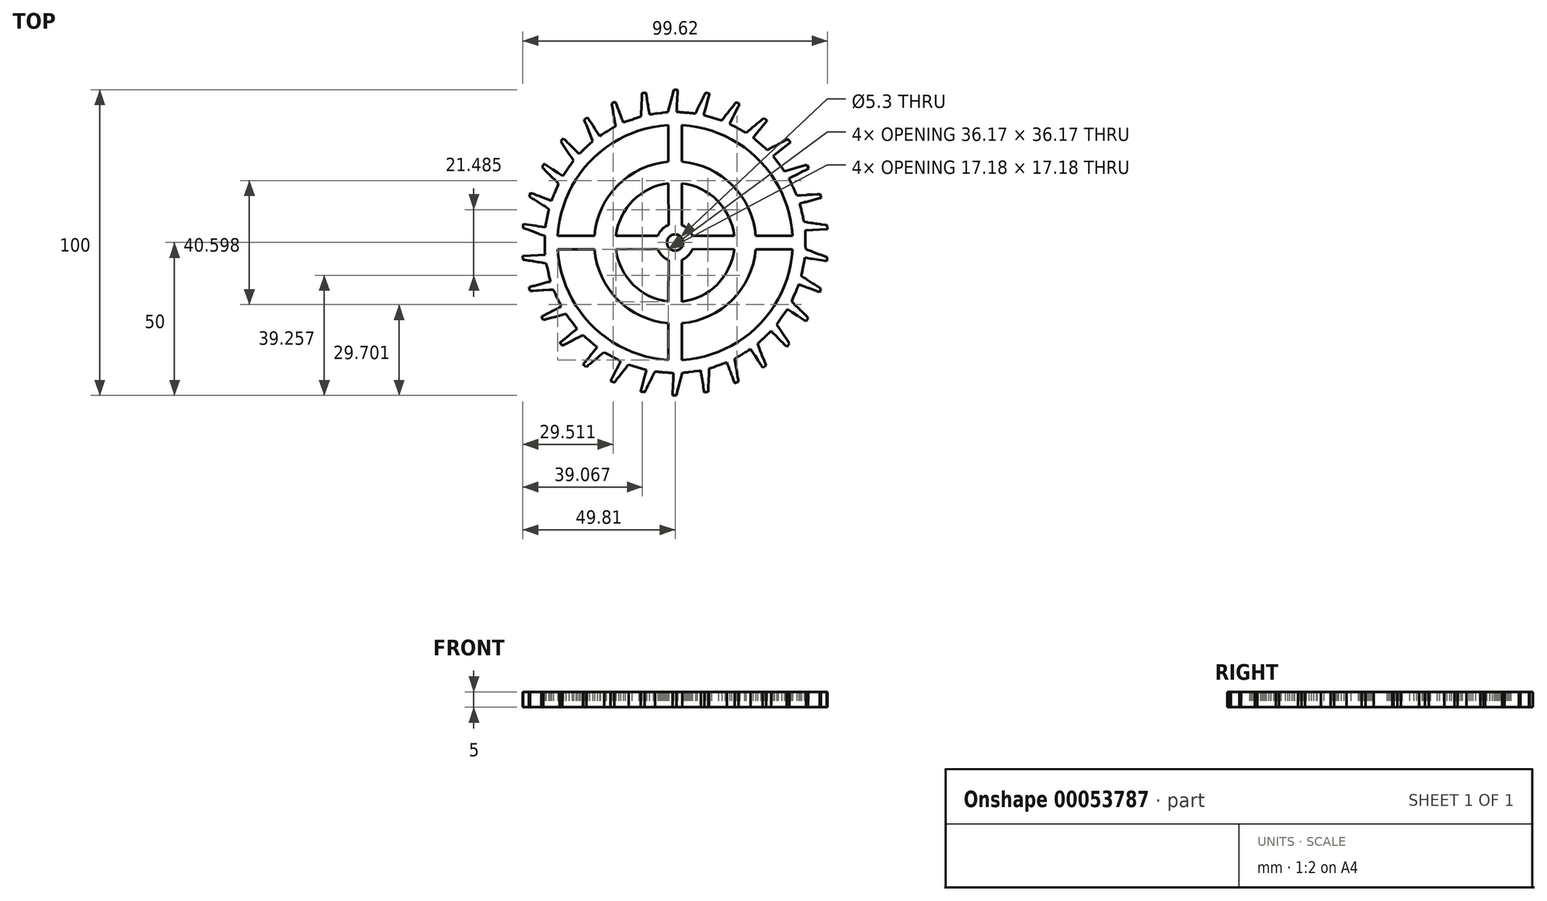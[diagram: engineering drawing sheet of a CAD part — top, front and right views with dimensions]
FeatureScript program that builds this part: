
annotation { "Feature Type Name" : "Feature", "Feature Type Description" : "" }
export const myFeature = defineFeature(function(context is Context, id is Id, definition is map)
    precondition{}
    {
        {
            var Q0;
            Q0=qCreatedBy(makeId("Top.planeOp"),FACE);
            var sketch = newSketch(context, id + "F0", { "sketchPlane" : qUnion([Q0])});
            skLineSegment(sketch, "E0", {"start": v(-36.57, 34.1) * mm, "end": v(-36.87, 33.77) * mm});
            skLineSegment(sketch, "E1", {"start": v(-36.87, 33.77) * mm, "end": v(-37.17, 33.44) * mm});
            skLineSegment(sketch, "E2", {"start": v(-37.17, 33.44) * mm, "end": v(-37.45, 33.13) * mm});
            skLineSegment(sketch, "E3", {"start": v(-37.45, 33.13) * mm, "end": v(-37.2, 32.76) * mm});
            skLineSegment(sketch, "E4", {"start": v(-37.2, 32.76) * mm, "end": v(-36.95, 32.39) * mm});
            skLineSegment(sketch, "E5", {"start": v(-36.95, 32.39) * mm, "end": v(-36.7, 32.02) * mm});
            skLineSegment(sketch, "E6", {"start": v(-36.7, 32.02) * mm, "end": v(-36.46, 31.65) * mm});
            skLineSegment(sketch, "E7", {"start": v(-36.46, 31.65) * mm, "end": v(-36.21, 31.28) * mm});
            skLineSegment(sketch, "E8", {"start": v(-36.21, 31.28) * mm, "end": v(-35.97, 30.9) * mm});
            skLineSegment(sketch, "E9", {"start": v(-35.97, 30.9) * mm, "end": v(-35.72, 30.53) * mm});
            skLineSegment(sketch, "E10", {"start": v(-35.72, 30.53) * mm, "end": v(-35.47, 30.16) * mm});
            skLineSegment(sketch, "E11", {"start": v(-35.47, 30.16) * mm, "end": v(-35.23, 29.8) * mm});
            skLineSegment(sketch, "E12", {"start": v(-35.23, 29.8) * mm, "end": v(-34.98, 29.42) * mm});
            skLineSegment(sketch, "E13", {"start": v(-34.98, 29.42) * mm, "end": v(-34.74, 29.05) * mm});
            skLineSegment(sketch, "E14", {"start": v(-34.74, 29.05) * mm, "end": v(-34.49, 28.68) * mm});
            skLineSegment(sketch, "E15", {"start": v(-34.49, 28.68) * mm, "end": v(-34.24, 28.3) * mm});
            skLineSegment(sketch, "E16", {"start": v(-34.24, 28.3) * mm, "end": v(-34, 27.93) * mm});
            skLineSegment(sketch, "E17", {"start": v(-34, 27.93) * mm, "end": v(-33.75, 27.56) * mm});
            skLineSegment(sketch, "E18", {"start": v(-33.75, 27.56) * mm, "end": v(-33.5, 27.2) * mm});
            skLineSegment(sketch, "E19", {"start": v(-33.5, 27.2) * mm, "end": v(-33.26, 26.83) * mm});
            skLineSegment(sketch, "E20", {"start": v(-33.26, 26.83) * mm, "end": v(-33.51, 26.46) * mm});
            skLineSegment(sketch, "E21", {"start": v(-33.51, 26.46) * mm, "end": v(-33.77, 26.1) * mm});
            skLineSegment(sketch, "E22", {"start": v(-33.77, 26.1) * mm, "end": v(-34.02, 25.73) * mm});
            skLineSegment(sketch, "E23", {"start": v(-34.02, 25.73) * mm, "end": v(-34.28, 25.37) * mm});
            skLineSegment(sketch, "E24", {"start": v(-34.28, 25.37) * mm, "end": v(-34.53, 25) * mm});
            skLineSegment(sketch, "E25", {"start": v(-34.53, 25) * mm, "end": v(-34.79, 24.63) * mm});
            skLineSegment(sketch, "E26", {"start": v(-34.79, 24.63) * mm, "end": v(-35.04, 24.27) * mm});
            skLineSegment(sketch, "E27", {"start": v(-35.04, 24.27) * mm, "end": v(-35.3, 23.9) * mm});
            skLineSegment(sketch, "E28", {"start": v(-35.3, 23.9) * mm, "end": v(-35.55, 23.53) * mm});
            skLineSegment(sketch, "E29", {"start": v(-35.55, 23.53) * mm, "end": v(-35.8, 23.17) * mm});
            skLineSegment(sketch, "E30", {"start": v(-35.8, 23.17) * mm, "end": v(-36.06, 22.8) * mm});
            skLineSegment(sketch, "E31", {"start": v(-36.06, 22.8) * mm, "end": v(-36.31, 22.44) * mm});
            skLineSegment(sketch, "E32", {"start": v(-36.31, 22.44) * mm, "end": v(-36.56, 22.07) * mm});
            skLineSegment(sketch, "E33", {"start": v(-36.56, 22.07) * mm, "end": v(-36.76, 21.8) * mm});
            skLineSegment(sketch, "E34", {"start": v(-36.76, 21.8) * mm, "end": v(-37.13, 22.03) * mm});
            skLineSegment(sketch, "E35", {"start": v(-37.13, 22.03) * mm, "end": v(-37.5, 22.28) * mm});
            skLineSegment(sketch, "E36", {"start": v(-37.5, 22.28) * mm, "end": v(-37.88, 22.52) * mm});
            skLineSegment(sketch, "E37", {"start": v(-37.88, 22.52) * mm, "end": v(-38.25, 22.76) * mm});
            skLineSegment(sketch, "E38", {"start": v(-38.25, 22.76) * mm, "end": v(-38.63, 23) * mm});
            skLineSegment(sketch, "E39", {"start": v(-38.63, 23) * mm, "end": v(-39, 23.25) * mm});
            skLineSegment(sketch, "E40", {"start": v(-39, 23.25) * mm, "end": v(-39.38, 23.49) * mm});
            skLineSegment(sketch, "E41", {"start": v(-39.38, 23.49) * mm, "end": v(-39.75, 23.73) * mm});
            skLineSegment(sketch, "E42", {"start": v(-39.75, 23.73) * mm, "end": v(-40.12, 23.98) * mm});
            skLineSegment(sketch, "E43", {"start": v(-40.12, 23.98) * mm, "end": v(-40.5, 24.22) * mm});
            skLineSegment(sketch, "E44", {"start": v(-40.5, 24.22) * mm, "end": v(-40.87, 24.46) * mm});
            skLineSegment(sketch, "E45", {"start": v(-40.87, 24.46) * mm, "end": v(-41.24, 24.7) * mm});
            skLineSegment(sketch, "E46", {"start": v(-41.24, 24.7) * mm, "end": v(-41.62, 24.95) * mm});
            skLineSegment(sketch, "E47", {"start": v(-41.62, 24.95) * mm, "end": v(-42, 25.19) * mm});
            skLineSegment(sketch, "E48", {"start": v(-42, 25.19) * mm, "end": v(-42.37, 25.43) * mm});
            skLineSegment(sketch, "E49", {"start": v(-42.37, 25.43) * mm, "end": v(-42.74, 25.67) * mm});
            skLineSegment(sketch, "E50", {"start": v(-42.74, 25.67) * mm, "end": v(-42.86, 25.75) * mm});
            skLineSegment(sketch, "E51", {"start": v(-42.86, 25.75) * mm, "end": v(-43.08, 25.37) * mm});
            skLineSegment(sketch, "E52", {"start": v(-43.08, 25.37) * mm, "end": v(-43.3, 24.98) * mm});
            skLineSegment(sketch, "E53", {"start": v(-43.3, 24.98) * mm, "end": v(-43.52, 24.62) * mm});
            skLineSegment(sketch, "E54", {"start": v(-43.52, 24.62) * mm, "end": v(-43.2, 24.3) * mm});
            skLineSegment(sketch, "E55", {"start": v(-43.2, 24.3) * mm, "end": v(-42.88, 24) * mm});
            skLineSegment(sketch, "E56", {"start": v(-42.88, 24) * mm, "end": v(-42.56, 23.69) * mm});
            skLineSegment(sketch, "E57", {"start": v(-42.56, 23.69) * mm, "end": v(-42.24, 23.37) * mm});
            skLineSegment(sketch, "E58", {"start": v(-42.24, 23.37) * mm, "end": v(-41.93, 23.06) * mm});
            skLineSegment(sketch, "E59", {"start": v(-41.93, 23.06) * mm, "end": v(-41.6, 22.75) * mm});
            skLineSegment(sketch, "E60", {"start": v(-41.6, 22.75) * mm, "end": v(-41.29, 22.44) * mm});
            skLineSegment(sketch, "E61", {"start": v(-41.29, 22.44) * mm, "end": v(-40.97, 22.13) * mm});
            skLineSegment(sketch, "E62", {"start": v(-40.97, 22.13) * mm, "end": v(-40.65, 21.82) * mm});
            skLineSegment(sketch, "E63", {"start": v(-40.65, 21.82) * mm, "end": v(-40.33, 21.5) * mm});
            skLineSegment(sketch, "E64", {"start": v(-40.33, 21.5) * mm, "end": v(-40.02, 21.2) * mm});
            skLineSegment(sketch, "E65", {"start": v(-40.02, 21.2) * mm, "end": v(-39.7, 20.88) * mm});
            skLineSegment(sketch, "E66", {"start": v(-39.7, 20.88) * mm, "end": v(-39.38, 20.57) * mm});
            skLineSegment(sketch, "E67", {"start": v(-39.38, 20.57) * mm, "end": v(-39.06, 20.26) * mm});
            skLineSegment(sketch, "E68", {"start": v(-39.06, 20.26) * mm, "end": v(-38.74, 19.94) * mm});
            skLineSegment(sketch, "E69", {"start": v(-38.74, 19.94) * mm, "end": v(-38.42, 19.63) * mm});
            skLineSegment(sketch, "E70", {"start": v(-38.42, 19.63) * mm, "end": v(-38.11, 19.33) * mm});
            skLineSegment(sketch, "E71", {"start": v(-38.11, 19.33) * mm, "end": v(-38.28, 18.92) * mm});
            skLineSegment(sketch, "E72", {"start": v(-38.28, 18.92) * mm, "end": v(-38.46, 18.5) * mm});
            skLineSegment(sketch, "E73", {"start": v(-38.46, 18.5) * mm, "end": v(-38.63, 18.1) * mm});
            skLineSegment(sketch, "E74", {"start": v(-38.63, 18.1) * mm, "end": v(-38.8, 17.68) * mm});
            skLineSegment(sketch, "E75", {"start": v(-38.8, 17.68) * mm, "end": v(-38.97, 17.27) * mm});
            skLineSegment(sketch, "E76", {"start": v(-38.97, 17.27) * mm, "end": v(-39.15, 16.86) * mm});
            skLineSegment(sketch, "E77", {"start": v(-39.15, 16.86) * mm, "end": v(-39.32, 16.45) * mm});
            skLineSegment(sketch, "E78", {"start": v(-39.32, 16.45) * mm, "end": v(-39.5, 16.04) * mm});
            skLineSegment(sketch, "E79", {"start": v(-39.5, 16.04) * mm, "end": v(-39.66, 15.63) * mm});
            skLineSegment(sketch, "E80", {"start": v(-39.66, 15.63) * mm, "end": v(-39.84, 15.22) * mm});
            skLineSegment(sketch, "E81", {"start": v(-39.84, 15.22) * mm, "end": v(-40, 14.8) * mm});
            skLineSegment(sketch, "E82", {"start": v(-40, 14.8) * mm, "end": v(-40.18, 14.4) * mm});
            skLineSegment(sketch, "E83", {"start": v(-40.18, 14.4) * mm, "end": v(-40.35, 13.99) * mm});
            skLineSegment(sketch, "E84", {"start": v(-40.35, 13.99) * mm, "end": v(-40.49, 13.67) * mm});
            skLineSegment(sketch, "E85", {"start": v(-40.49, 13.67) * mm, "end": v(-40.9, 13.83) * mm});
            skLineSegment(sketch, "E86", {"start": v(-40.9, 13.83) * mm, "end": v(-41.32, 14) * mm});
            skLineSegment(sketch, "E87", {"start": v(-41.32, 14) * mm, "end": v(-41.73, 14.15) * mm});
            skLineSegment(sketch, "E88", {"start": v(-41.73, 14.15) * mm, "end": v(-42.15, 14.31) * mm});
            skLineSegment(sketch, "E89", {"start": v(-42.15, 14.31) * mm, "end": v(-42.57, 14.47) * mm});
            skLineSegment(sketch, "E90", {"start": v(-42.57, 14.47) * mm, "end": v(-42.98, 14.63) * mm});
            skLineSegment(sketch, "E91", {"start": v(-42.98, 14.63) * mm, "end": v(-43.4, 14.8) * mm});
            skLineSegment(sketch, "E92", {"start": v(-43.4, 14.8) * mm, "end": v(-43.81, 14.95) * mm});
            skLineSegment(sketch, "E93", {"start": v(-43.81, 14.95) * mm, "end": v(-44.23, 15.1) * mm});
            skLineSegment(sketch, "E94", {"start": v(-44.23, 15.1) * mm, "end": v(-44.65, 15.27) * mm});
            skLineSegment(sketch, "E95", {"start": v(-44.65, 15.27) * mm, "end": v(-45.06, 15.43) * mm});
            skLineSegment(sketch, "E96", {"start": v(-45.06, 15.43) * mm, "end": v(-45.48, 15.59) * mm});
            skLineSegment(sketch, "E97", {"start": v(-45.48, 15.59) * mm, "end": v(-45.9, 15.75) * mm});
            skLineSegment(sketch, "E98", {"start": v(-45.9, 15.75) * mm, "end": v(-46.31, 15.9) * mm});
            skLineSegment(sketch, "E99", {"start": v(-46.31, 15.9) * mm, "end": v(-46.73, 16.07) * mm});
            skLineSegment(sketch, "E100", {"start": v(-46.73, 16.07) * mm, "end": v(-47.14, 16.23) * mm});
            skLineSegment(sketch, "E101", {"start": v(-47.14, 16.23) * mm, "end": v(-47.28, 16.28) * mm});
            skLineSegment(sketch, "E102", {"start": v(-47.28, 16.28) * mm, "end": v(-47.42, 15.86) * mm});
            skLineSegment(sketch, "E103", {"start": v(-47.42, 15.86) * mm, "end": v(-47.56, 15.43) * mm});
            skLineSegment(sketch, "E104", {"start": v(-47.56, 15.43) * mm, "end": v(-47.69, 15.04) * mm});
            skLineSegment(sketch, "E105", {"start": v(-47.69, 15.04) * mm, "end": v(-47.3, 14.8) * mm});
            skLineSegment(sketch, "E106", {"start": v(-47.3, 14.8) * mm, "end": v(-46.93, 14.56) * mm});
            skLineSegment(sketch, "E107", {"start": v(-46.93, 14.56) * mm, "end": v(-46.56, 14.32) * mm});
            skLineSegment(sketch, "E108", {"start": v(-46.56, 14.32) * mm, "end": v(-46.18, 14.08) * mm});
            skLineSegment(sketch, "E109", {"start": v(-46.18, 14.08) * mm, "end": v(-45.8, 13.84) * mm});
            skLineSegment(sketch, "E110", {"start": v(-45.8, 13.84) * mm, "end": v(-45.43, 13.6) * mm});
            skLineSegment(sketch, "E111", {"start": v(-45.43, 13.6) * mm, "end": v(-45.05, 13.36) * mm});
            skLineSegment(sketch, "E112", {"start": v(-45.05, 13.36) * mm, "end": v(-44.68, 13.13) * mm});
            skLineSegment(sketch, "E113", {"start": v(-44.68, 13.13) * mm, "end": v(-44.3, 12.89) * mm});
            skLineSegment(sketch, "E114", {"start": v(-44.3, 12.89) * mm, "end": v(-43.92, 12.65) * mm});
            skLineSegment(sketch, "E115", {"start": v(-43.92, 12.65) * mm, "end": v(-43.55, 12.4) * mm});
            skLineSegment(sketch, "E116", {"start": v(-43.55, 12.4) * mm, "end": v(-43.17, 12.17) * mm});
            skLineSegment(sketch, "E117", {"start": v(-43.17, 12.17) * mm, "end": v(-42.8, 11.93) * mm});
            skLineSegment(sketch, "E118", {"start": v(-42.8, 11.93) * mm, "end": v(-42.42, 11.7) * mm});
            skLineSegment(sketch, "E119", {"start": v(-42.42, 11.7) * mm, "end": v(-42.04, 11.45) * mm});
            skLineSegment(sketch, "E120", {"start": v(-42.04, 11.45) * mm, "end": v(-41.67, 11.22) * mm});
            skLineSegment(sketch, "E121", {"start": v(-41.67, 11.22) * mm, "end": v(-41.3, 10.98) * mm});
            skLineSegment(sketch, "E122", {"start": v(-41.3, 10.98) * mm, "end": v(-41.38, 10.54) * mm});
            skLineSegment(sketch, "E123", {"start": v(-41.38, 10.54) * mm, "end": v(-41.46, 10.1) * mm});
            skLineSegment(sketch, "E124", {"start": v(-41.46, 10.1) * mm, "end": v(-41.55, 9.67) * mm});
            skLineSegment(sketch, "E125", {"start": v(-41.55, 9.67) * mm, "end": v(-41.63, 9.23) * mm});
            skLineSegment(sketch, "E126", {"start": v(-41.63, 9.23) * mm, "end": v(-41.71, 8.8) * mm});
            skLineSegment(sketch, "E127", {"start": v(-41.71, 8.8) * mm, "end": v(-41.8, 8.35) * mm});
            skLineSegment(sketch, "E128", {"start": v(-41.8, 8.35) * mm, "end": v(-41.88, 7.92) * mm});
            skLineSegment(sketch, "E129", {"start": v(-41.88, 7.92) * mm, "end": v(-41.96, 7.48) * mm});
            skLineSegment(sketch, "E130", {"start": v(-41.96, 7.48) * mm, "end": v(-42.05, 7.04) * mm});
            skLineSegment(sketch, "E131", {"start": v(-42.05, 7.04) * mm, "end": v(-42.13, 6.6) * mm});
            skLineSegment(sketch, "E132", {"start": v(-42.13, 6.6) * mm, "end": v(-42.21, 6.17) * mm});
            skLineSegment(sketch, "E133", {"start": v(-42.21, 6.17) * mm, "end": v(-42.3, 5.73) * mm});
            skLineSegment(sketch, "E134", {"start": v(-42.3, 5.73) * mm, "end": v(-42.38, 5.3) * mm});
            skLineSegment(sketch, "E135", {"start": v(-42.38, 5.3) * mm, "end": v(-42.44, 4.96) * mm});
            skLineSegment(sketch, "E136", {"start": v(-42.44, 4.96) * mm, "end": v(-42.88, 5.03) * mm});
            skLineSegment(sketch, "E137", {"start": v(-42.88, 5.03) * mm, "end": v(-43.32, 5.1) * mm});
            skLineSegment(sketch, "E138", {"start": v(-43.32, 5.1) * mm, "end": v(-43.76, 5.16) * mm});
            skLineSegment(sketch, "E139", {"start": v(-43.76, 5.16) * mm, "end": v(-44.2, 5.23) * mm});
            skLineSegment(sketch, "E140", {"start": v(-44.2, 5.23) * mm, "end": v(-44.65, 5.3) * mm});
            skLineSegment(sketch, "E141", {"start": v(-44.65, 5.3) * mm, "end": v(-45.09, 5.37) * mm});
            skLineSegment(sketch, "E142", {"start": v(-45.09, 5.37) * mm, "end": v(-45.53, 5.44) * mm});
            skLineSegment(sketch, "E143", {"start": v(-45.53, 5.44) * mm, "end": v(-45.97, 5.51) * mm});
            skLineSegment(sketch, "E144", {"start": v(-45.97, 5.51) * mm, "end": v(-46.4, 5.58) * mm});
            skLineSegment(sketch, "E145", {"start": v(-46.4, 5.58) * mm, "end": v(-46.85, 5.65) * mm});
            skLineSegment(sketch, "E146", {"start": v(-46.85, 5.65) * mm, "end": v(-47.29, 5.72) * mm});
            skLineSegment(sketch, "E147", {"start": v(-47.29, 5.72) * mm, "end": v(-47.73, 5.8) * mm});
            skLineSegment(sketch, "E148", {"start": v(-47.73, 5.8) * mm, "end": v(-48.17, 5.86) * mm});
            skLineSegment(sketch, "E149", {"start": v(-48.17, 5.86) * mm, "end": v(-48.6, 5.93) * mm});
            skLineSegment(sketch, "E150", {"start": v(-48.6, 5.93) * mm, "end": v(-49.05, 6) * mm});
            skLineSegment(sketch, "E151", {"start": v(-49.05, 6) * mm, "end": v(-49.49, 6.07) * mm});
            skLineSegment(sketch, "E152", {"start": v(-49.49, 6.07) * mm, "end": v(-49.63, 6.1) * mm});
            skLineSegment(sketch, "E153", {"start": v(-49.63, 6.1) * mm, "end": v(-49.68, 5.65) * mm});
            skLineSegment(sketch, "E154", {"start": v(-49.68, 5.65) * mm, "end": v(-49.72, 5.2) * mm});
            skLineSegment(sketch, "E155", {"start": v(-49.72, 5.2) * mm, "end": v(-49.77, 4.8) * mm});
            skLineSegment(sketch, "E156", {"start": v(-49.77, 4.8) * mm, "end": v(-49.35, 4.64) * mm});
            skLineSegment(sketch, "E157", {"start": v(-49.35, 4.64) * mm, "end": v(-48.93, 4.48) * mm});
            skLineSegment(sketch, "E158", {"start": v(-48.93, 4.48) * mm, "end": v(-48.52, 4.33) * mm});
            skLineSegment(sketch, "E159", {"start": v(-48.52, 4.33) * mm, "end": v(-48.1, 4.17) * mm});
            skLineSegment(sketch, "E160", {"start": v(-48.1, 4.17) * mm, "end": v(-47.68, 4.02) * mm});
            skLineSegment(sketch, "E161", {"start": v(-47.68, 4.02) * mm, "end": v(-47.26, 3.86) * mm});
            skLineSegment(sketch, "E162", {"start": v(-47.26, 3.86) * mm, "end": v(-46.85, 3.7) * mm});
            skLineSegment(sketch, "E163", {"start": v(-46.85, 3.7) * mm, "end": v(-46.43, 3.55) * mm});
            skLineSegment(sketch, "E164", {"start": v(-46.43, 3.55) * mm, "end": v(-46.01, 3.4) * mm});
            skLineSegment(sketch, "E165", {"start": v(-46.01, 3.4) * mm, "end": v(-45.6, 3.24) * mm});
            skLineSegment(sketch, "E166", {"start": v(-45.6, 3.24) * mm, "end": v(-45.18, 3.08) * mm});
            skLineSegment(sketch, "E167", {"start": v(-45.18, 3.08) * mm, "end": v(-44.76, 2.93) * mm});
            skLineSegment(sketch, "E168", {"start": v(-44.76, 2.93) * mm, "end": v(-44.34, 2.77) * mm});
            skLineSegment(sketch, "E169", {"start": v(-44.34, 2.77) * mm, "end": v(-43.92, 2.62) * mm});
            skLineSegment(sketch, "E170", {"start": v(-43.92, 2.62) * mm, "end": v(-43.5, 2.46) * mm});
            skLineSegment(sketch, "E171", {"start": v(-43.5, 2.46) * mm, "end": v(-43.09, 2.3) * mm});
            skLineSegment(sketch, "E172", {"start": v(-43.09, 2.3) * mm, "end": v(-42.68, 2.16) * mm});
            skLineSegment(sketch, "E173", {"start": v(-42.68, 2.16) * mm, "end": v(-42.67, 1.7) * mm});
            skLineSegment(sketch, "E174", {"start": v(-42.67, 1.7) * mm, "end": v(-42.66, 1.26) * mm});
            skLineSegment(sketch, "E175", {"start": v(-42.66, 1.26) * mm, "end": v(-42.65, 0.82) * mm});
            skLineSegment(sketch, "E176", {"start": v(-42.65, 0.82) * mm, "end": v(-42.64, 0.37) * mm});
            skLineSegment(sketch, "E177", {"start": v(-42.64, 0.37) * mm, "end": v(-42.63, -0.07) * mm});
            skLineSegment(sketch, "E178", {"start": v(-42.63, -0.07) * mm, "end": v(-42.62, -0.52) * mm});
            skLineSegment(sketch, "E179", {"start": v(-42.62, -0.52) * mm, "end": v(-42.61, -0.96) * mm});
            skLineSegment(sketch, "E180", {"start": v(-42.61, -0.96) * mm, "end": v(-42.6, -1.4) * mm});
            skLineSegment(sketch, "E181", {"start": v(-42.6, -1.4) * mm, "end": v(-42.6, -1.85) * mm});
            skLineSegment(sketch, "E182", {"start": v(-42.6, -1.85) * mm, "end": v(-42.58, -2.3) * mm});
            skLineSegment(sketch, "E183", {"start": v(-42.58, -2.3) * mm, "end": v(-42.57, -2.75) * mm});
            skLineSegment(sketch, "E184", {"start": v(-42.57, -2.75) * mm, "end": v(-42.56, -3.2) * mm});
            skLineSegment(sketch, "E185", {"start": v(-42.56, -3.2) * mm, "end": v(-42.55, -3.64) * mm});
            skLineSegment(sketch, "E186", {"start": v(-42.55, -3.64) * mm, "end": v(-42.55, -3.98) * mm});
            skLineSegment(sketch, "E187", {"start": v(-42.55, -3.98) * mm, "end": v(-43, -4) * mm});
            skLineSegment(sketch, "E188", {"start": v(-43, -4) * mm, "end": v(-43.44, -4.02) * mm});
            skLineSegment(sketch, "E189", {"start": v(-43.44, -4.02) * mm, "end": v(-43.88, -4.05) * mm});
            skLineSegment(sketch, "E190", {"start": v(-43.88, -4.05) * mm, "end": v(-44.33, -4.07) * mm});
            skLineSegment(sketch, "E191", {"start": v(-44.33, -4.07) * mm, "end": v(-44.77, -4.1) * mm});
            skLineSegment(sketch, "E192", {"start": v(-44.77, -4.1) * mm, "end": v(-45.22, -4.12) * mm});
            skLineSegment(sketch, "E193", {"start": v(-45.22, -4.12) * mm, "end": v(-45.66, -4.14) * mm});
            skLineSegment(sketch, "E194", {"start": v(-45.66, -4.14) * mm, "end": v(-46.1, -4.16) * mm});
            skLineSegment(sketch, "E195", {"start": v(-46.1, -4.16) * mm, "end": v(-46.55, -4.19) * mm});
            skLineSegment(sketch, "E196", {"start": v(-46.55, -4.19) * mm, "end": v(-47, -4.21) * mm});
            skLineSegment(sketch, "E197", {"start": v(-47, -4.21) * mm, "end": v(-47.44, -4.23) * mm});
            skLineSegment(sketch, "E198", {"start": v(-47.44, -4.23) * mm, "end": v(-47.89, -4.26) * mm});
            skLineSegment(sketch, "E199", {"start": v(-47.89, -4.26) * mm, "end": v(-48.33, -4.28) * mm});
            skLineSegment(sketch, "E200", {"start": v(-48.33, -4.28) * mm, "end": v(-48.78, -4.3) * mm});
            skLineSegment(sketch, "E201", {"start": v(-48.78, -4.3) * mm, "end": v(-49.22, -4.33) * mm});
            skLineSegment(sketch, "E202", {"start": v(-49.22, -4.33) * mm, "end": v(-49.67, -4.35) * mm});
            skLineSegment(sketch, "E203", {"start": v(-49.67, -4.35) * mm, "end": v(-49.8, -4.36) * mm});
            skLineSegment(sketch, "E204", {"start": v(-49.8, -4.36) * mm, "end": v(-49.77, -4.8) * mm});
            skLineSegment(sketch, "E205", {"start": v(-49.77, -4.8) * mm, "end": v(-49.72, -5.24) * mm});
            skLineSegment(sketch, "E206", {"start": v(-49.72, -5.24) * mm, "end": v(-49.68, -5.66) * mm});
            skLineSegment(sketch, "E207", {"start": v(-49.68, -5.66) * mm, "end": v(-49.24, -5.73) * mm});
            skLineSegment(sketch, "E208", {"start": v(-49.24, -5.73) * mm, "end": v(-48.8, -5.8) * mm});
            skLineSegment(sketch, "E209", {"start": v(-48.8, -5.8) * mm, "end": v(-48.36, -5.86) * mm});
            skLineSegment(sketch, "E210", {"start": v(-48.36, -5.86) * mm, "end": v(-47.92, -5.92) * mm});
            skLineSegment(sketch, "E211", {"start": v(-47.92, -5.92) * mm, "end": v(-47.47, -5.99) * mm});
            skLineSegment(sketch, "E212", {"start": v(-47.47, -5.99) * mm, "end": v(-47.03, -6.05) * mm});
            skLineSegment(sketch, "E213", {"start": v(-47.03, -6.05) * mm, "end": v(-46.6, -6.12) * mm});
            skLineSegment(sketch, "E214", {"start": v(-46.6, -6.12) * mm, "end": v(-46.15, -6.18) * mm});
            skLineSegment(sketch, "E215", {"start": v(-46.15, -6.18) * mm, "end": v(-45.71, -6.25) * mm});
            skLineSegment(sketch, "E216", {"start": v(-45.71, -6.25) * mm, "end": v(-45.27, -6.31) * mm});
            skLineSegment(sketch, "E217", {"start": v(-45.27, -6.31) * mm, "end": v(-44.83, -6.38) * mm});
            skLineSegment(sketch, "E218", {"start": v(-44.83, -6.38) * mm, "end": v(-44.39, -6.44) * mm});
            skLineSegment(sketch, "E219", {"start": v(-44.39, -6.44) * mm, "end": v(-43.95, -6.5) * mm});
            skLineSegment(sketch, "E220", {"start": v(-43.95, -6.5) * mm, "end": v(-43.5, -6.57) * mm});
            skLineSegment(sketch, "E221", {"start": v(-43.5, -6.57) * mm, "end": v(-43.07, -6.64) * mm});
            skLineSegment(sketch, "E222", {"start": v(-43.07, -6.64) * mm, "end": v(-42.63, -6.7) * mm});
            skLineSegment(sketch, "E223", {"start": v(-42.63, -6.7) * mm, "end": v(-42.2, -6.77) * mm});
            skLineSegment(sketch, "E224", {"start": v(-42.2, -6.77) * mm, "end": v(-42.1, -7.2) * mm});
            skLineSegment(sketch, "E225", {"start": v(-42.1, -7.2) * mm, "end": v(-41.99, -7.63) * mm});
            skLineSegment(sketch, "E226", {"start": v(-41.99, -7.63) * mm, "end": v(-41.89, -8.07) * mm});
            skLineSegment(sketch, "E227", {"start": v(-41.89, -8.07) * mm, "end": v(-41.79, -8.5) * mm});
            skLineSegment(sketch, "E228", {"start": v(-41.79, -8.5) * mm, "end": v(-41.68, -8.93) * mm});
            skLineSegment(sketch, "E229", {"start": v(-41.68, -8.93) * mm, "end": v(-41.58, -9.37) * mm});
            skLineSegment(sketch, "E230", {"start": v(-41.58, -9.37) * mm, "end": v(-41.48, -9.8) * mm});
            skLineSegment(sketch, "E231", {"start": v(-41.48, -9.8) * mm, "end": v(-41.38, -10.24) * mm});
            skLineSegment(sketch, "E232", {"start": v(-41.38, -10.24) * mm, "end": v(-41.28, -10.67) * mm});
            skLineSegment(sketch, "E233", {"start": v(-41.28, -10.67) * mm, "end": v(-41.17, -11.1) * mm});
            skLineSegment(sketch, "E234", {"start": v(-41.17, -11.1) * mm, "end": v(-41.07, -11.54) * mm});
            skLineSegment(sketch, "E235", {"start": v(-41.07, -11.54) * mm, "end": v(-40.97, -11.97) * mm});
            skLineSegment(sketch, "E236", {"start": v(-40.97, -11.97) * mm, "end": v(-40.87, -12.4) * mm});
            skLineSegment(sketch, "E237", {"start": v(-40.87, -12.4) * mm, "end": v(-40.8, -12.74) * mm});
            skLineSegment(sketch, "E238", {"start": v(-40.8, -12.74) * mm, "end": v(-41.22, -12.85) * mm});
            skLineSegment(sketch, "E239", {"start": v(-41.22, -12.85) * mm, "end": v(-41.65, -12.97) * mm});
            skLineSegment(sketch, "E240", {"start": v(-41.65, -12.97) * mm, "end": v(-42.08, -13.08) * mm});
            skLineSegment(sketch, "E241", {"start": v(-42.08, -13.08) * mm, "end": v(-42.51, -13.2) * mm});
            skLineSegment(sketch, "E242", {"start": v(-42.51, -13.2) * mm, "end": v(-42.94, -13.31) * mm});
            skLineSegment(sketch, "E243", {"start": v(-42.94, -13.31) * mm, "end": v(-43.37, -13.43) * mm});
            skLineSegment(sketch, "E244", {"start": v(-43.37, -13.43) * mm, "end": v(-43.8, -13.54) * mm});
            skLineSegment(sketch, "E245", {"start": v(-43.8, -13.54) * mm, "end": v(-44.23, -13.66) * mm});
            skLineSegment(sketch, "E246", {"start": v(-44.23, -13.66) * mm, "end": v(-44.66, -13.77) * mm});
            skLineSegment(sketch, "E247", {"start": v(-44.66, -13.77) * mm, "end": v(-45.1, -13.89) * mm});
            skLineSegment(sketch, "E248", {"start": v(-45.1, -13.89) * mm, "end": v(-45.53, -14) * mm});
            skLineSegment(sketch, "E249", {"start": v(-45.53, -14) * mm, "end": v(-45.96, -14.12) * mm});
            skLineSegment(sketch, "E250", {"start": v(-45.96, -14.12) * mm, "end": v(-46.39, -14.24) * mm});
            skLineSegment(sketch, "E251", {"start": v(-46.39, -14.24) * mm, "end": v(-46.82, -14.35) * mm});
            skLineSegment(sketch, "E252", {"start": v(-46.82, -14.35) * mm, "end": v(-47.25, -14.47) * mm});
            skLineSegment(sketch, "E253", {"start": v(-47.25, -14.47) * mm, "end": v(-47.68, -14.58) * mm});
            skLineSegment(sketch, "E254", {"start": v(-47.68, -14.58) * mm, "end": v(-47.82, -14.62) * mm});
            skLineSegment(sketch, "E255", {"start": v(-47.82, -14.62) * mm, "end": v(-47.68, -15.04) * mm});
            skLineSegment(sketch, "E256", {"start": v(-47.68, -15.04) * mm, "end": v(-47.54, -15.47) * mm});
            skLineSegment(sketch, "E257", {"start": v(-47.54, -15.47) * mm, "end": v(-47.42, -15.87) * mm});
            skLineSegment(sketch, "E258", {"start": v(-47.42, -15.87) * mm, "end": v(-46.97, -15.84) * mm});
            skLineSegment(sketch, "E259", {"start": v(-46.97, -15.84) * mm, "end": v(-46.53, -15.8) * mm});
            skLineSegment(sketch, "E260", {"start": v(-46.53, -15.8) * mm, "end": v(-46.08, -15.78) * mm});
            skLineSegment(sketch, "E261", {"start": v(-46.08, -15.78) * mm, "end": v(-45.64, -15.75) * mm});
            skLineSegment(sketch, "E262", {"start": v(-45.64, -15.75) * mm, "end": v(-45.2, -15.73) * mm});
            skLineSegment(sketch, "E263", {"start": v(-45.2, -15.73) * mm, "end": v(-44.75, -15.7) * mm});
            skLineSegment(sketch, "E264", {"start": v(-44.75, -15.7) * mm, "end": v(-44.3, -15.67) * mm});
            skLineSegment(sketch, "E265", {"start": v(-44.3, -15.67) * mm, "end": v(-43.86, -15.64) * mm});
            skLineSegment(sketch, "E266", {"start": v(-43.86, -15.64) * mm, "end": v(-43.41, -15.61) * mm});
            skLineSegment(sketch, "E267", {"start": v(-43.41, -15.61) * mm, "end": v(-42.97, -15.59) * mm});
            skLineSegment(sketch, "E268", {"start": v(-42.97, -15.59) * mm, "end": v(-42.52, -15.56) * mm});
            skLineSegment(sketch, "E269", {"start": v(-42.52, -15.56) * mm, "end": v(-42.08, -15.53) * mm});
            skLineSegment(sketch, "E270", {"start": v(-42.08, -15.53) * mm, "end": v(-41.63, -15.5) * mm});
            skLineSegment(sketch, "E271", {"start": v(-41.63, -15.5) * mm, "end": v(-41.19, -15.47) * mm});
            skLineSegment(sketch, "E272", {"start": v(-41.19, -15.47) * mm, "end": v(-40.75, -15.45) * mm});
            skLineSegment(sketch, "E273", {"start": v(-40.75, -15.45) * mm, "end": v(-40.3, -15.42) * mm});
            skLineSegment(sketch, "E274", {"start": v(-40.3, -15.42) * mm, "end": v(-39.87, -15.39) * mm});
            skLineSegment(sketch, "E275", {"start": v(-39.87, -15.39) * mm, "end": v(-39.68, -15.8) * mm});
            skLineSegment(sketch, "E276", {"start": v(-39.68, -15.8) * mm, "end": v(-39.49, -16.2) * mm});
            skLineSegment(sketch, "E277", {"start": v(-39.49, -16.2) * mm, "end": v(-39.3, -16.6) * mm});
            skLineSegment(sketch, "E278", {"start": v(-39.3, -16.6) * mm, "end": v(-39.1, -17) * mm});
            skLineSegment(sketch, "E279", {"start": v(-39.1, -17) * mm, "end": v(-38.92, -17.4) * mm});
            skLineSegment(sketch, "E280", {"start": v(-38.92, -17.4) * mm, "end": v(-38.73, -17.8) * mm});
            skLineSegment(sketch, "E281", {"start": v(-38.73, -17.8) * mm, "end": v(-38.54, -18.21) * mm});
            skLineSegment(sketch, "E282", {"start": v(-38.54, -18.21) * mm, "end": v(-38.35, -18.61) * mm});
            skLineSegment(sketch, "E283", {"start": v(-38.35, -18.61) * mm, "end": v(-38.16, -19.02) * mm});
            skLineSegment(sketch, "E284", {"start": v(-38.16, -19.02) * mm, "end": v(-37.97, -19.42) * mm});
            skLineSegment(sketch, "E285", {"start": v(-37.97, -19.42) * mm, "end": v(-37.78, -19.82) * mm});
            skLineSegment(sketch, "E286", {"start": v(-37.78, -19.82) * mm, "end": v(-37.59, -20.23) * mm});
            skLineSegment(sketch, "E287", {"start": v(-37.59, -20.23) * mm, "end": v(-37.4, -20.63) * mm});
            skLineSegment(sketch, "E288", {"start": v(-37.4, -20.63) * mm, "end": v(-37.25, -20.94) * mm});
            skLineSegment(sketch, "E289", {"start": v(-37.25, -20.94) * mm, "end": v(-37.65, -21.14) * mm});
            skLineSegment(sketch, "E290", {"start": v(-37.65, -21.14) * mm, "end": v(-38.05, -21.34) * mm});
            skLineSegment(sketch, "E291", {"start": v(-38.05, -21.34) * mm, "end": v(-38.44, -21.55) * mm});
            skLineSegment(sketch, "E292", {"start": v(-38.44, -21.55) * mm, "end": v(-38.84, -21.75) * mm});
            skLineSegment(sketch, "E293", {"start": v(-38.84, -21.75) * mm, "end": v(-39.24, -21.95) * mm});
            skLineSegment(sketch, "E294", {"start": v(-39.24, -21.95) * mm, "end": v(-39.63, -22.15) * mm});
            skLineSegment(sketch, "E295", {"start": v(-39.63, -22.15) * mm, "end": v(-40.03, -22.35) * mm});
            skLineSegment(sketch, "E296", {"start": v(-40.03, -22.35) * mm, "end": v(-40.43, -22.56) * mm});
            skLineSegment(sketch, "E297", {"start": v(-40.43, -22.56) * mm, "end": v(-40.82, -22.76) * mm});
            skLineSegment(sketch, "E298", {"start": v(-40.82, -22.76) * mm, "end": v(-41.22, -22.96) * mm});
            skLineSegment(sketch, "E299", {"start": v(-41.22, -22.96) * mm, "end": v(-41.62, -23.16) * mm});
            skLineSegment(sketch, "E300", {"start": v(-41.62, -23.16) * mm, "end": v(-42.02, -23.37) * mm});
            skLineSegment(sketch, "E301", {"start": v(-42.02, -23.37) * mm, "end": v(-42.41, -23.57) * mm});
            skLineSegment(sketch, "E302", {"start": v(-42.41, -23.57) * mm, "end": v(-42.8, -23.77) * mm});
            skLineSegment(sketch, "E303", {"start": v(-42.8, -23.77) * mm, "end": v(-43.2, -23.97) * mm});
            skLineSegment(sketch, "E304", {"start": v(-43.2, -23.97) * mm, "end": v(-43.6, -24.18) * mm});
            skLineSegment(sketch, "E305", {"start": v(-43.6, -24.18) * mm, "end": v(-43.73, -24.24) * mm});
            skLineSegment(sketch, "E306", {"start": v(-43.73, -24.24) * mm, "end": v(-43.5, -24.63) * mm});
            skLineSegment(sketch, "E307", {"start": v(-43.5, -24.63) * mm, "end": v(-43.29, -25.01) * mm});
            skLineSegment(sketch, "E308", {"start": v(-43.29, -25.01) * mm, "end": v(-43.08, -25.38) * mm});
            skLineSegment(sketch, "E309", {"start": v(-43.08, -25.38) * mm, "end": v(-42.65, -25.26) * mm});
            skLineSegment(sketch, "E310", {"start": v(-42.65, -25.26) * mm, "end": v(-42.22, -25.14) * mm});
            skLineSegment(sketch, "E311", {"start": v(-42.22, -25.14) * mm, "end": v(-41.8, -25.02) * mm});
            skLineSegment(sketch, "E312", {"start": v(-41.8, -25.02) * mm, "end": v(-41.36, -24.9) * mm});
            skLineSegment(sketch, "E313", {"start": v(-41.36, -24.9) * mm, "end": v(-40.94, -24.78) * mm});
            skLineSegment(sketch, "E314", {"start": v(-40.94, -24.78) * mm, "end": v(-40.5, -24.66) * mm});
            skLineSegment(sketch, "E315", {"start": v(-40.5, -24.66) * mm, "end": v(-40.08, -24.54) * mm});
            skLineSegment(sketch, "E316", {"start": v(-40.08, -24.54) * mm, "end": v(-39.65, -24.42) * mm});
            skLineSegment(sketch, "E317", {"start": v(-39.65, -24.42) * mm, "end": v(-39.22, -24.3) * mm});
            skLineSegment(sketch, "E318", {"start": v(-39.22, -24.3) * mm, "end": v(-38.79, -24.18) * mm});
            skLineSegment(sketch, "E319", {"start": v(-38.79, -24.18) * mm, "end": v(-38.36, -24.06) * mm});
            skLineSegment(sketch, "E320", {"start": v(-38.36, -24.06) * mm, "end": v(-37.93, -23.94) * mm});
            skLineSegment(sketch, "E321", {"start": v(-37.93, -23.94) * mm, "end": v(-37.5, -23.82) * mm});
            skLineSegment(sketch, "E322", {"start": v(-37.5, -23.82) * mm, "end": v(-37.07, -23.7) * mm});
            skLineSegment(sketch, "E323", {"start": v(-37.07, -23.7) * mm, "end": v(-36.64, -23.58) * mm});
            skLineSegment(sketch, "E324", {"start": v(-36.64, -23.58) * mm, "end": v(-36.21, -23.46) * mm});
            skLineSegment(sketch, "E325", {"start": v(-36.21, -23.46) * mm, "end": v(-35.8, -23.34) * mm});
            skLineSegment(sketch, "E326", {"start": v(-35.8, -23.34) * mm, "end": v(-35.52, -23.7) * mm});
            skLineSegment(sketch, "E327", {"start": v(-35.52, -23.7) * mm, "end": v(-35.26, -24.05) * mm});
            skLineSegment(sketch, "E328", {"start": v(-35.26, -24.05) * mm, "end": v(-34.99, -24.4) * mm});
            skLineSegment(sketch, "E329", {"start": v(-34.99, -24.4) * mm, "end": v(-34.72, -24.76) * mm});
            skLineSegment(sketch, "E330", {"start": v(-34.72, -24.76) * mm, "end": v(-34.45, -25.12) * mm});
            skLineSegment(sketch, "E331", {"start": v(-34.45, -25.12) * mm, "end": v(-34.18, -25.47) * mm});
            skLineSegment(sketch, "E332", {"start": v(-34.18, -25.47) * mm, "end": v(-33.9, -25.83) * mm});
            skLineSegment(sketch, "E333", {"start": v(-33.9, -25.83) * mm, "end": v(-33.64, -26.18) * mm});
            skLineSegment(sketch, "E334", {"start": v(-33.64, -26.18) * mm, "end": v(-33.37, -26.54) * mm});
            skLineSegment(sketch, "E335", {"start": v(-33.37, -26.54) * mm, "end": v(-33.1, -26.9) * mm});
            skLineSegment(sketch, "E336", {"start": v(-33.1, -26.9) * mm, "end": v(-32.83, -27.25) * mm});
            skLineSegment(sketch, "E337", {"start": v(-32.83, -27.25) * mm, "end": v(-32.56, -27.6) * mm});
            skLineSegment(sketch, "E338", {"start": v(-32.56, -27.6) * mm, "end": v(-32.29, -27.95) * mm});
            skLineSegment(sketch, "E339", {"start": v(-32.29, -27.95) * mm, "end": v(-32.08, -28.23) * mm});
            skLineSegment(sketch, "E340", {"start": v(-32.08, -28.23) * mm, "end": v(-32.43, -28.5) * mm});
            skLineSegment(sketch, "E341", {"start": v(-32.43, -28.5) * mm, "end": v(-32.78, -28.79) * mm});
            skLineSegment(sketch, "E342", {"start": v(-32.78, -28.79) * mm, "end": v(-33.12, -29.07) * mm});
            skLineSegment(sketch, "E343", {"start": v(-33.12, -29.07) * mm, "end": v(-33.47, -29.35) * mm});
            skLineSegment(sketch, "E344", {"start": v(-33.47, -29.35) * mm, "end": v(-33.82, -29.63) * mm});
            skLineSegment(sketch, "E345", {"start": v(-33.82, -29.63) * mm, "end": v(-34.16, -29.9) * mm});
            skLineSegment(sketch, "E346", {"start": v(-34.16, -29.9) * mm, "end": v(-34.5, -30.19) * mm});
            skLineSegment(sketch, "E347", {"start": v(-34.5, -30.19) * mm, "end": v(-34.85, -30.47) * mm});
            skLineSegment(sketch, "E348", {"start": v(-34.85, -30.47) * mm, "end": v(-35.2, -30.75) * mm});
            skLineSegment(sketch, "E349", {"start": v(-35.2, -30.75) * mm, "end": v(-35.55, -31.03) * mm});
            skLineSegment(sketch, "E350", {"start": v(-35.55, -31.03) * mm, "end": v(-35.9, -31.31) * mm});
            skLineSegment(sketch, "E351", {"start": v(-35.9, -31.31) * mm, "end": v(-36.24, -31.6) * mm});
            skLineSegment(sketch, "E352", {"start": v(-36.24, -31.6) * mm, "end": v(-36.59, -31.87) * mm});
            skLineSegment(sketch, "E353", {"start": v(-36.59, -31.87) * mm, "end": v(-36.93, -32.15) * mm});
            skLineSegment(sketch, "E354", {"start": v(-36.93, -32.15) * mm, "end": v(-37.28, -32.43) * mm});
            skLineSegment(sketch, "E355", {"start": v(-37.28, -32.43) * mm, "end": v(-37.62, -32.71) * mm});
            skLineSegment(sketch, "E356", {"start": v(-37.62, -32.71) * mm, "end": v(-37.74, -32.8) * mm});
            skLineSegment(sketch, "E357", {"start": v(-37.74, -32.8) * mm, "end": v(-37.44, -33.14) * mm});
            skLineSegment(sketch, "E358", {"start": v(-37.44, -33.14) * mm, "end": v(-37.14, -33.47) * mm});
            skLineSegment(sketch, "E359", {"start": v(-37.14, -33.47) * mm, "end": v(-36.86, -33.78) * mm});
            skLineSegment(sketch, "E360", {"start": v(-36.86, -33.78) * mm, "end": v(-36.47, -33.57) * mm});
            skLineSegment(sketch, "E361", {"start": v(-36.47, -33.57) * mm, "end": v(-36.07, -33.37) * mm});
            skLineSegment(sketch, "E362", {"start": v(-36.07, -33.37) * mm, "end": v(-35.68, -33.16) * mm});
            skLineSegment(sketch, "E363", {"start": v(-35.68, -33.16) * mm, "end": v(-35.28, -32.95) * mm});
            skLineSegment(sketch, "E364", {"start": v(-35.28, -32.95) * mm, "end": v(-34.89, -32.75) * mm});
            skLineSegment(sketch, "E365", {"start": v(-34.89, -32.75) * mm, "end": v(-34.5, -32.54) * mm});
            skLineSegment(sketch, "E366", {"start": v(-34.5, -32.54) * mm, "end": v(-34.1, -32.33) * mm});
            skLineSegment(sketch, "E367", {"start": v(-34.1, -32.33) * mm, "end": v(-33.7, -32.13) * mm});
            skLineSegment(sketch, "E368", {"start": v(-33.7, -32.13) * mm, "end": v(-33.3, -31.92) * mm});
            skLineSegment(sketch, "E369", {"start": v(-33.3, -31.92) * mm, "end": v(-32.91, -31.71) * mm});
            skLineSegment(sketch, "E370", {"start": v(-32.91, -31.71) * mm, "end": v(-32.52, -31.5) * mm});
            skLineSegment(sketch, "E371", {"start": v(-32.52, -31.5) * mm, "end": v(-32.12, -31.3) * mm});
            skLineSegment(sketch, "E372", {"start": v(-32.12, -31.3) * mm, "end": v(-31.73, -31.1) * mm});
            skLineSegment(sketch, "E373", {"start": v(-31.73, -31.1) * mm, "end": v(-31.34, -30.89) * mm});
            skLineSegment(sketch, "E374", {"start": v(-31.34, -30.89) * mm, "end": v(-30.94, -30.68) * mm});
            skLineSegment(sketch, "E375", {"start": v(-30.94, -30.68) * mm, "end": v(-30.55, -30.48) * mm});
            skLineSegment(sketch, "E376", {"start": v(-30.55, -30.48) * mm, "end": v(-30.16, -30.27) * mm});
            skLineSegment(sketch, "E377", {"start": v(-30.16, -30.27) * mm, "end": v(-29.82, -30.57) * mm});
            skLineSegment(sketch, "E378", {"start": v(-29.82, -30.57) * mm, "end": v(-29.48, -30.86) * mm});
            skLineSegment(sketch, "E379", {"start": v(-29.48, -30.86) * mm, "end": v(-29.15, -31.15) * mm});
            skLineSegment(sketch, "E380", {"start": v(-29.15, -31.15) * mm, "end": v(-28.8, -31.44) * mm});
            skLineSegment(sketch, "E381", {"start": v(-28.8, -31.44) * mm, "end": v(-28.47, -31.73) * mm});
            skLineSegment(sketch, "E382", {"start": v(-28.47, -31.73) * mm, "end": v(-28.13, -32.02) * mm});
            skLineSegment(sketch, "E383", {"start": v(-28.13, -32.02) * mm, "end": v(-27.8, -32.31) * mm});
            skLineSegment(sketch, "E384", {"start": v(-27.8, -32.31) * mm, "end": v(-27.46, -32.6) * mm});
            skLineSegment(sketch, "E385", {"start": v(-27.46, -32.6) * mm, "end": v(-27.12, -32.9) * mm});
            skLineSegment(sketch, "E386", {"start": v(-27.12, -32.9) * mm, "end": v(-26.78, -33.18) * mm});
            skLineSegment(sketch, "E387", {"start": v(-26.78, -33.18) * mm, "end": v(-26.45, -33.48) * mm});
            skLineSegment(sketch, "E388", {"start": v(-26.45, -33.48) * mm, "end": v(-26.1, -33.77) * mm});
            skLineSegment(sketch, "E389", {"start": v(-26.1, -33.77) * mm, "end": v(-25.77, -34.06) * mm});
            skLineSegment(sketch, "E390", {"start": v(-25.77, -34.06) * mm, "end": v(-25.51, -34.28) * mm});
            skLineSegment(sketch, "E391", {"start": v(-25.51, -34.28) * mm, "end": v(-25.8, -34.63) * mm});
            skLineSegment(sketch, "E392", {"start": v(-25.8, -34.63) * mm, "end": v(-26.07, -34.97) * mm});
            skLineSegment(sketch, "E393", {"start": v(-26.07, -34.97) * mm, "end": v(-26.36, -35.32) * mm});
            skLineSegment(sketch, "E394", {"start": v(-26.36, -35.32) * mm, "end": v(-26.64, -35.67) * mm});
            skLineSegment(sketch, "E395", {"start": v(-26.64, -35.67) * mm, "end": v(-26.92, -36.01) * mm});
            skLineSegment(sketch, "E396", {"start": v(-26.92, -36.01) * mm, "end": v(-27.2, -36.36) * mm});
            skLineSegment(sketch, "E397", {"start": v(-27.2, -36.36) * mm, "end": v(-27.48, -36.7) * mm});
            skLineSegment(sketch, "E398", {"start": v(-27.48, -36.7) * mm, "end": v(-27.76, -37.05) * mm});
            skLineSegment(sketch, "E399", {"start": v(-27.76, -37.05) * mm, "end": v(-28.04, -37.4) * mm});
            skLineSegment(sketch, "E400", {"start": v(-28.04, -37.4) * mm, "end": v(-28.32, -37.74) * mm});
            skLineSegment(sketch, "E401", {"start": v(-28.32, -37.74) * mm, "end": v(-28.6, -38.09) * mm});
            skLineSegment(sketch, "E402", {"start": v(-28.6, -38.09) * mm, "end": v(-28.88, -38.44) * mm});
            skLineSegment(sketch, "E403", {"start": v(-28.88, -38.44) * mm, "end": v(-29.16, -38.78) * mm});
            skLineSegment(sketch, "E404", {"start": v(-29.16, -38.78) * mm, "end": v(-29.44, -39.13) * mm});
            skLineSegment(sketch, "E405", {"start": v(-29.44, -39.13) * mm, "end": v(-29.72, -39.47) * mm});
            skLineSegment(sketch, "E406", {"start": v(-29.72, -39.47) * mm, "end": v(-30, -39.82) * mm});
            skLineSegment(sketch, "E407", {"start": v(-30, -39.82) * mm, "end": v(-30.1, -39.93) * mm});
            skLineSegment(sketch, "E408", {"start": v(-30.1, -39.93) * mm, "end": v(-29.73, -40.2) * mm});
            skLineSegment(sketch, "E409", {"start": v(-29.73, -40.2) * mm, "end": v(-29.37, -40.46) * mm});
            skLineSegment(sketch, "E410", {"start": v(-29.37, -40.46) * mm, "end": v(-29.04, -40.7) * mm});
            skLineSegment(sketch, "E411", {"start": v(-29.04, -40.7) * mm, "end": v(-28.7, -40.42) * mm});
            skLineSegment(sketch, "E412", {"start": v(-28.7, -40.42) * mm, "end": v(-28.35, -40.14) * mm});
            skLineSegment(sketch, "E413", {"start": v(-28.35, -40.14) * mm, "end": v(-28, -39.85) * mm});
            skLineSegment(sketch, "E414", {"start": v(-28, -39.85) * mm, "end": v(-27.66, -39.57) * mm});
            skLineSegment(sketch, "E415", {"start": v(-27.66, -39.57) * mm, "end": v(-27.32, -39.29) * mm});
            skLineSegment(sketch, "E416", {"start": v(-27.32, -39.29) * mm, "end": v(-26.98, -39) * mm});
            skLineSegment(sketch, "E417", {"start": v(-26.98, -39) * mm, "end": v(-26.63, -38.72) * mm});
            skLineSegment(sketch, "E418", {"start": v(-26.63, -38.72) * mm, "end": v(-26.29, -38.43) * mm});
            skLineSegment(sketch, "E419", {"start": v(-26.29, -38.43) * mm, "end": v(-25.94, -38.15) * mm});
            skLineSegment(sketch, "E420", {"start": v(-25.94, -38.15) * mm, "end": v(-25.6, -37.87) * mm});
            skLineSegment(sketch, "E421", {"start": v(-25.6, -37.87) * mm, "end": v(-25.26, -37.58) * mm});
            skLineSegment(sketch, "E422", {"start": v(-25.26, -37.58) * mm, "end": v(-24.91, -37.3) * mm});
            skLineSegment(sketch, "E423", {"start": v(-24.91, -37.3) * mm, "end": v(-24.57, -37.01) * mm});
            skLineSegment(sketch, "E424", {"start": v(-24.57, -37.01) * mm, "end": v(-24.23, -36.73) * mm});
            skLineSegment(sketch, "E425", {"start": v(-24.23, -36.73) * mm, "end": v(-23.88, -36.44) * mm});
            skLineSegment(sketch, "E426", {"start": v(-23.88, -36.44) * mm, "end": v(-23.54, -36.16) * mm});
            skLineSegment(sketch, "E427", {"start": v(-23.54, -36.16) * mm, "end": v(-23.2, -35.88) * mm});
            skLineSegment(sketch, "E428", {"start": v(-23.2, -35.88) * mm, "end": v(-22.82, -36.1) * mm});
            skLineSegment(sketch, "E429", {"start": v(-22.82, -36.1) * mm, "end": v(-22.42, -36.31) * mm});
            skLineSegment(sketch, "E430", {"start": v(-22.42, -36.31) * mm, "end": v(-22.03, -36.53) * mm});
            skLineSegment(sketch, "E431", {"start": v(-22.03, -36.53) * mm, "end": v(-21.64, -36.74) * mm});
            skLineSegment(sketch, "E432", {"start": v(-21.64, -36.74) * mm, "end": v(-21.25, -36.96) * mm});
            skLineSegment(sketch, "E433", {"start": v(-21.25, -36.96) * mm, "end": v(-20.86, -37.17) * mm});
            skLineSegment(sketch, "E434", {"start": v(-20.86, -37.17) * mm, "end": v(-20.47, -37.38) * mm});
            skLineSegment(sketch, "E435", {"start": v(-20.47, -37.38) * mm, "end": v(-20.08, -37.6) * mm});
            skLineSegment(sketch, "E436", {"start": v(-20.08, -37.6) * mm, "end": v(-19.7, -37.81) * mm});
            skLineSegment(sketch, "E437", {"start": v(-19.7, -37.81) * mm, "end": v(-19.3, -38.03) * mm});
            skLineSegment(sketch, "E438", {"start": v(-19.3, -38.03) * mm, "end": v(-18.9, -38.24) * mm});
            skLineSegment(sketch, "E439", {"start": v(-18.9, -38.24) * mm, "end": v(-18.52, -38.46) * mm});
            skLineSegment(sketch, "E440", {"start": v(-18.52, -38.46) * mm, "end": v(-18.13, -38.67) * mm});
            skLineSegment(sketch, "E441", {"start": v(-18.13, -38.67) * mm, "end": v(-17.83, -38.84) * mm});
            skLineSegment(sketch, "E442", {"start": v(-17.83, -38.84) * mm, "end": v(-18.03, -39.23) * mm});
            skLineSegment(sketch, "E443", {"start": v(-18.03, -39.23) * mm, "end": v(-18.23, -39.63) * mm});
            skLineSegment(sketch, "E444", {"start": v(-18.23, -39.63) * mm, "end": v(-18.44, -40.03) * mm});
            skLineSegment(sketch, "E445", {"start": v(-18.44, -40.03) * mm, "end": v(-18.64, -40.42) * mm});
            skLineSegment(sketch, "E446", {"start": v(-18.64, -40.42) * mm, "end": v(-18.84, -40.82) * mm});
            skLineSegment(sketch, "E447", {"start": v(-18.84, -40.82) * mm, "end": v(-19.04, -41.22) * mm});
            skLineSegment(sketch, "E448", {"start": v(-19.04, -41.22) * mm, "end": v(-19.25, -41.61) * mm});
            skLineSegment(sketch, "E449", {"start": v(-19.25, -41.61) * mm, "end": v(-19.45, -42.01) * mm});
            skLineSegment(sketch, "E450", {"start": v(-19.45, -42.01) * mm, "end": v(-19.65, -42.4) * mm});
            skLineSegment(sketch, "E451", {"start": v(-19.65, -42.4) * mm, "end": v(-19.85, -42.8) * mm});
            skLineSegment(sketch, "E452", {"start": v(-19.85, -42.8) * mm, "end": v(-20.05, -43.2) * mm});
            skLineSegment(sketch, "E453", {"start": v(-20.05, -43.2) * mm, "end": v(-20.26, -43.6) * mm});
            skLineSegment(sketch, "E454", {"start": v(-20.26, -43.6) * mm, "end": v(-20.46, -44) * mm});
            skLineSegment(sketch, "E455", {"start": v(-20.46, -44) * mm, "end": v(-20.66, -44.4) * mm});
            skLineSegment(sketch, "E456", {"start": v(-20.66, -44.4) * mm, "end": v(-20.86, -44.8) * mm});
            skLineSegment(sketch, "E457", {"start": v(-20.86, -44.8) * mm, "end": v(-21.07, -45.19) * mm});
            skLineSegment(sketch, "E458", {"start": v(-21.07, -45.19) * mm, "end": v(-21.13, -45.32) * mm});
            skLineSegment(sketch, "E459", {"start": v(-21.13, -45.32) * mm, "end": v(-20.72, -45.5) * mm});
            skLineSegment(sketch, "E460", {"start": v(-20.72, -45.5) * mm, "end": v(-20.32, -45.68) * mm});
            skLineSegment(sketch, "E461", {"start": v(-20.32, -45.68) * mm, "end": v(-19.94, -45.85) * mm});
            skLineSegment(sketch, "E462", {"start": v(-19.94, -45.85) * mm, "end": v(-19.66, -45.5) * mm});
            skLineSegment(sketch, "E463", {"start": v(-19.66, -45.5) * mm, "end": v(-19.38, -45.15) * mm});
            skLineSegment(sketch, "E464", {"start": v(-19.38, -45.15) * mm, "end": v(-19.1, -44.8) * mm});
            skLineSegment(sketch, "E465", {"start": v(-19.1, -44.8) * mm, "end": v(-18.83, -44.46) * mm});
            skLineSegment(sketch, "E466", {"start": v(-18.83, -44.46) * mm, "end": v(-18.55, -44.1) * mm});
            skLineSegment(sketch, "E467", {"start": v(-18.55, -44.1) * mm, "end": v(-18.28, -43.76) * mm});
            skLineSegment(sketch, "E468", {"start": v(-18.28, -43.76) * mm, "end": v(-18, -43.4) * mm});
            skLineSegment(sketch, "E469", {"start": v(-18, -43.4) * mm, "end": v(-17.72, -43.06) * mm});
            skLineSegment(sketch, "E470", {"start": v(-17.72, -43.06) * mm, "end": v(-17.45, -42.7) * mm});
            skLineSegment(sketch, "E471", {"start": v(-17.45, -42.7) * mm, "end": v(-17.17, -42.36) * mm});
            skLineSegment(sketch, "E472", {"start": v(-17.17, -42.36) * mm, "end": v(-16.9, -42.01) * mm});
            skLineSegment(sketch, "E473", {"start": v(-16.9, -42.01) * mm, "end": v(-16.62, -41.66) * mm});
            skLineSegment(sketch, "E474", {"start": v(-16.62, -41.66) * mm, "end": v(-16.34, -41.31) * mm});
            skLineSegment(sketch, "E475", {"start": v(-16.34, -41.31) * mm, "end": v(-16.06, -40.96) * mm});
            skLineSegment(sketch, "E476", {"start": v(-16.06, -40.96) * mm, "end": v(-15.79, -40.61) * mm});
            skLineSegment(sketch, "E477", {"start": v(-15.79, -40.61) * mm, "end": v(-15.5, -40.27) * mm});
            skLineSegment(sketch, "E478", {"start": v(-15.5, -40.27) * mm, "end": v(-15.24, -39.92) * mm});
            skLineSegment(sketch, "E479", {"start": v(-15.24, -39.92) * mm, "end": v(-14.81, -40.05) * mm});
            skLineSegment(sketch, "E480", {"start": v(-14.81, -40.05) * mm, "end": v(-14.38, -40.18) * mm});
            skLineSegment(sketch, "E481", {"start": v(-14.38, -40.18) * mm, "end": v(-13.96, -40.3) * mm});
            skLineSegment(sketch, "E482", {"start": v(-13.96, -40.3) * mm, "end": v(-13.53, -40.44) * mm});
            skLineSegment(sketch, "E483", {"start": v(-13.53, -40.44) * mm, "end": v(-13.1, -40.57) * mm});
            skLineSegment(sketch, "E484", {"start": v(-13.1, -40.57) * mm, "end": v(-12.68, -40.7) * mm});
            skLineSegment(sketch, "E485", {"start": v(-12.68, -40.7) * mm, "end": v(-12.25, -40.82) * mm});
            skLineSegment(sketch, "E486", {"start": v(-12.25, -40.82) * mm, "end": v(-11.82, -40.95) * mm});
            skLineSegment(sketch, "E487", {"start": v(-11.82, -40.95) * mm, "end": v(-11.4, -41.08) * mm});
            skLineSegment(sketch, "E488", {"start": v(-11.4, -41.08) * mm, "end": v(-10.97, -41.2) * mm});
            skLineSegment(sketch, "E489", {"start": v(-10.97, -41.2) * mm, "end": v(-10.54, -41.34) * mm});
            skLineSegment(sketch, "E490", {"start": v(-10.54, -41.34) * mm, "end": v(-10.12, -41.47) * mm});
            skLineSegment(sketch, "E491", {"start": v(-10.12, -41.47) * mm, "end": v(-9.7, -41.6) * mm});
            skLineSegment(sketch, "E492", {"start": v(-9.7, -41.6) * mm, "end": v(-9.37, -41.7) * mm});
            skLineSegment(sketch, "E493", {"start": v(-9.37, -41.7) * mm, "end": v(-9.48, -42.12) * mm});
            skLineSegment(sketch, "E494", {"start": v(-9.48, -42.12) * mm, "end": v(-9.6, -42.55) * mm});
            skLineSegment(sketch, "E495", {"start": v(-9.6, -42.55) * mm, "end": v(-9.71, -42.99) * mm});
            skLineSegment(sketch, "E496", {"start": v(-9.71, -42.99) * mm, "end": v(-9.83, -43.42) * mm});
            skLineSegment(sketch, "E497", {"start": v(-9.83, -43.42) * mm, "end": v(-9.94, -43.85) * mm});
            skLineSegment(sketch, "E498", {"start": v(-9.94, -43.85) * mm, "end": v(-10.06, -44.28) * mm});
            skLineSegment(sketch, "E499", {"start": v(-10.06, -44.28) * mm, "end": v(-10.17, -44.7) * mm});
            skLineSegment(sketch, "E500", {"start": v(-10.17, -44.7) * mm, "end": v(-10.29, -45.14) * mm});
            skLineSegment(sketch, "E501", {"start": v(-10.29, -45.14) * mm, "end": v(-10.4, -45.57) * mm});
            skLineSegment(sketch, "E502", {"start": v(-10.4, -45.57) * mm, "end": v(-10.52, -46) * mm});
            skLineSegment(sketch, "E503", {"start": v(-10.52, -46) * mm, "end": v(-10.63, -46.43) * mm});
            skLineSegment(sketch, "E504", {"start": v(-10.63, -46.43) * mm, "end": v(-10.75, -46.86) * mm});
            skLineSegment(sketch, "E505", {"start": v(-10.75, -46.86) * mm, "end": v(-10.86, -47.29) * mm});
            skLineSegment(sketch, "E506", {"start": v(-10.86, -47.29) * mm, "end": v(-10.98, -47.72) * mm});
            skLineSegment(sketch, "E507", {"start": v(-10.98, -47.72) * mm, "end": v(-11.1, -48.15) * mm});
            skLineSegment(sketch, "E508", {"start": v(-11.1, -48.15) * mm, "end": v(-11.21, -48.58) * mm});
            skLineSegment(sketch, "E509", {"start": v(-11.21, -48.58) * mm, "end": v(-11.25, -48.72) * mm});
            skLineSegment(sketch, "E510", {"start": v(-11.25, -48.72) * mm, "end": v(-10.81, -48.81) * mm});
            skLineSegment(sketch, "E511", {"start": v(-10.81, -48.81) * mm, "end": v(-10.38, -48.9) * mm});
            skLineSegment(sketch, "E512", {"start": v(-10.38, -48.9) * mm, "end": v(-9.97, -49) * mm});
            skLineSegment(sketch, "E513", {"start": v(-9.97, -49) * mm, "end": v(-9.77, -48.6) * mm});
            skLineSegment(sketch, "E514", {"start": v(-9.77, -48.6) * mm, "end": v(-9.57, -48.2) * mm});
            skLineSegment(sketch, "E515", {"start": v(-9.57, -48.2) * mm, "end": v(-9.37, -47.8) * mm});
            skLineSegment(sketch, "E516", {"start": v(-9.37, -47.8) * mm, "end": v(-9.18, -47.4) * mm});
            skLineSegment(sketch, "E517", {"start": v(-9.18, -47.4) * mm, "end": v(-8.98, -47) * mm});
            skLineSegment(sketch, "E518", {"start": v(-8.98, -47) * mm, "end": v(-8.78, -46.6) * mm});
            skLineSegment(sketch, "E519", {"start": v(-8.78, -46.6) * mm, "end": v(-8.58, -46.2) * mm});
            skLineSegment(sketch, "E520", {"start": v(-8.58, -46.2) * mm, "end": v(-8.38, -45.8) * mm});
            skLineSegment(sketch, "E521", {"start": v(-8.38, -45.8) * mm, "end": v(-8.19, -45.4) * mm});
            skLineSegment(sketch, "E522", {"start": v(-8.19, -45.4) * mm, "end": v(-7.99, -45) * mm});
            skLineSegment(sketch, "E523", {"start": v(-7.99, -45) * mm, "end": v(-7.79, -44.6) * mm});
            skLineSegment(sketch, "E524", {"start": v(-7.79, -44.6) * mm, "end": v(-7.6, -44.2) * mm});
            skLineSegment(sketch, "E525", {"start": v(-7.6, -44.2) * mm, "end": v(-7.4, -43.8) * mm});
            skLineSegment(sketch, "E526", {"start": v(-7.4, -43.8) * mm, "end": v(-7.2, -43.4) * mm});
            skLineSegment(sketch, "E527", {"start": v(-7.2, -43.4) * mm, "end": v(-7, -43) * mm});
            skLineSegment(sketch, "E528", {"start": v(-7, -43) * mm, "end": v(-6.8, -42.6) * mm});
            skLineSegment(sketch, "E529", {"start": v(-6.8, -42.6) * mm, "end": v(-6.6, -42.22) * mm});
            skLineSegment(sketch, "E530", {"start": v(-6.6, -42.22) * mm, "end": v(-6.16, -42.26) * mm});
            skLineSegment(sketch, "E531", {"start": v(-6.16, -42.26) * mm, "end": v(-5.72, -42.3) * mm});
            skLineSegment(sketch, "E532", {"start": v(-5.72, -42.3) * mm, "end": v(-5.27, -42.33) * mm});
            skLineSegment(sketch, "E533", {"start": v(-5.27, -42.33) * mm, "end": v(-4.83, -42.37) * mm});
            skLineSegment(sketch, "E534", {"start": v(-4.83, -42.37) * mm, "end": v(-4.38, -42.4) * mm});
            skLineSegment(sketch, "E535", {"start": v(-4.38, -42.4) * mm, "end": v(-3.94, -42.44) * mm});
            skLineSegment(sketch, "E536", {"start": v(-3.94, -42.44) * mm, "end": v(-3.5, -42.48) * mm});
            skLineSegment(sketch, "E537", {"start": v(-3.5, -42.48) * mm, "end": v(-3.05, -42.52) * mm});
            skLineSegment(sketch, "E538", {"start": v(-3.05, -42.52) * mm, "end": v(-2.6, -42.55) * mm});
            skLineSegment(sketch, "E539", {"start": v(-2.6, -42.55) * mm, "end": v(-2.16, -42.6) * mm});
            skLineSegment(sketch, "E540", {"start": v(-2.16, -42.6) * mm, "end": v(-1.72, -42.63) * mm});
            skLineSegment(sketch, "E541", {"start": v(-1.72, -42.63) * mm, "end": v(-1.28, -42.66) * mm});
            skLineSegment(sketch, "E542", {"start": v(-1.28, -42.66) * mm, "end": v(-0.83, -42.7) * mm});
            skLineSegment(sketch, "E543", {"start": v(-0.83, -42.7) * mm, "end": v(-0.5, -42.73) * mm});
            skLineSegment(sketch, "E544", {"start": v(-0.5, -42.73) * mm, "end": v(-0.52, -43.17) * mm});
            skLineSegment(sketch, "E545", {"start": v(-0.52, -43.17) * mm, "end": v(-0.54, -43.62) * mm});
            skLineSegment(sketch, "E546", {"start": v(-0.54, -43.62) * mm, "end": v(-0.56, -44.06) * mm});
            skLineSegment(sketch, "E547", {"start": v(-0.56, -44.06) * mm, "end": v(-0.59, -44.5) * mm});
            skLineSegment(sketch, "E548", {"start": v(-0.59, -44.5) * mm, "end": v(-0.6, -44.95) * mm});
            skLineSegment(sketch, "E549", {"start": v(-0.6, -44.95) * mm, "end": v(-0.63, -45.4) * mm});
            skLineSegment(sketch, "E550", {"start": v(-0.63, -45.4) * mm, "end": v(-0.66, -45.84) * mm});
            skLineSegment(sketch, "E551", {"start": v(-0.66, -45.84) * mm, "end": v(-0.68, -46.29) * mm});
            skLineSegment(sketch, "E552", {"start": v(-0.68, -46.29) * mm, "end": v(-0.7, -46.73) * mm});
            skLineSegment(sketch, "E553", {"start": v(-0.7, -46.73) * mm, "end": v(-0.73, -47.18) * mm});
            skLineSegment(sketch, "E554", {"start": v(-0.73, -47.18) * mm, "end": v(-0.75, -47.62) * mm});
            skLineSegment(sketch, "E555", {"start": v(-0.75, -47.62) * mm, "end": v(-0.77, -48.07) * mm});
            skLineSegment(sketch, "E556", {"start": v(-0.77, -48.07) * mm, "end": v(-0.8, -48.52) * mm});
            skLineSegment(sketch, "E557", {"start": v(-0.8, -48.52) * mm, "end": v(-0.82, -48.96) * mm});
            skLineSegment(sketch, "E558", {"start": v(-0.82, -48.96) * mm, "end": v(-0.84, -49.4) * mm});
            skLineSegment(sketch, "E559", {"start": v(-0.84, -49.4) * mm, "end": v(-0.87, -49.85) * mm});
            skLineSegment(sketch, "E560", {"start": v(-0.87, -49.85) * mm, "end": v(-0.87, -50) * mm});
            skLineSegment(sketch, "E561", {"start": v(-0.87, -50) * mm, "end": v(-0.43, -50) * mm});
            skLineSegment(sketch, "E562", {"start": v(-0.43, -50) * mm, "end": v(0.02, -50) * mm});
            skLineSegment(sketch, "E563", {"start": v(0.02, -50) * mm, "end": v(0.44, -50) * mm});
            skLineSegment(sketch, "E564", {"start": v(0.44, -50) * mm, "end": v(0.55, -49.57) * mm});
            skLineSegment(sketch, "E565", {"start": v(0.55, -49.57) * mm, "end": v(0.66, -49.13) * mm});
            skLineSegment(sketch, "E566", {"start": v(0.66, -49.13) * mm, "end": v(0.77, -48.7) * mm});
            skLineSegment(sketch, "E567", {"start": v(0.77, -48.7) * mm, "end": v(0.88, -48.27) * mm});
            skLineSegment(sketch, "E568", {"start": v(0.88, -48.27) * mm, "end": v(1, -47.84) * mm});
            skLineSegment(sketch, "E569", {"start": v(1, -47.84) * mm, "end": v(1.1, -47.4) * mm});
            skLineSegment(sketch, "E570", {"start": v(1.1, -47.4) * mm, "end": v(1.21, -46.98) * mm});
            skLineSegment(sketch, "E571", {"start": v(1.21, -46.98) * mm, "end": v(1.32, -46.55) * mm});
            skLineSegment(sketch, "E572", {"start": v(1.32, -46.55) * mm, "end": v(1.43, -46.11) * mm});
            skLineSegment(sketch, "E573", {"start": v(1.43, -46.11) * mm, "end": v(1.54, -45.68) * mm});
            skLineSegment(sketch, "E574", {"start": v(1.54, -45.68) * mm, "end": v(1.66, -45.25) * mm});
            skLineSegment(sketch, "E575", {"start": v(1.66, -45.25) * mm, "end": v(1.77, -44.82) * mm});
            skLineSegment(sketch, "E576", {"start": v(1.77, -44.82) * mm, "end": v(1.88, -44.39) * mm});
            skLineSegment(sketch, "E577", {"start": v(1.88, -44.39) * mm, "end": v(1.99, -43.96) * mm});
            skLineSegment(sketch, "E578", {"start": v(1.99, -43.96) * mm, "end": v(2.1, -43.52) * mm});
            skLineSegment(sketch, "E579", {"start": v(2.1, -43.52) * mm, "end": v(2.2, -43.1) * mm});
            skLineSegment(sketch, "E580", {"start": v(2.2, -43.1) * mm, "end": v(2.32, -42.67) * mm});
            skLineSegment(sketch, "E581", {"start": v(2.32, -42.67) * mm, "end": v(2.76, -42.61) * mm});
            skLineSegment(sketch, "E582", {"start": v(2.76, -42.61) * mm, "end": v(3.2, -42.56) * mm});
            skLineSegment(sketch, "E583", {"start": v(3.2, -42.56) * mm, "end": v(3.64, -42.5) * mm});
            skLineSegment(sketch, "E584", {"start": v(3.64, -42.5) * mm, "end": v(4.09, -42.45) * mm});
            skLineSegment(sketch, "E585", {"start": v(4.09, -42.45) * mm, "end": v(4.53, -42.39) * mm});
            skLineSegment(sketch, "E586", {"start": v(4.53, -42.39) * mm, "end": v(4.97, -42.33) * mm});
            skLineSegment(sketch, "E587", {"start": v(4.97, -42.33) * mm, "end": v(5.41, -42.28) * mm});
            skLineSegment(sketch, "E588", {"start": v(5.41, -42.28) * mm, "end": v(5.85, -42.22) * mm});
            skLineSegment(sketch, "E589", {"start": v(5.85, -42.22) * mm, "end": v(6.3, -42.17) * mm});
            skLineSegment(sketch, "E590", {"start": v(6.3, -42.17) * mm, "end": v(6.74, -42.1) * mm});
            skLineSegment(sketch, "E591", {"start": v(6.74, -42.1) * mm, "end": v(7.18, -42.05) * mm});
            skLineSegment(sketch, "E592", {"start": v(7.18, -42.05) * mm, "end": v(7.62, -42) * mm});
            skLineSegment(sketch, "E593", {"start": v(7.62, -42) * mm, "end": v(8.06, -41.94) * mm});
            skLineSegment(sketch, "E594", {"start": v(8.06, -41.94) * mm, "end": v(8.4, -41.9) * mm});
            skLineSegment(sketch, "E595", {"start": v(8.4, -41.9) * mm, "end": v(8.47, -42.34) * mm});
            skLineSegment(sketch, "E596", {"start": v(8.47, -42.34) * mm, "end": v(8.54, -42.78) * mm});
            skLineSegment(sketch, "E597", {"start": v(8.54, -42.78) * mm, "end": v(8.61, -43.22) * mm});
            skLineSegment(sketch, "E598", {"start": v(8.61, -43.22) * mm, "end": v(8.68, -43.66) * mm});
            skLineSegment(sketch, "E599", {"start": v(8.68, -43.66) * mm, "end": v(8.75, -44.1) * mm});
            skLineSegment(sketch, "E600", {"start": v(8.75, -44.1) * mm, "end": v(8.82, -44.54) * mm});
            skLineSegment(sketch, "E601", {"start": v(8.82, -44.54) * mm, "end": v(8.9, -44.98) * mm});
            skLineSegment(sketch, "E602", {"start": v(8.9, -44.98) * mm, "end": v(8.96, -45.42) * mm});
            skLineSegment(sketch, "E603", {"start": v(8.96, -45.42) * mm, "end": v(9.03, -45.86) * mm});
            skLineSegment(sketch, "E604", {"start": v(9.03, -45.86) * mm, "end": v(9.1, -46.3) * mm});
            skLineSegment(sketch, "E605", {"start": v(9.1, -46.3) * mm, "end": v(9.17, -46.74) * mm});
            skLineSegment(sketch, "E606", {"start": v(9.17, -46.74) * mm, "end": v(9.24, -47.18) * mm});
            skLineSegment(sketch, "E607", {"start": v(9.24, -47.18) * mm, "end": v(9.3, -47.62) * mm});
            skLineSegment(sketch, "E608", {"start": v(9.3, -47.62) * mm, "end": v(9.38, -48.06) * mm});
            skLineSegment(sketch, "E609", {"start": v(9.38, -48.06) * mm, "end": v(9.45, -48.5) * mm});
            skLineSegment(sketch, "E610", {"start": v(9.45, -48.5) * mm, "end": v(9.52, -48.94) * mm});
            skLineSegment(sketch, "E611", {"start": v(9.52, -48.94) * mm, "end": v(9.54, -49.08) * mm});
            skLineSegment(sketch, "E612", {"start": v(9.54, -49.08) * mm, "end": v(9.98, -49) * mm});
            skLineSegment(sketch, "E613", {"start": v(9.98, -49) * mm, "end": v(10.41, -48.9) * mm});
            skLineSegment(sketch, "E614", {"start": v(10.41, -48.9) * mm, "end": v(10.82, -48.81) * mm});
            skLineSegment(sketch, "E615", {"start": v(10.82, -48.81) * mm, "end": v(10.84, -48.37) * mm});
            skLineSegment(sketch, "E616", {"start": v(10.84, -48.37) * mm, "end": v(10.86, -47.92) * mm});
            skLineSegment(sketch, "E617", {"start": v(10.86, -47.92) * mm, "end": v(10.88, -47.48) * mm});
            skLineSegment(sketch, "E618", {"start": v(10.88, -47.48) * mm, "end": v(10.9, -47.03) * mm});
            skLineSegment(sketch, "E619", {"start": v(10.9, -47.03) * mm, "end": v(10.92, -46.59) * mm});
            skLineSegment(sketch, "E620", {"start": v(10.92, -46.59) * mm, "end": v(10.93, -46.14) * mm});
            skLineSegment(sketch, "E621", {"start": v(10.93, -46.14) * mm, "end": v(10.95, -45.7) * mm});
            skLineSegment(sketch, "E622", {"start": v(10.95, -45.7) * mm, "end": v(10.97, -45.25) * mm});
            skLineSegment(sketch, "E623", {"start": v(10.97, -45.25) * mm, "end": v(10.99, -44.8) * mm});
            skLineSegment(sketch, "E624", {"start": v(10.99, -44.8) * mm, "end": v(11, -44.36) * mm});
            skLineSegment(sketch, "E625", {"start": v(11, -44.36) * mm, "end": v(11.03, -43.92) * mm});
            skLineSegment(sketch, "E626", {"start": v(11.03, -43.92) * mm, "end": v(11.05, -43.47) * mm});
            skLineSegment(sketch, "E627", {"start": v(11.05, -43.47) * mm, "end": v(11.06, -43.03) * mm});
            skLineSegment(sketch, "E628", {"start": v(11.06, -43.03) * mm, "end": v(11.08, -42.58) * mm});
            skLineSegment(sketch, "E629", {"start": v(11.08, -42.58) * mm, "end": v(11.1, -42.14) * mm});
            skLineSegment(sketch, "E630", {"start": v(11.1, -42.14) * mm, "end": v(11.12, -41.7) * mm});
            skLineSegment(sketch, "E631", {"start": v(11.12, -41.7) * mm, "end": v(11.14, -41.26) * mm});
            skLineSegment(sketch, "E632", {"start": v(11.14, -41.26) * mm, "end": v(11.56, -41.1) * mm});
            skLineSegment(sketch, "E633", {"start": v(11.56, -41.1) * mm, "end": v(11.98, -40.96) * mm});
            skLineSegment(sketch, "E634", {"start": v(11.98, -40.96) * mm, "end": v(12.4, -40.82) * mm});
            skLineSegment(sketch, "E635", {"start": v(12.4, -40.82) * mm, "end": v(12.82, -40.67) * mm});
            skLineSegment(sketch, "E636", {"start": v(12.82, -40.67) * mm, "end": v(13.24, -40.52) * mm});
            skLineSegment(sketch, "E637", {"start": v(13.24, -40.52) * mm, "end": v(13.66, -40.38) * mm});
            skLineSegment(sketch, "E638", {"start": v(13.66, -40.38) * mm, "end": v(14.08, -40.23) * mm});
            skLineSegment(sketch, "E639", {"start": v(14.08, -40.23) * mm, "end": v(14.5, -40.08) * mm});
            skLineSegment(sketch, "E640", {"start": v(14.5, -40.08) * mm, "end": v(14.93, -39.93) * mm});
            skLineSegment(sketch, "E641", {"start": v(14.93, -39.93) * mm, "end": v(15.35, -39.79) * mm});
            skLineSegment(sketch, "E642", {"start": v(15.35, -39.79) * mm, "end": v(15.77, -39.64) * mm});
            skLineSegment(sketch, "E643", {"start": v(15.77, -39.64) * mm, "end": v(16.19, -39.5) * mm});
            skLineSegment(sketch, "E644", {"start": v(16.19, -39.5) * mm, "end": v(16.6, -39.35) * mm});
            skLineSegment(sketch, "E645", {"start": v(16.6, -39.35) * mm, "end": v(16.93, -39.24) * mm});
            skLineSegment(sketch, "E646", {"start": v(16.93, -39.24) * mm, "end": v(17.09, -39.65) * mm});
            skLineSegment(sketch, "E647", {"start": v(17.09, -39.65) * mm, "end": v(17.25, -40.07) * mm});
            skLineSegment(sketch, "E648", {"start": v(17.25, -40.07) * mm, "end": v(17.4, -40.48) * mm});
            skLineSegment(sketch, "E649", {"start": v(17.4, -40.48) * mm, "end": v(17.57, -40.9) * mm});
            skLineSegment(sketch, "E650", {"start": v(17.57, -40.9) * mm, "end": v(17.73, -41.32) * mm});
            skLineSegment(sketch, "E651", {"start": v(17.73, -41.32) * mm, "end": v(17.89, -41.73) * mm});
            skLineSegment(sketch, "E652", {"start": v(17.89, -41.73) * mm, "end": v(18.05, -42.15) * mm});
            skLineSegment(sketch, "E653", {"start": v(18.05, -42.15) * mm, "end": v(18.2, -42.56) * mm});
            skLineSegment(sketch, "E654", {"start": v(18.2, -42.56) * mm, "end": v(18.37, -42.98) * mm});
            skLineSegment(sketch, "E655", {"start": v(18.37, -42.98) * mm, "end": v(18.53, -43.4) * mm});
            skLineSegment(sketch, "E656", {"start": v(18.53, -43.4) * mm, "end": v(18.69, -43.81) * mm});
            skLineSegment(sketch, "E657", {"start": v(18.69, -43.81) * mm, "end": v(18.85, -44.23) * mm});
            skLineSegment(sketch, "E658", {"start": v(18.85, -44.23) * mm, "end": v(19, -44.64) * mm});
            skLineSegment(sketch, "E659", {"start": v(19, -44.64) * mm, "end": v(19.17, -45.06) * mm});
            skLineSegment(sketch, "E660", {"start": v(19.17, -45.06) * mm, "end": v(19.33, -45.48) * mm});
            skLineSegment(sketch, "E661", {"start": v(19.33, -45.48) * mm, "end": v(19.49, -45.9) * mm});
            skLineSegment(sketch, "E662", {"start": v(19.49, -45.9) * mm, "end": v(19.54, -46.03) * mm});
            skLineSegment(sketch, "E663", {"start": v(19.54, -46.03) * mm, "end": v(19.94, -45.85) * mm});
            skLineSegment(sketch, "E664", {"start": v(19.94, -45.85) * mm, "end": v(20.35, -45.67) * mm});
            skLineSegment(sketch, "E665", {"start": v(20.35, -45.67) * mm, "end": v(20.73, -45.5) * mm});
            skLineSegment(sketch, "E666", {"start": v(20.73, -45.5) * mm, "end": v(20.66, -45.06) * mm});
            skLineSegment(sketch, "E667", {"start": v(20.66, -45.06) * mm, "end": v(20.59, -44.62) * mm});
            skLineSegment(sketch, "E668", {"start": v(20.59, -44.62) * mm, "end": v(20.51, -44.18) * mm});
            skLineSegment(sketch, "E669", {"start": v(20.51, -44.18) * mm, "end": v(20.44, -43.74) * mm});
            skLineSegment(sketch, "E670", {"start": v(20.44, -43.74) * mm, "end": v(20.36, -43.3) * mm});
            skLineSegment(sketch, "E671", {"start": v(20.36, -43.3) * mm, "end": v(20.29, -42.86) * mm});
            skLineSegment(sketch, "E672", {"start": v(20.29, -42.86) * mm, "end": v(20.21, -42.42) * mm});
            skLineSegment(sketch, "E673", {"start": v(20.21, -42.42) * mm, "end": v(20.14, -41.98) * mm});
            skLineSegment(sketch, "E674", {"start": v(20.14, -41.98) * mm, "end": v(20.07, -41.54) * mm});
            skLineSegment(sketch, "E675", {"start": v(20.07, -41.54) * mm, "end": v(20, -41.1) * mm});
            skLineSegment(sketch, "E676", {"start": v(20, -41.1) * mm, "end": v(19.92, -40.66) * mm});
            skLineSegment(sketch, "E677", {"start": v(19.92, -40.66) * mm, "end": v(19.84, -40.23) * mm});
            skLineSegment(sketch, "E678", {"start": v(19.84, -40.23) * mm, "end": v(19.77, -39.79) * mm});
            skLineSegment(sketch, "E679", {"start": v(19.77, -39.79) * mm, "end": v(19.7, -39.35) * mm});
            skLineSegment(sketch, "E680", {"start": v(19.7, -39.35) * mm, "end": v(19.62, -38.9) * mm});
            skLineSegment(sketch, "E681", {"start": v(19.62, -38.9) * mm, "end": v(19.55, -38.47) * mm});
            skLineSegment(sketch, "E682", {"start": v(19.55, -38.47) * mm, "end": v(19.47, -38.04) * mm});
            skLineSegment(sketch, "E683", {"start": v(19.47, -38.04) * mm, "end": v(19.85, -37.8) * mm});
            skLineSegment(sketch, "E684", {"start": v(19.85, -37.8) * mm, "end": v(20.23, -37.58) * mm});
            skLineSegment(sketch, "E685", {"start": v(20.23, -37.58) * mm, "end": v(20.62, -37.35) * mm});
            skLineSegment(sketch, "E686", {"start": v(20.62, -37.35) * mm, "end": v(21, -37.11) * mm});
            skLineSegment(sketch, "E687", {"start": v(21, -37.11) * mm, "end": v(21.38, -36.88) * mm});
            skLineSegment(sketch, "E688", {"start": v(21.38, -36.88) * mm, "end": v(21.76, -36.65) * mm});
            skLineSegment(sketch, "E689", {"start": v(21.76, -36.65) * mm, "end": v(22.14, -36.42) * mm});
            skLineSegment(sketch, "E690", {"start": v(22.14, -36.42) * mm, "end": v(22.52, -36.2) * mm});
            skLineSegment(sketch, "E691", {"start": v(22.52, -36.2) * mm, "end": v(22.9, -35.96) * mm});
            skLineSegment(sketch, "E692", {"start": v(22.9, -35.96) * mm, "end": v(23.28, -35.73) * mm});
            skLineSegment(sketch, "E693", {"start": v(23.28, -35.73) * mm, "end": v(23.66, -35.5) * mm});
            skLineSegment(sketch, "E694", {"start": v(23.66, -35.5) * mm, "end": v(24.05, -35.27) * mm});
            skLineSegment(sketch, "E695", {"start": v(24.05, -35.27) * mm, "end": v(24.43, -35.03) * mm});
            skLineSegment(sketch, "E696", {"start": v(24.43, -35.03) * mm, "end": v(24.72, -34.86) * mm});
            skLineSegment(sketch, "E697", {"start": v(24.72, -34.86) * mm, "end": v(24.96, -35.23) * mm});
            skLineSegment(sketch, "E698", {"start": v(24.96, -35.23) * mm, "end": v(25.2, -35.6) * mm});
            skLineSegment(sketch, "E699", {"start": v(25.2, -35.6) * mm, "end": v(25.45, -35.98) * mm});
            skLineSegment(sketch, "E700", {"start": v(25.45, -35.98) * mm, "end": v(25.69, -36.35) * mm});
            skLineSegment(sketch, "E701", {"start": v(25.69, -36.35) * mm, "end": v(25.93, -36.73) * mm});
            skLineSegment(sketch, "E702", {"start": v(25.93, -36.73) * mm, "end": v(26.17, -37.1) * mm});
            skLineSegment(sketch, "E703", {"start": v(26.17, -37.1) * mm, "end": v(26.42, -37.47) * mm});
            skLineSegment(sketch, "E704", {"start": v(26.42, -37.47) * mm, "end": v(26.66, -37.85) * mm});
            skLineSegment(sketch, "E705", {"start": v(26.66, -37.85) * mm, "end": v(26.9, -38.22) * mm});
            skLineSegment(sketch, "E706", {"start": v(26.9, -38.22) * mm, "end": v(27.14, -38.6) * mm});
            skLineSegment(sketch, "E707", {"start": v(27.14, -38.6) * mm, "end": v(27.39, -38.97) * mm});
            skLineSegment(sketch, "E708", {"start": v(27.39, -38.97) * mm, "end": v(27.63, -39.34) * mm});
            skLineSegment(sketch, "E709", {"start": v(27.63, -39.34) * mm, "end": v(27.87, -39.72) * mm});
            skLineSegment(sketch, "E710", {"start": v(27.87, -39.72) * mm, "end": v(28.12, -40.1) * mm});
            skLineSegment(sketch, "E711", {"start": v(28.12, -40.1) * mm, "end": v(28.36, -40.46) * mm});
            skLineSegment(sketch, "E712", {"start": v(28.36, -40.46) * mm, "end": v(28.6, -40.84) * mm});
            skLineSegment(sketch, "E713", {"start": v(28.6, -40.84) * mm, "end": v(28.68, -40.96) * mm});
            skLineSegment(sketch, "E714", {"start": v(28.68, -40.96) * mm, "end": v(29.04, -40.7) * mm});
            skLineSegment(sketch, "E715", {"start": v(29.04, -40.7) * mm, "end": v(29.4, -40.44) * mm});
            skLineSegment(sketch, "E716", {"start": v(29.4, -40.44) * mm, "end": v(29.74, -40.2) * mm});
            skLineSegment(sketch, "E717", {"start": v(29.74, -40.2) * mm, "end": v(29.58, -39.78) * mm});
            skLineSegment(sketch, "E718", {"start": v(29.58, -39.78) * mm, "end": v(29.41, -39.36) * mm});
            skLineSegment(sketch, "E719", {"start": v(29.41, -39.36) * mm, "end": v(29.25, -38.95) * mm});
            skLineSegment(sketch, "E720", {"start": v(29.25, -38.95) * mm, "end": v(29.08, -38.54) * mm});
            skLineSegment(sketch, "E721", {"start": v(29.08, -38.54) * mm, "end": v(28.92, -38.12) * mm});
            skLineSegment(sketch, "E722", {"start": v(28.92, -38.12) * mm, "end": v(28.76, -37.7) * mm});
            skLineSegment(sketch, "E723", {"start": v(28.76, -37.7) * mm, "end": v(28.6, -37.3) * mm});
            skLineSegment(sketch, "E724", {"start": v(28.6, -37.3) * mm, "end": v(28.43, -36.88) * mm});
            skLineSegment(sketch, "E725", {"start": v(28.43, -36.88) * mm, "end": v(28.26, -36.46) * mm});
            skLineSegment(sketch, "E726", {"start": v(28.26, -36.46) * mm, "end": v(28.1, -36.05) * mm});
            skLineSegment(sketch, "E727", {"start": v(28.1, -36.05) * mm, "end": v(27.94, -35.64) * mm});
            skLineSegment(sketch, "E728", {"start": v(27.94, -35.64) * mm, "end": v(27.77, -35.22) * mm});
            skLineSegment(sketch, "E729", {"start": v(27.77, -35.22) * mm, "end": v(27.6, -34.8) * mm});
            skLineSegment(sketch, "E730", {"start": v(27.6, -34.8) * mm, "end": v(27.44, -34.4) * mm});
            skLineSegment(sketch, "E731", {"start": v(27.44, -34.4) * mm, "end": v(27.28, -33.98) * mm});
            skLineSegment(sketch, "E732", {"start": v(27.28, -33.98) * mm, "end": v(27.12, -33.56) * mm});
            skLineSegment(sketch, "E733", {"start": v(27.12, -33.56) * mm, "end": v(26.96, -33.16) * mm});
            skLineSegment(sketch, "E734", {"start": v(26.96, -33.16) * mm, "end": v(27.28, -32.85) * mm});
            skLineSegment(sketch, "E735", {"start": v(27.28, -32.85) * mm, "end": v(27.6, -32.55) * mm});
            skLineSegment(sketch, "E736", {"start": v(27.6, -32.55) * mm, "end": v(27.93, -32.24) * mm});
            skLineSegment(sketch, "E737", {"start": v(27.93, -32.24) * mm, "end": v(28.25, -31.94) * mm});
            skLineSegment(sketch, "E738", {"start": v(28.25, -31.94) * mm, "end": v(28.58, -31.63) * mm});
            skLineSegment(sketch, "E739", {"start": v(28.58, -31.63) * mm, "end": v(28.9, -31.33) * mm});
            skLineSegment(sketch, "E740", {"start": v(28.9, -31.33) * mm, "end": v(29.23, -31.02) * mm});
            skLineSegment(sketch, "E741", {"start": v(29.23, -31.02) * mm, "end": v(29.55, -30.72) * mm});
            skLineSegment(sketch, "E742", {"start": v(29.55, -30.72) * mm, "end": v(29.88, -30.41) * mm});
            skLineSegment(sketch, "E743", {"start": v(29.88, -30.41) * mm, "end": v(30.2, -30.1) * mm});
            skLineSegment(sketch, "E744", {"start": v(30.2, -30.1) * mm, "end": v(30.53, -29.8) * mm});
            skLineSegment(sketch, "E745", {"start": v(30.53, -29.8) * mm, "end": v(30.85, -29.5) * mm});
            skLineSegment(sketch, "E746", {"start": v(30.85, -29.5) * mm, "end": v(31.18, -29.2) * mm});
            skLineSegment(sketch, "E747", {"start": v(31.18, -29.2) * mm, "end": v(31.43, -28.96) * mm});
            skLineSegment(sketch, "E748", {"start": v(31.43, -28.96) * mm, "end": v(31.74, -29.27) * mm});
            skLineSegment(sketch, "E749", {"start": v(31.74, -29.27) * mm, "end": v(32.06, -29.59) * mm});
            skLineSegment(sketch, "E750", {"start": v(32.06, -29.59) * mm, "end": v(32.37, -29.9) * mm});
            skLineSegment(sketch, "E751", {"start": v(32.37, -29.9) * mm, "end": v(32.69, -30.22) * mm});
            skLineSegment(sketch, "E752", {"start": v(32.69, -30.22) * mm, "end": v(33, -30.53) * mm});
            skLineSegment(sketch, "E753", {"start": v(33, -30.53) * mm, "end": v(33.32, -30.85) * mm});
            skLineSegment(sketch, "E754", {"start": v(33.32, -30.85) * mm, "end": v(33.63, -31.16) * mm});
            skLineSegment(sketch, "E755", {"start": v(33.63, -31.16) * mm, "end": v(33.95, -31.48) * mm});
            skLineSegment(sketch, "E756", {"start": v(33.95, -31.48) * mm, "end": v(34.26, -31.8) * mm});
            skLineSegment(sketch, "E757", {"start": v(34.26, -31.8) * mm, "end": v(34.58, -32.1) * mm});
            skLineSegment(sketch, "E758", {"start": v(34.58, -32.1) * mm, "end": v(34.9, -32.42) * mm});
            skLineSegment(sketch, "E759", {"start": v(34.9, -32.42) * mm, "end": v(35.2, -32.74) * mm});
            skLineSegment(sketch, "E760", {"start": v(35.2, -32.74) * mm, "end": v(35.52, -33.05) * mm});
            skLineSegment(sketch, "E761", {"start": v(35.52, -33.05) * mm, "end": v(35.84, -33.37) * mm});
            skLineSegment(sketch, "E762", {"start": v(35.84, -33.37) * mm, "end": v(36.15, -33.68) * mm});
            skLineSegment(sketch, "E763", {"start": v(36.15, -33.68) * mm, "end": v(36.47, -34) * mm});
            skLineSegment(sketch, "E764", {"start": v(36.47, -34) * mm, "end": v(36.57, -34.1) * mm});
            skLineSegment(sketch, "E765", {"start": v(36.57, -34.1) * mm, "end": v(36.87, -33.77) * mm});
            skLineSegment(sketch, "E766", {"start": v(36.87, -33.77) * mm, "end": v(37.17, -33.44) * mm});
            skLineSegment(sketch, "E767", {"start": v(37.17, -33.44) * mm, "end": v(37.45, -33.13) * mm});
            skLineSegment(sketch, "E768", {"start": v(37.45, -33.13) * mm, "end": v(37.2, -32.76) * mm});
            skLineSegment(sketch, "E769", {"start": v(37.2, -32.76) * mm, "end": v(36.95, -32.39) * mm});
            skLineSegment(sketch, "E770", {"start": v(36.95, -32.39) * mm, "end": v(36.7, -32.02) * mm});
            skLineSegment(sketch, "E771", {"start": v(36.7, -32.02) * mm, "end": v(36.46, -31.65) * mm});
            skLineSegment(sketch, "E772", {"start": v(36.46, -31.65) * mm, "end": v(36.21, -31.28) * mm});
            skLineSegment(sketch, "E773", {"start": v(36.21, -31.28) * mm, "end": v(35.97, -30.9) * mm});
            skLineSegment(sketch, "E774", {"start": v(35.97, -30.9) * mm, "end": v(35.72, -30.53) * mm});
            skLineSegment(sketch, "E775", {"start": v(35.72, -30.53) * mm, "end": v(35.47, -30.16) * mm});
            skLineSegment(sketch, "E776", {"start": v(35.47, -30.16) * mm, "end": v(35.23, -29.8) * mm});
            skLineSegment(sketch, "E777", {"start": v(35.23, -29.8) * mm, "end": v(34.98, -29.42) * mm});
            skLineSegment(sketch, "E778", {"start": v(34.98, -29.42) * mm, "end": v(34.74, -29.05) * mm});
            skLineSegment(sketch, "E779", {"start": v(34.74, -29.05) * mm, "end": v(34.49, -28.68) * mm});
            skLineSegment(sketch, "E780", {"start": v(34.49, -28.68) * mm, "end": v(34.24, -28.3) * mm});
            skLineSegment(sketch, "E781", {"start": v(34.24, -28.3) * mm, "end": v(34, -27.93) * mm});
            skLineSegment(sketch, "E782", {"start": v(34, -27.93) * mm, "end": v(33.75, -27.56) * mm});
            skLineSegment(sketch, "E783", {"start": v(33.75, -27.56) * mm, "end": v(33.5, -27.2) * mm});
            skLineSegment(sketch, "E784", {"start": v(33.5, -27.2) * mm, "end": v(33.26, -26.83) * mm});
            skLineSegment(sketch, "E785", {"start": v(33.26, -26.83) * mm, "end": v(33.51, -26.46) * mm});
            skLineSegment(sketch, "E786", {"start": v(33.51, -26.46) * mm, "end": v(33.77, -26.1) * mm});
            skLineSegment(sketch, "E787", {"start": v(33.77, -26.1) * mm, "end": v(34.02, -25.73) * mm});
            skLineSegment(sketch, "E788", {"start": v(34.02, -25.73) * mm, "end": v(34.28, -25.37) * mm});
            skLineSegment(sketch, "E789", {"start": v(34.28, -25.37) * mm, "end": v(34.53, -25) * mm});
            skLineSegment(sketch, "E790", {"start": v(34.53, -25) * mm, "end": v(34.79, -24.63) * mm});
            skLineSegment(sketch, "E791", {"start": v(34.79, -24.63) * mm, "end": v(35.04, -24.27) * mm});
            skLineSegment(sketch, "E792", {"start": v(35.04, -24.27) * mm, "end": v(35.3, -23.9) * mm});
            skLineSegment(sketch, "E793", {"start": v(35.3, -23.9) * mm, "end": v(35.55, -23.53) * mm});
            skLineSegment(sketch, "E794", {"start": v(35.55, -23.53) * mm, "end": v(35.8, -23.17) * mm});
            skLineSegment(sketch, "E795", {"start": v(35.8, -23.17) * mm, "end": v(36.06, -22.8) * mm});
            skLineSegment(sketch, "E796", {"start": v(36.06, -22.8) * mm, "end": v(36.31, -22.44) * mm});
            skLineSegment(sketch, "E797", {"start": v(36.31, -22.44) * mm, "end": v(36.56, -22.07) * mm});
            skLineSegment(sketch, "E798", {"start": v(36.56, -22.07) * mm, "end": v(36.76, -21.8) * mm});
            skLineSegment(sketch, "E799", {"start": v(36.76, -21.8) * mm, "end": v(37.13, -22.03) * mm});
            skLineSegment(sketch, "E800", {"start": v(37.13, -22.03) * mm, "end": v(37.5, -22.28) * mm});
            skLineSegment(sketch, "E801", {"start": v(37.5, -22.28) * mm, "end": v(37.88, -22.52) * mm});
            skLineSegment(sketch, "E802", {"start": v(37.88, -22.52) * mm, "end": v(38.25, -22.76) * mm});
            skLineSegment(sketch, "E803", {"start": v(38.25, -22.76) * mm, "end": v(38.63, -23) * mm});
            skLineSegment(sketch, "E804", {"start": v(38.63, -23) * mm, "end": v(39, -23.25) * mm});
            skLineSegment(sketch, "E805", {"start": v(39, -23.25) * mm, "end": v(39.38, -23.49) * mm});
            skLineSegment(sketch, "E806", {"start": v(39.38, -23.49) * mm, "end": v(39.75, -23.73) * mm});
            skLineSegment(sketch, "E807", {"start": v(39.75, -23.73) * mm, "end": v(40.12, -23.98) * mm});
            skLineSegment(sketch, "E808", {"start": v(40.12, -23.98) * mm, "end": v(40.5, -24.22) * mm});
            skLineSegment(sketch, "E809", {"start": v(40.5, -24.22) * mm, "end": v(40.87, -24.46) * mm});
            skLineSegment(sketch, "E810", {"start": v(40.87, -24.46) * mm, "end": v(41.24, -24.7) * mm});
            skLineSegment(sketch, "E811", {"start": v(41.24, -24.7) * mm, "end": v(41.62, -24.95) * mm});
            skLineSegment(sketch, "E812", {"start": v(41.62, -24.95) * mm, "end": v(42, -25.19) * mm});
            skLineSegment(sketch, "E813", {"start": v(42, -25.19) * mm, "end": v(42.37, -25.43) * mm});
            skLineSegment(sketch, "E814", {"start": v(42.37, -25.43) * mm, "end": v(42.74, -25.67) * mm});
            skLineSegment(sketch, "E815", {"start": v(42.74, -25.67) * mm, "end": v(42.86, -25.75) * mm});
            skLineSegment(sketch, "E816", {"start": v(42.86, -25.75) * mm, "end": v(43.08, -25.37) * mm});
            skLineSegment(sketch, "E817", {"start": v(43.08, -25.37) * mm, "end": v(43.3, -24.98) * mm});
            skLineSegment(sketch, "E818", {"start": v(43.3, -24.98) * mm, "end": v(43.52, -24.62) * mm});
            skLineSegment(sketch, "E819", {"start": v(43.52, -24.62) * mm, "end": v(43.2, -24.3) * mm});
            skLineSegment(sketch, "E820", {"start": v(43.2, -24.3) * mm, "end": v(42.88, -24) * mm});
            skLineSegment(sketch, "E821", {"start": v(42.88, -24) * mm, "end": v(42.56, -23.69) * mm});
            skLineSegment(sketch, "E822", {"start": v(42.56, -23.69) * mm, "end": v(42.24, -23.37) * mm});
            skLineSegment(sketch, "E823", {"start": v(42.24, -23.37) * mm, "end": v(41.93, -23.06) * mm});
            skLineSegment(sketch, "E824", {"start": v(41.93, -23.06) * mm, "end": v(41.6, -22.75) * mm});
            skLineSegment(sketch, "E825", {"start": v(41.6, -22.75) * mm, "end": v(41.29, -22.44) * mm});
            skLineSegment(sketch, "E826", {"start": v(41.29, -22.44) * mm, "end": v(40.97, -22.13) * mm});
            skLineSegment(sketch, "E827", {"start": v(40.97, -22.13) * mm, "end": v(40.65, -21.82) * mm});
            skLineSegment(sketch, "E828", {"start": v(40.65, -21.82) * mm, "end": v(40.33, -21.5) * mm});
            skLineSegment(sketch, "E829", {"start": v(40.33, -21.5) * mm, "end": v(40.02, -21.2) * mm});
            skLineSegment(sketch, "E830", {"start": v(40.02, -21.2) * mm, "end": v(39.7, -20.88) * mm});
            skLineSegment(sketch, "E831", {"start": v(39.7, -20.88) * mm, "end": v(39.38, -20.57) * mm});
            skLineSegment(sketch, "E832", {"start": v(39.38, -20.57) * mm, "end": v(39.06, -20.26) * mm});
            skLineSegment(sketch, "E833", {"start": v(39.06, -20.26) * mm, "end": v(38.74, -19.94) * mm});
            skLineSegment(sketch, "E834", {"start": v(38.74, -19.94) * mm, "end": v(38.42, -19.63) * mm});
            skLineSegment(sketch, "E835", {"start": v(38.42, -19.63) * mm, "end": v(38.11, -19.33) * mm});
            skLineSegment(sketch, "E836", {"start": v(38.11, -19.33) * mm, "end": v(38.28, -18.92) * mm});
            skLineSegment(sketch, "E837", {"start": v(38.28, -18.92) * mm, "end": v(38.46, -18.5) * mm});
            skLineSegment(sketch, "E838", {"start": v(38.46, -18.5) * mm, "end": v(38.63, -18.1) * mm});
            skLineSegment(sketch, "E839", {"start": v(38.63, -18.1) * mm, "end": v(38.8, -17.68) * mm});
            skLineSegment(sketch, "E840", {"start": v(38.8, -17.68) * mm, "end": v(38.97, -17.27) * mm});
            skLineSegment(sketch, "E841", {"start": v(38.97, -17.27) * mm, "end": v(39.15, -16.86) * mm});
            skLineSegment(sketch, "E842", {"start": v(39.15, -16.86) * mm, "end": v(39.32, -16.45) * mm});
            skLineSegment(sketch, "E843", {"start": v(39.32, -16.45) * mm, "end": v(39.5, -16.04) * mm});
            skLineSegment(sketch, "E844", {"start": v(39.5, -16.04) * mm, "end": v(39.66, -15.63) * mm});
            skLineSegment(sketch, "E845", {"start": v(39.66, -15.63) * mm, "end": v(39.84, -15.22) * mm});
            skLineSegment(sketch, "E846", {"start": v(39.84, -15.22) * mm, "end": v(40, -14.8) * mm});
            skLineSegment(sketch, "E847", {"start": v(40, -14.8) * mm, "end": v(40.18, -14.4) * mm});
            skLineSegment(sketch, "E848", {"start": v(40.18, -14.4) * mm, "end": v(40.35, -13.99) * mm});
            skLineSegment(sketch, "E849", {"start": v(40.35, -13.99) * mm, "end": v(40.49, -13.67) * mm});
            skLineSegment(sketch, "E850", {"start": v(40.49, -13.67) * mm, "end": v(40.9, -13.83) * mm});
            skLineSegment(sketch, "E851", {"start": v(40.9, -13.83) * mm, "end": v(41.32, -14) * mm});
            skLineSegment(sketch, "E852", {"start": v(41.32, -14) * mm, "end": v(41.73, -14.15) * mm});
            skLineSegment(sketch, "E853", {"start": v(41.73, -14.15) * mm, "end": v(42.15, -14.31) * mm});
            skLineSegment(sketch, "E854", {"start": v(42.15, -14.31) * mm, "end": v(42.57, -14.47) * mm});
            skLineSegment(sketch, "E855", {"start": v(42.57, -14.47) * mm, "end": v(42.98, -14.63) * mm});
            skLineSegment(sketch, "E856", {"start": v(42.98, -14.63) * mm, "end": v(43.4, -14.8) * mm});
            skLineSegment(sketch, "E857", {"start": v(43.4, -14.8) * mm, "end": v(43.81, -14.95) * mm});
            skLineSegment(sketch, "E858", {"start": v(43.81, -14.95) * mm, "end": v(44.23, -15.1) * mm});
            skLineSegment(sketch, "E859", {"start": v(44.23, -15.1) * mm, "end": v(44.65, -15.27) * mm});
            skLineSegment(sketch, "E860", {"start": v(44.65, -15.27) * mm, "end": v(45.06, -15.43) * mm});
            skLineSegment(sketch, "E861", {"start": v(45.06, -15.43) * mm, "end": v(45.48, -15.59) * mm});
            skLineSegment(sketch, "E862", {"start": v(45.48, -15.59) * mm, "end": v(45.9, -15.75) * mm});
            skLineSegment(sketch, "E863", {"start": v(45.9, -15.75) * mm, "end": v(46.31, -15.9) * mm});
            skLineSegment(sketch, "E864", {"start": v(46.31, -15.9) * mm, "end": v(46.73, -16.07) * mm});
            skLineSegment(sketch, "E865", {"start": v(46.73, -16.07) * mm, "end": v(47.14, -16.23) * mm});
            skLineSegment(sketch, "E866", {"start": v(47.14, -16.23) * mm, "end": v(47.28, -16.28) * mm});
            skLineSegment(sketch, "E867", {"start": v(47.28, -16.28) * mm, "end": v(47.42, -15.86) * mm});
            skLineSegment(sketch, "E868", {"start": v(47.42, -15.86) * mm, "end": v(47.56, -15.43) * mm});
            skLineSegment(sketch, "E869", {"start": v(47.56, -15.43) * mm, "end": v(47.69, -15.04) * mm});
            skLineSegment(sketch, "E870", {"start": v(47.69, -15.04) * mm, "end": v(47.3, -14.8) * mm});
            skLineSegment(sketch, "E871", {"start": v(47.3, -14.8) * mm, "end": v(46.93, -14.56) * mm});
            skLineSegment(sketch, "E872", {"start": v(46.93, -14.56) * mm, "end": v(46.56, -14.32) * mm});
            skLineSegment(sketch, "E873", {"start": v(46.56, -14.32) * mm, "end": v(46.18, -14.08) * mm});
            skLineSegment(sketch, "E874", {"start": v(46.18, -14.08) * mm, "end": v(45.8, -13.84) * mm});
            skLineSegment(sketch, "E875", {"start": v(45.8, -13.84) * mm, "end": v(45.43, -13.6) * mm});
            skLineSegment(sketch, "E876", {"start": v(45.43, -13.6) * mm, "end": v(45.05, -13.36) * mm});
            skLineSegment(sketch, "E877", {"start": v(45.05, -13.36) * mm, "end": v(44.68, -13.13) * mm});
            skLineSegment(sketch, "E878", {"start": v(44.68, -13.13) * mm, "end": v(44.3, -12.89) * mm});
            skLineSegment(sketch, "E879", {"start": v(44.3, -12.89) * mm, "end": v(43.92, -12.65) * mm});
            skLineSegment(sketch, "E880", {"start": v(43.92, -12.65) * mm, "end": v(43.55, -12.4) * mm});
            skLineSegment(sketch, "E881", {"start": v(43.55, -12.4) * mm, "end": v(43.17, -12.17) * mm});
            skLineSegment(sketch, "E882", {"start": v(43.17, -12.17) * mm, "end": v(42.8, -11.93) * mm});
            skLineSegment(sketch, "E883", {"start": v(42.8, -11.93) * mm, "end": v(42.42, -11.7) * mm});
            skLineSegment(sketch, "E884", {"start": v(42.42, -11.7) * mm, "end": v(42.04, -11.45) * mm});
            skLineSegment(sketch, "E885", {"start": v(42.04, -11.45) * mm, "end": v(41.67, -11.22) * mm});
            skLineSegment(sketch, "E886", {"start": v(41.67, -11.22) * mm, "end": v(41.3, -10.98) * mm});
            skLineSegment(sketch, "E887", {"start": v(41.3, -10.98) * mm, "end": v(41.38, -10.54) * mm});
            skLineSegment(sketch, "E888", {"start": v(41.38, -10.54) * mm, "end": v(41.46, -10.1) * mm});
            skLineSegment(sketch, "E889", {"start": v(41.46, -10.1) * mm, "end": v(41.55, -9.67) * mm});
            skLineSegment(sketch, "E890", {"start": v(41.55, -9.67) * mm, "end": v(41.63, -9.23) * mm});
            skLineSegment(sketch, "E891", {"start": v(41.63, -9.23) * mm, "end": v(41.71, -8.8) * mm});
            skLineSegment(sketch, "E892", {"start": v(41.71, -8.8) * mm, "end": v(41.8, -8.35) * mm});
            skLineSegment(sketch, "E893", {"start": v(41.8, -8.35) * mm, "end": v(41.88, -7.92) * mm});
            skLineSegment(sketch, "E894", {"start": v(41.88, -7.92) * mm, "end": v(41.96, -7.48) * mm});
            skLineSegment(sketch, "E895", {"start": v(41.96, -7.48) * mm, "end": v(42.05, -7.04) * mm});
            skLineSegment(sketch, "E896", {"start": v(42.05, -7.04) * mm, "end": v(42.13, -6.6) * mm});
            skLineSegment(sketch, "E897", {"start": v(42.13, -6.6) * mm, "end": v(42.21, -6.17) * mm});
            skLineSegment(sketch, "E898", {"start": v(42.21, -6.17) * mm, "end": v(42.3, -5.73) * mm});
            skLineSegment(sketch, "E899", {"start": v(42.3, -5.73) * mm, "end": v(42.38, -5.3) * mm});
            skLineSegment(sketch, "E900", {"start": v(42.38, -5.3) * mm, "end": v(42.44, -4.96) * mm});
            skLineSegment(sketch, "E901", {"start": v(42.44, -4.96) * mm, "end": v(42.88, -5.03) * mm});
            skLineSegment(sketch, "E902", {"start": v(42.88, -5.03) * mm, "end": v(43.32, -5.1) * mm});
            skLineSegment(sketch, "E903", {"start": v(43.32, -5.1) * mm, "end": v(43.76, -5.16) * mm});
            skLineSegment(sketch, "E904", {"start": v(43.76, -5.16) * mm, "end": v(44.2, -5.23) * mm});
            skLineSegment(sketch, "E905", {"start": v(44.2, -5.23) * mm, "end": v(44.65, -5.3) * mm});
            skLineSegment(sketch, "E906", {"start": v(44.65, -5.3) * mm, "end": v(45.09, -5.37) * mm});
            skLineSegment(sketch, "E907", {"start": v(45.09, -5.37) * mm, "end": v(45.53, -5.44) * mm});
            skLineSegment(sketch, "E908", {"start": v(45.53, -5.44) * mm, "end": v(45.97, -5.51) * mm});
            skLineSegment(sketch, "E909", {"start": v(45.97, -5.51) * mm, "end": v(46.4, -5.58) * mm});
            skLineSegment(sketch, "E910", {"start": v(46.4, -5.58) * mm, "end": v(46.85, -5.65) * mm});
            skLineSegment(sketch, "E911", {"start": v(46.85, -5.65) * mm, "end": v(47.29, -5.72) * mm});
            skLineSegment(sketch, "E912", {"start": v(47.29, -5.72) * mm, "end": v(47.73, -5.8) * mm});
            skLineSegment(sketch, "E913", {"start": v(47.73, -5.8) * mm, "end": v(48.17, -5.86) * mm});
            skLineSegment(sketch, "E914", {"start": v(48.17, -5.86) * mm, "end": v(48.6, -5.93) * mm});
            skLineSegment(sketch, "E915", {"start": v(48.6, -5.93) * mm, "end": v(49.05, -6) * mm});
            skLineSegment(sketch, "E916", {"start": v(49.05, -6) * mm, "end": v(49.49, -6.07) * mm});
            skLineSegment(sketch, "E917", {"start": v(49.49, -6.07) * mm, "end": v(49.63, -6.1) * mm});
            skLineSegment(sketch, "E918", {"start": v(49.63, -6.1) * mm, "end": v(49.68, -5.65) * mm});
            skLineSegment(sketch, "E919", {"start": v(49.68, -5.65) * mm, "end": v(49.72, -5.2) * mm});
            skLineSegment(sketch, "E920", {"start": v(49.72, -5.2) * mm, "end": v(49.77, -4.8) * mm});
            skLineSegment(sketch, "E921", {"start": v(49.77, -4.8) * mm, "end": v(49.35, -4.64) * mm});
            skLineSegment(sketch, "E922", {"start": v(49.35, -4.64) * mm, "end": v(48.93, -4.48) * mm});
            skLineSegment(sketch, "E923", {"start": v(48.93, -4.48) * mm, "end": v(48.52, -4.33) * mm});
            skLineSegment(sketch, "E924", {"start": v(48.52, -4.33) * mm, "end": v(48.1, -4.17) * mm});
            skLineSegment(sketch, "E925", {"start": v(48.1, -4.17) * mm, "end": v(47.68, -4.02) * mm});
            skLineSegment(sketch, "E926", {"start": v(47.68, -4.02) * mm, "end": v(47.26, -3.86) * mm});
            skLineSegment(sketch, "E927", {"start": v(47.26, -3.86) * mm, "end": v(46.85, -3.7) * mm});
            skLineSegment(sketch, "E928", {"start": v(46.85, -3.7) * mm, "end": v(46.43, -3.55) * mm});
            skLineSegment(sketch, "E929", {"start": v(46.43, -3.55) * mm, "end": v(46.01, -3.4) * mm});
            skLineSegment(sketch, "E930", {"start": v(46.01, -3.4) * mm, "end": v(45.6, -3.24) * mm});
            skLineSegment(sketch, "E931", {"start": v(45.6, -3.24) * mm, "end": v(45.18, -3.08) * mm});
            skLineSegment(sketch, "E932", {"start": v(45.18, -3.08) * mm, "end": v(44.76, -2.93) * mm});
            skLineSegment(sketch, "E933", {"start": v(44.76, -2.93) * mm, "end": v(44.34, -2.77) * mm});
            skLineSegment(sketch, "E934", {"start": v(44.34, -2.77) * mm, "end": v(43.92, -2.62) * mm});
            skLineSegment(sketch, "E935", {"start": v(43.92, -2.62) * mm, "end": v(43.5, -2.46) * mm});
            skLineSegment(sketch, "E936", {"start": v(43.5, -2.46) * mm, "end": v(43.09, -2.3) * mm});
            skLineSegment(sketch, "E937", {"start": v(43.09, -2.3) * mm, "end": v(42.68, -2.16) * mm});
            skLineSegment(sketch, "E938", {"start": v(42.68, -2.16) * mm, "end": v(42.67, -1.7) * mm});
            skLineSegment(sketch, "E939", {"start": v(42.67, -1.7) * mm, "end": v(42.66, -1.26) * mm});
            skLineSegment(sketch, "E940", {"start": v(42.66, -1.26) * mm, "end": v(42.65, -0.82) * mm});
            skLineSegment(sketch, "E941", {"start": v(42.65, -0.82) * mm, "end": v(42.64, -0.37) * mm});
            skLineSegment(sketch, "E942", {"start": v(42.64, -0.37) * mm, "end": v(42.63, 0.07) * mm});
            skLineSegment(sketch, "E943", {"start": v(42.63, 0.07) * mm, "end": v(42.62, 0.52) * mm});
            skLineSegment(sketch, "E944", {"start": v(42.62, 0.52) * mm, "end": v(42.61, 0.96) * mm});
            skLineSegment(sketch, "E945", {"start": v(42.61, 0.96) * mm, "end": v(42.6, 1.4) * mm});
            skLineSegment(sketch, "E946", {"start": v(42.6, 1.4) * mm, "end": v(42.6, 1.85) * mm});
            skLineSegment(sketch, "E947", {"start": v(42.6, 1.85) * mm, "end": v(42.58, 2.3) * mm});
            skLineSegment(sketch, "E948", {"start": v(42.58, 2.3) * mm, "end": v(42.57, 2.75) * mm});
            skLineSegment(sketch, "E949", {"start": v(42.57, 2.75) * mm, "end": v(42.56, 3.2) * mm});
            skLineSegment(sketch, "E950", {"start": v(42.56, 3.2) * mm, "end": v(42.55, 3.64) * mm});
            skLineSegment(sketch, "E951", {"start": v(42.55, 3.64) * mm, "end": v(42.55, 3.98) * mm});
            skLineSegment(sketch, "E952", {"start": v(42.55, 3.98) * mm, "end": v(43, 4) * mm});
            skLineSegment(sketch, "E953", {"start": v(43, 4) * mm, "end": v(43.44, 4.02) * mm});
            skLineSegment(sketch, "E954", {"start": v(43.44, 4.02) * mm, "end": v(43.88, 4.05) * mm});
            skLineSegment(sketch, "E955", {"start": v(43.88, 4.05) * mm, "end": v(44.33, 4.07) * mm});
            skLineSegment(sketch, "E956", {"start": v(44.33, 4.07) * mm, "end": v(44.77, 4.1) * mm});
            skLineSegment(sketch, "E957", {"start": v(44.77, 4.1) * mm, "end": v(45.22, 4.12) * mm});
            skLineSegment(sketch, "E958", {"start": v(45.22, 4.12) * mm, "end": v(45.66, 4.14) * mm});
            skLineSegment(sketch, "E959", {"start": v(45.66, 4.14) * mm, "end": v(46.1, 4.16) * mm});
            skLineSegment(sketch, "E960", {"start": v(46.1, 4.16) * mm, "end": v(46.55, 4.19) * mm});
            skLineSegment(sketch, "E961", {"start": v(46.55, 4.19) * mm, "end": v(47, 4.21) * mm});
            skLineSegment(sketch, "E962", {"start": v(47, 4.21) * mm, "end": v(47.44, 4.23) * mm});
            skLineSegment(sketch, "E963", {"start": v(47.44, 4.23) * mm, "end": v(47.89, 4.26) * mm});
            skLineSegment(sketch, "E964", {"start": v(47.89, 4.26) * mm, "end": v(48.33, 4.28) * mm});
            skLineSegment(sketch, "E965", {"start": v(48.33, 4.28) * mm, "end": v(48.78, 4.3) * mm});
            skLineSegment(sketch, "E966", {"start": v(48.78, 4.3) * mm, "end": v(49.22, 4.33) * mm});
            skLineSegment(sketch, "E967", {"start": v(49.22, 4.33) * mm, "end": v(49.67, 4.35) * mm});
            skLineSegment(sketch, "E968", {"start": v(49.67, 4.35) * mm, "end": v(49.8, 4.36) * mm});
            skLineSegment(sketch, "E969", {"start": v(49.8, 4.36) * mm, "end": v(49.77, 4.8) * mm});
            skLineSegment(sketch, "E970", {"start": v(49.77, 4.8) * mm, "end": v(49.72, 5.24) * mm});
            skLineSegment(sketch, "E971", {"start": v(49.72, 5.24) * mm, "end": v(49.68, 5.66) * mm});
            skLineSegment(sketch, "E972", {"start": v(49.68, 5.66) * mm, "end": v(49.24, 5.73) * mm});
            skLineSegment(sketch, "E973", {"start": v(49.24, 5.73) * mm, "end": v(48.8, 5.8) * mm});
            skLineSegment(sketch, "E974", {"start": v(48.8, 5.8) * mm, "end": v(48.36, 5.86) * mm});
            skLineSegment(sketch, "E975", {"start": v(48.36, 5.86) * mm, "end": v(47.92, 5.92) * mm});
            skLineSegment(sketch, "E976", {"start": v(47.92, 5.92) * mm, "end": v(47.47, 5.99) * mm});
            skLineSegment(sketch, "E977", {"start": v(47.47, 5.99) * mm, "end": v(47.03, 6.05) * mm});
            skLineSegment(sketch, "E978", {"start": v(47.03, 6.05) * mm, "end": v(46.6, 6.12) * mm});
            skLineSegment(sketch, "E979", {"start": v(46.6, 6.12) * mm, "end": v(46.15, 6.18) * mm});
            skLineSegment(sketch, "E980", {"start": v(46.15, 6.18) * mm, "end": v(45.71, 6.25) * mm});
            skLineSegment(sketch, "E981", {"start": v(45.71, 6.25) * mm, "end": v(45.27, 6.31) * mm});
            skLineSegment(sketch, "E982", {"start": v(45.27, 6.31) * mm, "end": v(44.83, 6.38) * mm});
            skLineSegment(sketch, "E983", {"start": v(44.83, 6.38) * mm, "end": v(44.39, 6.44) * mm});
            skLineSegment(sketch, "E984", {"start": v(44.39, 6.44) * mm, "end": v(43.95, 6.5) * mm});
            skLineSegment(sketch, "E985", {"start": v(43.95, 6.5) * mm, "end": v(43.5, 6.57) * mm});
            skLineSegment(sketch, "E986", {"start": v(43.5, 6.57) * mm, "end": v(43.07, 6.64) * mm});
            skLineSegment(sketch, "E987", {"start": v(43.07, 6.64) * mm, "end": v(42.63, 6.7) * mm});
            skLineSegment(sketch, "E988", {"start": v(42.63, 6.7) * mm, "end": v(42.2, 6.77) * mm});
            skLineSegment(sketch, "E989", {"start": v(42.2, 6.77) * mm, "end": v(42.1, 7.2) * mm});
            skLineSegment(sketch, "E990", {"start": v(42.1, 7.2) * mm, "end": v(41.99, 7.63) * mm});
            skLineSegment(sketch, "E991", {"start": v(41.99, 7.63) * mm, "end": v(41.89, 8.07) * mm});
            skLineSegment(sketch, "E992", {"start": v(41.89, 8.07) * mm, "end": v(41.79, 8.5) * mm});
            skLineSegment(sketch, "E993", {"start": v(41.79, 8.5) * mm, "end": v(41.68, 8.93) * mm});
            skLineSegment(sketch, "E994", {"start": v(41.68, 8.93) * mm, "end": v(41.58, 9.37) * mm});
            skLineSegment(sketch, "E995", {"start": v(41.58, 9.37) * mm, "end": v(41.48, 9.8) * mm});
            skLineSegment(sketch, "E996", {"start": v(41.48, 9.8) * mm, "end": v(41.38, 10.24) * mm});
            skLineSegment(sketch, "E997", {"start": v(41.38, 10.24) * mm, "end": v(41.28, 10.67) * mm});
            skLineSegment(sketch, "E998", {"start": v(41.28, 10.67) * mm, "end": v(41.17, 11.1) * mm});
            skLineSegment(sketch, "E999", {"start": v(41.17, 11.1) * mm, "end": v(41.07, 11.54) * mm});
            skLineSegment(sketch, "E1000", {"start": v(41.07, 11.54) * mm, "end": v(40.97, 11.97) * mm});
            skLineSegment(sketch, "E1001", {"start": v(40.97, 11.97) * mm, "end": v(40.87, 12.4) * mm});
            skLineSegment(sketch, "E1002", {"start": v(40.87, 12.4) * mm, "end": v(40.8, 12.74) * mm});
            skLineSegment(sketch, "E1003", {"start": v(40.8, 12.74) * mm, "end": v(41.22, 12.85) * mm});
            skLineSegment(sketch, "E1004", {"start": v(41.22, 12.85) * mm, "end": v(41.65, 12.97) * mm});
            skLineSegment(sketch, "E1005", {"start": v(41.65, 12.97) * mm, "end": v(42.08, 13.08) * mm});
            skLineSegment(sketch, "E1006", {"start": v(42.08, 13.08) * mm, "end": v(42.51, 13.2) * mm});
            skLineSegment(sketch, "E1007", {"start": v(42.51, 13.2) * mm, "end": v(42.94, 13.31) * mm});
            skLineSegment(sketch, "E1008", {"start": v(42.94, 13.31) * mm, "end": v(43.37, 13.43) * mm});
            skLineSegment(sketch, "E1009", {"start": v(43.37, 13.43) * mm, "end": v(43.8, 13.54) * mm});
            skLineSegment(sketch, "E1010", {"start": v(43.8, 13.54) * mm, "end": v(44.23, 13.66) * mm});
            skLineSegment(sketch, "E1011", {"start": v(44.23, 13.66) * mm, "end": v(44.66, 13.77) * mm});
            skLineSegment(sketch, "E1012", {"start": v(44.66, 13.77) * mm, "end": v(45.1, 13.89) * mm});
            skLineSegment(sketch, "E1013", {"start": v(45.1, 13.89) * mm, "end": v(45.53, 14) * mm});
            skLineSegment(sketch, "E1014", {"start": v(45.53, 14) * mm, "end": v(45.96, 14.12) * mm});
            skLineSegment(sketch, "E1015", {"start": v(45.96, 14.12) * mm, "end": v(46.39, 14.24) * mm});
            skLineSegment(sketch, "E1016", {"start": v(46.39, 14.24) * mm, "end": v(46.82, 14.35) * mm});
            skLineSegment(sketch, "E1017", {"start": v(46.82, 14.35) * mm, "end": v(47.25, 14.47) * mm});
            skLineSegment(sketch, "E1018", {"start": v(47.25, 14.47) * mm, "end": v(47.68, 14.58) * mm});
            skLineSegment(sketch, "E1019", {"start": v(47.68, 14.58) * mm, "end": v(47.82, 14.62) * mm});
            skLineSegment(sketch, "E1020", {"start": v(47.82, 14.62) * mm, "end": v(47.68, 15.04) * mm});
            skLineSegment(sketch, "E1021", {"start": v(47.68, 15.04) * mm, "end": v(47.54, 15.47) * mm});
            skLineSegment(sketch, "E1022", {"start": v(47.54, 15.47) * mm, "end": v(47.42, 15.87) * mm});
            skLineSegment(sketch, "E1023", {"start": v(47.42, 15.87) * mm, "end": v(46.97, 15.84) * mm});
            skLineSegment(sketch, "E1024", {"start": v(46.97, 15.84) * mm, "end": v(46.53, 15.8) * mm});
            skLineSegment(sketch, "E1025", {"start": v(46.53, 15.8) * mm, "end": v(46.08, 15.78) * mm});
            skLineSegment(sketch, "E1026", {"start": v(46.08, 15.78) * mm, "end": v(45.64, 15.75) * mm});
            skLineSegment(sketch, "E1027", {"start": v(45.64, 15.75) * mm, "end": v(45.2, 15.73) * mm});
            skLineSegment(sketch, "E1028", {"start": v(45.2, 15.73) * mm, "end": v(44.75, 15.7) * mm});
            skLineSegment(sketch, "E1029", {"start": v(44.75, 15.7) * mm, "end": v(44.3, 15.67) * mm});
            skLineSegment(sketch, "E1030", {"start": v(44.3, 15.67) * mm, "end": v(43.86, 15.64) * mm});
            skLineSegment(sketch, "E1031", {"start": v(43.86, 15.64) * mm, "end": v(43.41, 15.61) * mm});
            skLineSegment(sketch, "E1032", {"start": v(43.41, 15.61) * mm, "end": v(42.97, 15.59) * mm});
            skLineSegment(sketch, "E1033", {"start": v(42.97, 15.59) * mm, "end": v(42.52, 15.56) * mm});
            skLineSegment(sketch, "E1034", {"start": v(42.52, 15.56) * mm, "end": v(42.08, 15.53) * mm});
            skLineSegment(sketch, "E1035", {"start": v(42.08, 15.53) * mm, "end": v(41.63, 15.5) * mm});
            skLineSegment(sketch, "E1036", {"start": v(41.63, 15.5) * mm, "end": v(41.19, 15.47) * mm});
            skLineSegment(sketch, "E1037", {"start": v(41.19, 15.47) * mm, "end": v(40.75, 15.45) * mm});
            skLineSegment(sketch, "E1038", {"start": v(40.75, 15.45) * mm, "end": v(40.3, 15.42) * mm});
            skLineSegment(sketch, "E1039", {"start": v(40.3, 15.42) * mm, "end": v(39.87, 15.39) * mm});
            skLineSegment(sketch, "E1040", {"start": v(39.87, 15.39) * mm, "end": v(39.68, 15.8) * mm});
            skLineSegment(sketch, "E1041", {"start": v(39.68, 15.8) * mm, "end": v(39.49, 16.2) * mm});
            skLineSegment(sketch, "E1042", {"start": v(39.49, 16.2) * mm, "end": v(39.3, 16.6) * mm});
            skLineSegment(sketch, "E1043", {"start": v(39.3, 16.6) * mm, "end": v(39.1, 17) * mm});
            skLineSegment(sketch, "E1044", {"start": v(39.1, 17) * mm, "end": v(38.92, 17.4) * mm});
            skLineSegment(sketch, "E1045", {"start": v(38.92, 17.4) * mm, "end": v(38.73, 17.8) * mm});
            skLineSegment(sketch, "E1046", {"start": v(38.73, 17.8) * mm, "end": v(38.54, 18.21) * mm});
            skLineSegment(sketch, "E1047", {"start": v(38.54, 18.21) * mm, "end": v(38.35, 18.61) * mm});
            skLineSegment(sketch, "E1048", {"start": v(38.35, 18.61) * mm, "end": v(38.16, 19.02) * mm});
            skLineSegment(sketch, "E1049", {"start": v(38.16, 19.02) * mm, "end": v(37.97, 19.42) * mm});
            skLineSegment(sketch, "E1050", {"start": v(37.97, 19.42) * mm, "end": v(37.78, 19.82) * mm});
            skLineSegment(sketch, "E1051", {"start": v(37.78, 19.82) * mm, "end": v(37.59, 20.23) * mm});
            skLineSegment(sketch, "E1052", {"start": v(37.59, 20.23) * mm, "end": v(37.4, 20.63) * mm});
            skLineSegment(sketch, "E1053", {"start": v(37.4, 20.63) * mm, "end": v(37.25, 20.94) * mm});
            skLineSegment(sketch, "E1054", {"start": v(37.25, 20.94) * mm, "end": v(37.65, 21.14) * mm});
            skLineSegment(sketch, "E1055", {"start": v(37.65, 21.14) * mm, "end": v(38.05, 21.34) * mm});
            skLineSegment(sketch, "E1056", {"start": v(38.05, 21.34) * mm, "end": v(38.44, 21.55) * mm});
            skLineSegment(sketch, "E1057", {"start": v(38.44, 21.55) * mm, "end": v(38.84, 21.75) * mm});
            skLineSegment(sketch, "E1058", {"start": v(38.84, 21.75) * mm, "end": v(39.24, 21.95) * mm});
            skLineSegment(sketch, "E1059", {"start": v(39.24, 21.95) * mm, "end": v(39.63, 22.15) * mm});
            skLineSegment(sketch, "E1060", {"start": v(39.63, 22.15) * mm, "end": v(40.03, 22.35) * mm});
            skLineSegment(sketch, "E1061", {"start": v(40.03, 22.35) * mm, "end": v(40.43, 22.56) * mm});
            skLineSegment(sketch, "E1062", {"start": v(40.43, 22.56) * mm, "end": v(40.82, 22.76) * mm});
            skLineSegment(sketch, "E1063", {"start": v(40.82, 22.76) * mm, "end": v(41.22, 22.96) * mm});
            skLineSegment(sketch, "E1064", {"start": v(41.22, 22.96) * mm, "end": v(41.62, 23.16) * mm});
            skLineSegment(sketch, "E1065", {"start": v(41.62, 23.16) * mm, "end": v(42.02, 23.37) * mm});
            skLineSegment(sketch, "E1066", {"start": v(42.02, 23.37) * mm, "end": v(42.41, 23.57) * mm});
            skLineSegment(sketch, "E1067", {"start": v(42.41, 23.57) * mm, "end": v(42.8, 23.77) * mm});
            skLineSegment(sketch, "E1068", {"start": v(42.8, 23.77) * mm, "end": v(43.2, 23.97) * mm});
            skLineSegment(sketch, "E1069", {"start": v(43.2, 23.97) * mm, "end": v(43.6, 24.18) * mm});
            skLineSegment(sketch, "E1070", {"start": v(43.6, 24.18) * mm, "end": v(43.73, 24.24) * mm});
            skLineSegment(sketch, "E1071", {"start": v(43.73, 24.24) * mm, "end": v(43.5, 24.63) * mm});
            skLineSegment(sketch, "E1072", {"start": v(43.5, 24.63) * mm, "end": v(43.29, 25.01) * mm});
            skLineSegment(sketch, "E1073", {"start": v(43.29, 25.01) * mm, "end": v(43.08, 25.38) * mm});
            skLineSegment(sketch, "E1074", {"start": v(43.08, 25.38) * mm, "end": v(42.65, 25.26) * mm});
            skLineSegment(sketch, "E1075", {"start": v(42.65, 25.26) * mm, "end": v(42.22, 25.14) * mm});
            skLineSegment(sketch, "E1076", {"start": v(42.22, 25.14) * mm, "end": v(41.8, 25.02) * mm});
            skLineSegment(sketch, "E1077", {"start": v(41.8, 25.02) * mm, "end": v(41.36, 24.9) * mm});
            skLineSegment(sketch, "E1078", {"start": v(41.36, 24.9) * mm, "end": v(40.94, 24.78) * mm});
            skLineSegment(sketch, "E1079", {"start": v(40.94, 24.78) * mm, "end": v(40.5, 24.66) * mm});
            skLineSegment(sketch, "E1080", {"start": v(40.5, 24.66) * mm, "end": v(40.08, 24.54) * mm});
            skLineSegment(sketch, "E1081", {"start": v(40.08, 24.54) * mm, "end": v(39.65, 24.42) * mm});
            skLineSegment(sketch, "E1082", {"start": v(39.65, 24.42) * mm, "end": v(39.22, 24.3) * mm});
            skLineSegment(sketch, "E1083", {"start": v(39.22, 24.3) * mm, "end": v(38.79, 24.18) * mm});
            skLineSegment(sketch, "E1084", {"start": v(38.79, 24.18) * mm, "end": v(38.36, 24.06) * mm});
            skLineSegment(sketch, "E1085", {"start": v(38.36, 24.06) * mm, "end": v(37.93, 23.94) * mm});
            skLineSegment(sketch, "E1086", {"start": v(37.93, 23.94) * mm, "end": v(37.5, 23.82) * mm});
            skLineSegment(sketch, "E1087", {"start": v(37.5, 23.82) * mm, "end": v(37.07, 23.7) * mm});
            skLineSegment(sketch, "E1088", {"start": v(37.07, 23.7) * mm, "end": v(36.64, 23.58) * mm});
            skLineSegment(sketch, "E1089", {"start": v(36.64, 23.58) * mm, "end": v(36.21, 23.46) * mm});
            skLineSegment(sketch, "E1090", {"start": v(36.21, 23.46) * mm, "end": v(35.8, 23.34) * mm});
            skLineSegment(sketch, "E1091", {"start": v(35.8, 23.34) * mm, "end": v(35.52, 23.7) * mm});
            skLineSegment(sketch, "E1092", {"start": v(35.52, 23.7) * mm, "end": v(35.26, 24.05) * mm});
            skLineSegment(sketch, "E1093", {"start": v(35.26, 24.05) * mm, "end": v(34.99, 24.4) * mm});
            skLineSegment(sketch, "E1094", {"start": v(34.99, 24.4) * mm, "end": v(34.72, 24.76) * mm});
            skLineSegment(sketch, "E1095", {"start": v(34.72, 24.76) * mm, "end": v(34.45, 25.12) * mm});
            skLineSegment(sketch, "E1096", {"start": v(34.45, 25.12) * mm, "end": v(34.18, 25.47) * mm});
            skLineSegment(sketch, "E1097", {"start": v(34.18, 25.47) * mm, "end": v(33.9, 25.83) * mm});
            skLineSegment(sketch, "E1098", {"start": v(33.9, 25.83) * mm, "end": v(33.64, 26.18) * mm});
            skLineSegment(sketch, "E1099", {"start": v(33.64, 26.18) * mm, "end": v(33.37, 26.54) * mm});
            skLineSegment(sketch, "E1100", {"start": v(33.37, 26.54) * mm, "end": v(33.1, 26.9) * mm});
            skLineSegment(sketch, "E1101", {"start": v(33.1, 26.9) * mm, "end": v(32.83, 27.25) * mm});
            skLineSegment(sketch, "E1102", {"start": v(32.83, 27.25) * mm, "end": v(32.56, 27.6) * mm});
            skLineSegment(sketch, "E1103", {"start": v(32.56, 27.6) * mm, "end": v(32.29, 27.95) * mm});
            skLineSegment(sketch, "E1104", {"start": v(32.29, 27.95) * mm, "end": v(32.08, 28.23) * mm});
            skLineSegment(sketch, "E1105", {"start": v(32.08, 28.23) * mm, "end": v(32.43, 28.5) * mm});
            skLineSegment(sketch, "E1106", {"start": v(32.43, 28.5) * mm, "end": v(32.78, 28.79) * mm});
            skLineSegment(sketch, "E1107", {"start": v(32.78, 28.79) * mm, "end": v(33.12, 29.07) * mm});
            skLineSegment(sketch, "E1108", {"start": v(33.12, 29.07) * mm, "end": v(33.47, 29.35) * mm});
            skLineSegment(sketch, "E1109", {"start": v(33.47, 29.35) * mm, "end": v(33.82, 29.63) * mm});
            skLineSegment(sketch, "E1110", {"start": v(33.82, 29.63) * mm, "end": v(34.16, 29.9) * mm});
            skLineSegment(sketch, "E1111", {"start": v(34.16, 29.9) * mm, "end": v(34.5, 30.19) * mm});
            skLineSegment(sketch, "E1112", {"start": v(34.5, 30.19) * mm, "end": v(34.85, 30.47) * mm});
            skLineSegment(sketch, "E1113", {"start": v(34.85, 30.47) * mm, "end": v(35.2, 30.75) * mm});
            skLineSegment(sketch, "E1114", {"start": v(35.2, 30.75) * mm, "end": v(35.55, 31.03) * mm});
            skLineSegment(sketch, "E1115", {"start": v(35.55, 31.03) * mm, "end": v(35.9, 31.31) * mm});
            skLineSegment(sketch, "E1116", {"start": v(35.9, 31.31) * mm, "end": v(36.24, 31.6) * mm});
            skLineSegment(sketch, "E1117", {"start": v(36.24, 31.6) * mm, "end": v(36.59, 31.87) * mm});
            skLineSegment(sketch, "E1118", {"start": v(36.59, 31.87) * mm, "end": v(36.93, 32.15) * mm});
            skLineSegment(sketch, "E1119", {"start": v(36.93, 32.15) * mm, "end": v(37.28, 32.43) * mm});
            skLineSegment(sketch, "E1120", {"start": v(37.28, 32.43) * mm, "end": v(37.62, 32.71) * mm});
            skLineSegment(sketch, "E1121", {"start": v(37.62, 32.71) * mm, "end": v(37.74, 32.8) * mm});
            skLineSegment(sketch, "E1122", {"start": v(37.74, 32.8) * mm, "end": v(37.44, 33.14) * mm});
            skLineSegment(sketch, "E1123", {"start": v(37.44, 33.14) * mm, "end": v(37.14, 33.47) * mm});
            skLineSegment(sketch, "E1124", {"start": v(37.14, 33.47) * mm, "end": v(36.86, 33.78) * mm});
            skLineSegment(sketch, "E1125", {"start": v(36.86, 33.78) * mm, "end": v(36.47, 33.57) * mm});
            skLineSegment(sketch, "E1126", {"start": v(36.47, 33.57) * mm, "end": v(36.07, 33.37) * mm});
            skLineSegment(sketch, "E1127", {"start": v(36.07, 33.37) * mm, "end": v(35.68, 33.16) * mm});
            skLineSegment(sketch, "E1128", {"start": v(35.68, 33.16) * mm, "end": v(35.28, 32.95) * mm});
            skLineSegment(sketch, "E1129", {"start": v(35.28, 32.95) * mm, "end": v(34.89, 32.75) * mm});
            skLineSegment(sketch, "E1130", {"start": v(34.89, 32.75) * mm, "end": v(34.5, 32.54) * mm});
            skLineSegment(sketch, "E1131", {"start": v(34.5, 32.54) * mm, "end": v(34.1, 32.33) * mm});
            skLineSegment(sketch, "E1132", {"start": v(34.1, 32.33) * mm, "end": v(33.7, 32.13) * mm});
            skLineSegment(sketch, "E1133", {"start": v(33.7, 32.13) * mm, "end": v(33.3, 31.92) * mm});
            skLineSegment(sketch, "E1134", {"start": v(33.3, 31.92) * mm, "end": v(32.91, 31.71) * mm});
            skLineSegment(sketch, "E1135", {"start": v(32.91, 31.71) * mm, "end": v(32.52, 31.5) * mm});
            skLineSegment(sketch, "E1136", {"start": v(32.52, 31.5) * mm, "end": v(32.12, 31.3) * mm});
            skLineSegment(sketch, "E1137", {"start": v(32.12, 31.3) * mm, "end": v(31.73, 31.1) * mm});
            skLineSegment(sketch, "E1138", {"start": v(31.73, 31.1) * mm, "end": v(31.34, 30.89) * mm});
            skLineSegment(sketch, "E1139", {"start": v(31.34, 30.89) * mm, "end": v(30.94, 30.68) * mm});
            skLineSegment(sketch, "E1140", {"start": v(30.94, 30.68) * mm, "end": v(30.55, 30.48) * mm});
            skLineSegment(sketch, "E1141", {"start": v(30.55, 30.48) * mm, "end": v(30.16, 30.27) * mm});
            skLineSegment(sketch, "E1142", {"start": v(30.16, 30.27) * mm, "end": v(29.82, 30.57) * mm});
            skLineSegment(sketch, "E1143", {"start": v(29.82, 30.57) * mm, "end": v(29.48, 30.86) * mm});
            skLineSegment(sketch, "E1144", {"start": v(29.48, 30.86) * mm, "end": v(29.15, 31.15) * mm});
            skLineSegment(sketch, "E1145", {"start": v(29.15, 31.15) * mm, "end": v(28.8, 31.44) * mm});
            skLineSegment(sketch, "E1146", {"start": v(28.8, 31.44) * mm, "end": v(28.47, 31.73) * mm});
            skLineSegment(sketch, "E1147", {"start": v(28.47, 31.73) * mm, "end": v(28.13, 32.02) * mm});
            skLineSegment(sketch, "E1148", {"start": v(28.13, 32.02) * mm, "end": v(27.8, 32.31) * mm});
            skLineSegment(sketch, "E1149", {"start": v(27.8, 32.31) * mm, "end": v(27.46, 32.6) * mm});
            skLineSegment(sketch, "E1150", {"start": v(27.46, 32.6) * mm, "end": v(27.12, 32.9) * mm});
            skLineSegment(sketch, "E1151", {"start": v(27.12, 32.9) * mm, "end": v(26.78, 33.18) * mm});
            skLineSegment(sketch, "E1152", {"start": v(26.78, 33.18) * mm, "end": v(26.45, 33.48) * mm});
            skLineSegment(sketch, "E1153", {"start": v(26.45, 33.48) * mm, "end": v(26.1, 33.77) * mm});
            skLineSegment(sketch, "E1154", {"start": v(26.1, 33.77) * mm, "end": v(25.77, 34.06) * mm});
            skLineSegment(sketch, "E1155", {"start": v(25.77, 34.06) * mm, "end": v(25.51, 34.28) * mm});
            skLineSegment(sketch, "E1156", {"start": v(25.51, 34.28) * mm, "end": v(25.8, 34.63) * mm});
            skLineSegment(sketch, "E1157", {"start": v(25.8, 34.63) * mm, "end": v(26.07, 34.97) * mm});
            skLineSegment(sketch, "E1158", {"start": v(26.07, 34.97) * mm, "end": v(26.36, 35.32) * mm});
            skLineSegment(sketch, "E1159", {"start": v(26.36, 35.32) * mm, "end": v(26.64, 35.67) * mm});
            skLineSegment(sketch, "E1160", {"start": v(26.64, 35.67) * mm, "end": v(26.92, 36.01) * mm});
            skLineSegment(sketch, "E1161", {"start": v(26.92, 36.01) * mm, "end": v(27.2, 36.36) * mm});
            skLineSegment(sketch, "E1162", {"start": v(27.2, 36.36) * mm, "end": v(27.48, 36.7) * mm});
            skLineSegment(sketch, "E1163", {"start": v(27.48, 36.7) * mm, "end": v(27.76, 37.05) * mm});
            skLineSegment(sketch, "E1164", {"start": v(27.76, 37.05) * mm, "end": v(28.04, 37.4) * mm});
            skLineSegment(sketch, "E1165", {"start": v(28.04, 37.4) * mm, "end": v(28.32, 37.74) * mm});
            skLineSegment(sketch, "E1166", {"start": v(28.32, 37.74) * mm, "end": v(28.6, 38.09) * mm});
            skLineSegment(sketch, "E1167", {"start": v(28.6, 38.09) * mm, "end": v(28.88, 38.44) * mm});
            skLineSegment(sketch, "E1168", {"start": v(28.88, 38.44) * mm, "end": v(29.16, 38.78) * mm});
            skLineSegment(sketch, "E1169", {"start": v(29.16, 38.78) * mm, "end": v(29.44, 39.13) * mm});
            skLineSegment(sketch, "E1170", {"start": v(29.44, 39.13) * mm, "end": v(29.72, 39.47) * mm});
            skLineSegment(sketch, "E1171", {"start": v(29.72, 39.47) * mm, "end": v(30, 39.82) * mm});
            skLineSegment(sketch, "E1172", {"start": v(30, 39.82) * mm, "end": v(30.1, 39.93) * mm});
            skLineSegment(sketch, "E1173", {"start": v(30.1, 39.93) * mm, "end": v(29.73, 40.2) * mm});
            skLineSegment(sketch, "E1174", {"start": v(29.73, 40.2) * mm, "end": v(29.37, 40.46) * mm});
            skLineSegment(sketch, "E1175", {"start": v(29.37, 40.46) * mm, "end": v(29.04, 40.7) * mm});
            skLineSegment(sketch, "E1176", {"start": v(29.04, 40.7) * mm, "end": v(28.7, 40.42) * mm});
            skLineSegment(sketch, "E1177", {"start": v(28.7, 40.42) * mm, "end": v(28.35, 40.14) * mm});
            skLineSegment(sketch, "E1178", {"start": v(28.35, 40.14) * mm, "end": v(28, 39.85) * mm});
            skLineSegment(sketch, "E1179", {"start": v(28, 39.85) * mm, "end": v(27.66, 39.57) * mm});
            skLineSegment(sketch, "E1180", {"start": v(27.66, 39.57) * mm, "end": v(27.32, 39.29) * mm});
            skLineSegment(sketch, "E1181", {"start": v(27.32, 39.29) * mm, "end": v(26.98, 39) * mm});
            skLineSegment(sketch, "E1182", {"start": v(26.98, 39) * mm, "end": v(26.63, 38.72) * mm});
            skLineSegment(sketch, "E1183", {"start": v(26.63, 38.72) * mm, "end": v(26.29, 38.43) * mm});
            skLineSegment(sketch, "E1184", {"start": v(26.29, 38.43) * mm, "end": v(25.94, 38.15) * mm});
            skLineSegment(sketch, "E1185", {"start": v(25.94, 38.15) * mm, "end": v(25.6, 37.87) * mm});
            skLineSegment(sketch, "E1186", {"start": v(25.6, 37.87) * mm, "end": v(25.26, 37.58) * mm});
            skLineSegment(sketch, "E1187", {"start": v(25.26, 37.58) * mm, "end": v(24.91, 37.3) * mm});
            skLineSegment(sketch, "E1188", {"start": v(24.91, 37.3) * mm, "end": v(24.57, 37.01) * mm});
            skLineSegment(sketch, "E1189", {"start": v(24.57, 37.01) * mm, "end": v(24.23, 36.73) * mm});
            skLineSegment(sketch, "E1190", {"start": v(24.23, 36.73) * mm, "end": v(23.88, 36.44) * mm});
            skLineSegment(sketch, "E1191", {"start": v(23.88, 36.44) * mm, "end": v(23.54, 36.16) * mm});
            skLineSegment(sketch, "E1192", {"start": v(23.54, 36.16) * mm, "end": v(23.2, 35.88) * mm});
            skLineSegment(sketch, "E1193", {"start": v(23.2, 35.88) * mm, "end": v(22.82, 36.1) * mm});
            skLineSegment(sketch, "E1194", {"start": v(22.82, 36.1) * mm, "end": v(22.42, 36.31) * mm});
            skLineSegment(sketch, "E1195", {"start": v(22.42, 36.31) * mm, "end": v(22.03, 36.53) * mm});
            skLineSegment(sketch, "E1196", {"start": v(22.03, 36.53) * mm, "end": v(21.64, 36.74) * mm});
            skLineSegment(sketch, "E1197", {"start": v(21.64, 36.74) * mm, "end": v(21.25, 36.96) * mm});
            skLineSegment(sketch, "E1198", {"start": v(21.25, 36.96) * mm, "end": v(20.86, 37.17) * mm});
            skLineSegment(sketch, "E1199", {"start": v(20.86, 37.17) * mm, "end": v(20.47, 37.38) * mm});
            skLineSegment(sketch, "E1200", {"start": v(20.47, 37.38) * mm, "end": v(20.08, 37.6) * mm});
            skLineSegment(sketch, "E1201", {"start": v(20.08, 37.6) * mm, "end": v(19.7, 37.81) * mm});
            skLineSegment(sketch, "E1202", {"start": v(19.7, 37.81) * mm, "end": v(19.3, 38.03) * mm});
            skLineSegment(sketch, "E1203", {"start": v(19.3, 38.03) * mm, "end": v(18.9, 38.24) * mm});
            skLineSegment(sketch, "E1204", {"start": v(18.9, 38.24) * mm, "end": v(18.52, 38.46) * mm});
            skLineSegment(sketch, "E1205", {"start": v(18.52, 38.46) * mm, "end": v(18.13, 38.67) * mm});
            skLineSegment(sketch, "E1206", {"start": v(18.13, 38.67) * mm, "end": v(17.83, 38.84) * mm});
            skLineSegment(sketch, "E1207", {"start": v(17.83, 38.84) * mm, "end": v(18.03, 39.23) * mm});
            skLineSegment(sketch, "E1208", {"start": v(18.03, 39.23) * mm, "end": v(18.23, 39.63) * mm});
            skLineSegment(sketch, "E1209", {"start": v(18.23, 39.63) * mm, "end": v(18.44, 40.03) * mm});
            skLineSegment(sketch, "E1210", {"start": v(18.44, 40.03) * mm, "end": v(18.64, 40.42) * mm});
            skLineSegment(sketch, "E1211", {"start": v(18.64, 40.42) * mm, "end": v(18.84, 40.82) * mm});
            skLineSegment(sketch, "E1212", {"start": v(18.84, 40.82) * mm, "end": v(19.04, 41.22) * mm});
            skLineSegment(sketch, "E1213", {"start": v(19.04, 41.22) * mm, "end": v(19.25, 41.61) * mm});
            skLineSegment(sketch, "E1214", {"start": v(19.25, 41.61) * mm, "end": v(19.45, 42.01) * mm});
            skLineSegment(sketch, "E1215", {"start": v(19.45, 42.01) * mm, "end": v(19.65, 42.4) * mm});
            skLineSegment(sketch, "E1216", {"start": v(19.65, 42.4) * mm, "end": v(19.85, 42.8) * mm});
            skLineSegment(sketch, "E1217", {"start": v(19.85, 42.8) * mm, "end": v(20.05, 43.2) * mm});
            skLineSegment(sketch, "E1218", {"start": v(20.05, 43.2) * mm, "end": v(20.26, 43.6) * mm});
            skLineSegment(sketch, "E1219", {"start": v(20.26, 43.6) * mm, "end": v(20.46, 44) * mm});
            skLineSegment(sketch, "E1220", {"start": v(20.46, 44) * mm, "end": v(20.66, 44.4) * mm});
            skLineSegment(sketch, "E1221", {"start": v(20.66, 44.4) * mm, "end": v(20.86, 44.8) * mm});
            skLineSegment(sketch, "E1222", {"start": v(20.86, 44.8) * mm, "end": v(21.07, 45.19) * mm});
            skLineSegment(sketch, "E1223", {"start": v(21.07, 45.19) * mm, "end": v(21.13, 45.32) * mm});
            skLineSegment(sketch, "E1224", {"start": v(21.13, 45.32) * mm, "end": v(20.72, 45.5) * mm});
            skLineSegment(sketch, "E1225", {"start": v(20.72, 45.5) * mm, "end": v(20.32, 45.68) * mm});
            skLineSegment(sketch, "E1226", {"start": v(20.32, 45.68) * mm, "end": v(19.94, 45.85) * mm});
            skLineSegment(sketch, "E1227", {"start": v(19.94, 45.85) * mm, "end": v(19.66, 45.5) * mm});
            skLineSegment(sketch, "E1228", {"start": v(19.66, 45.5) * mm, "end": v(19.38, 45.15) * mm});
            skLineSegment(sketch, "E1229", {"start": v(19.38, 45.15) * mm, "end": v(19.1, 44.8) * mm});
            skLineSegment(sketch, "E1230", {"start": v(19.1, 44.8) * mm, "end": v(18.83, 44.46) * mm});
            skLineSegment(sketch, "E1231", {"start": v(18.83, 44.46) * mm, "end": v(18.55, 44.1) * mm});
            skLineSegment(sketch, "E1232", {"start": v(18.55, 44.1) * mm, "end": v(18.28, 43.76) * mm});
            skLineSegment(sketch, "E1233", {"start": v(18.28, 43.76) * mm, "end": v(18, 43.4) * mm});
            skLineSegment(sketch, "E1234", {"start": v(18, 43.4) * mm, "end": v(17.72, 43.06) * mm});
            skLineSegment(sketch, "E1235", {"start": v(17.72, 43.06) * mm, "end": v(17.45, 42.7) * mm});
            skLineSegment(sketch, "E1236", {"start": v(17.45, 42.7) * mm, "end": v(17.17, 42.36) * mm});
            skLineSegment(sketch, "E1237", {"start": v(17.17, 42.36) * mm, "end": v(16.9, 42.01) * mm});
            skLineSegment(sketch, "E1238", {"start": v(16.9, 42.01) * mm, "end": v(16.62, 41.66) * mm});
            skLineSegment(sketch, "E1239", {"start": v(16.62, 41.66) * mm, "end": v(16.34, 41.31) * mm});
            skLineSegment(sketch, "E1240", {"start": v(16.34, 41.31) * mm, "end": v(16.06, 40.96) * mm});
            skLineSegment(sketch, "E1241", {"start": v(16.06, 40.96) * mm, "end": v(15.79, 40.61) * mm});
            skLineSegment(sketch, "E1242", {"start": v(15.79, 40.61) * mm, "end": v(15.5, 40.27) * mm});
            skLineSegment(sketch, "E1243", {"start": v(15.5, 40.27) * mm, "end": v(15.24, 39.92) * mm});
            skLineSegment(sketch, "E1244", {"start": v(15.24, 39.92) * mm, "end": v(14.81, 40.05) * mm});
            skLineSegment(sketch, "E1245", {"start": v(14.81, 40.05) * mm, "end": v(14.38, 40.18) * mm});
            skLineSegment(sketch, "E1246", {"start": v(14.38, 40.18) * mm, "end": v(13.96, 40.3) * mm});
            skLineSegment(sketch, "E1247", {"start": v(13.96, 40.3) * mm, "end": v(13.53, 40.44) * mm});
            skLineSegment(sketch, "E1248", {"start": v(13.53, 40.44) * mm, "end": v(13.1, 40.57) * mm});
            skLineSegment(sketch, "E1249", {"start": v(13.1, 40.57) * mm, "end": v(12.68, 40.7) * mm});
            skLineSegment(sketch, "E1250", {"start": v(12.68, 40.7) * mm, "end": v(12.25, 40.82) * mm});
            skLineSegment(sketch, "E1251", {"start": v(12.25, 40.82) * mm, "end": v(11.82, 40.95) * mm});
            skLineSegment(sketch, "E1252", {"start": v(11.82, 40.95) * mm, "end": v(11.4, 41.08) * mm});
            skLineSegment(sketch, "E1253", {"start": v(11.4, 41.08) * mm, "end": v(10.97, 41.2) * mm});
            skLineSegment(sketch, "E1254", {"start": v(10.97, 41.2) * mm, "end": v(10.54, 41.34) * mm});
            skLineSegment(sketch, "E1255", {"start": v(10.54, 41.34) * mm, "end": v(10.12, 41.47) * mm});
            skLineSegment(sketch, "E1256", {"start": v(10.12, 41.47) * mm, "end": v(9.7, 41.6) * mm});
            skLineSegment(sketch, "E1257", {"start": v(9.7, 41.6) * mm, "end": v(9.37, 41.7) * mm});
            skLineSegment(sketch, "E1258", {"start": v(9.37, 41.7) * mm, "end": v(9.48, 42.12) * mm});
            skLineSegment(sketch, "E1259", {"start": v(9.48, 42.12) * mm, "end": v(9.6, 42.55) * mm});
            skLineSegment(sketch, "E1260", {"start": v(9.6, 42.55) * mm, "end": v(9.71, 42.99) * mm});
            skLineSegment(sketch, "E1261", {"start": v(9.71, 42.99) * mm, "end": v(9.83, 43.42) * mm});
            skLineSegment(sketch, "E1262", {"start": v(9.83, 43.42) * mm, "end": v(9.94, 43.85) * mm});
            skLineSegment(sketch, "E1263", {"start": v(9.94, 43.85) * mm, "end": v(10.06, 44.28) * mm});
            skLineSegment(sketch, "E1264", {"start": v(10.06, 44.28) * mm, "end": v(10.17, 44.7) * mm});
            skLineSegment(sketch, "E1265", {"start": v(10.17, 44.7) * mm, "end": v(10.29, 45.14) * mm});
            skLineSegment(sketch, "E1266", {"start": v(10.29, 45.14) * mm, "end": v(10.4, 45.57) * mm});
            skLineSegment(sketch, "E1267", {"start": v(10.4, 45.57) * mm, "end": v(10.52, 46) * mm});
            skLineSegment(sketch, "E1268", {"start": v(10.52, 46) * mm, "end": v(10.63, 46.43) * mm});
            skLineSegment(sketch, "E1269", {"start": v(10.63, 46.43) * mm, "end": v(10.75, 46.86) * mm});
            skLineSegment(sketch, "E1270", {"start": v(10.75, 46.86) * mm, "end": v(10.86, 47.29) * mm});
            skLineSegment(sketch, "E1271", {"start": v(10.86, 47.29) * mm, "end": v(10.98, 47.72) * mm});
            skLineSegment(sketch, "E1272", {"start": v(10.98, 47.72) * mm, "end": v(11.1, 48.15) * mm});
            skLineSegment(sketch, "E1273", {"start": v(11.1, 48.15) * mm, "end": v(11.21, 48.58) * mm});
            skLineSegment(sketch, "E1274", {"start": v(11.21, 48.58) * mm, "end": v(11.25, 48.72) * mm});
            skLineSegment(sketch, "E1275", {"start": v(11.25, 48.72) * mm, "end": v(10.81, 48.81) * mm});
            skLineSegment(sketch, "E1276", {"start": v(10.81, 48.81) * mm, "end": v(10.38, 48.9) * mm});
            skLineSegment(sketch, "E1277", {"start": v(10.38, 48.9) * mm, "end": v(9.97, 49) * mm});
            skLineSegment(sketch, "E1278", {"start": v(9.97, 49) * mm, "end": v(9.77, 48.6) * mm});
            skLineSegment(sketch, "E1279", {"start": v(9.77, 48.6) * mm, "end": v(9.57, 48.2) * mm});
            skLineSegment(sketch, "E1280", {"start": v(9.57, 48.2) * mm, "end": v(9.37, 47.8) * mm});
            skLineSegment(sketch, "E1281", {"start": v(9.37, 47.8) * mm, "end": v(9.18, 47.4) * mm});
            skLineSegment(sketch, "E1282", {"start": v(9.18, 47.4) * mm, "end": v(8.98, 47) * mm});
            skLineSegment(sketch, "E1283", {"start": v(8.98, 47) * mm, "end": v(8.78, 46.6) * mm});
            skLineSegment(sketch, "E1284", {"start": v(8.78, 46.6) * mm, "end": v(8.58, 46.2) * mm});
            skLineSegment(sketch, "E1285", {"start": v(8.58, 46.2) * mm, "end": v(8.38, 45.8) * mm});
            skLineSegment(sketch, "E1286", {"start": v(8.38, 45.8) * mm, "end": v(8.19, 45.4) * mm});
            skLineSegment(sketch, "E1287", {"start": v(8.19, 45.4) * mm, "end": v(7.99, 45) * mm});
            skLineSegment(sketch, "E1288", {"start": v(7.99, 45) * mm, "end": v(7.79, 44.6) * mm});
            skLineSegment(sketch, "E1289", {"start": v(7.79, 44.6) * mm, "end": v(7.6, 44.2) * mm});
            skLineSegment(sketch, "E1290", {"start": v(7.6, 44.2) * mm, "end": v(7.4, 43.8) * mm});
            skLineSegment(sketch, "E1291", {"start": v(7.4, 43.8) * mm, "end": v(7.2, 43.4) * mm});
            skLineSegment(sketch, "E1292", {"start": v(7.2, 43.4) * mm, "end": v(7, 43) * mm});
            skLineSegment(sketch, "E1293", {"start": v(7, 43) * mm, "end": v(6.8, 42.6) * mm});
            skLineSegment(sketch, "E1294", {"start": v(6.8, 42.6) * mm, "end": v(6.6, 42.22) * mm});
            skLineSegment(sketch, "E1295", {"start": v(6.6, 42.22) * mm, "end": v(6.16, 42.26) * mm});
            skLineSegment(sketch, "E1296", {"start": v(6.16, 42.26) * mm, "end": v(5.72, 42.3) * mm});
            skLineSegment(sketch, "E1297", {"start": v(5.72, 42.3) * mm, "end": v(5.27, 42.33) * mm});
            skLineSegment(sketch, "E1298", {"start": v(5.27, 42.33) * mm, "end": v(4.83, 42.37) * mm});
            skLineSegment(sketch, "E1299", {"start": v(4.83, 42.37) * mm, "end": v(4.38, 42.4) * mm});
            skLineSegment(sketch, "E1300", {"start": v(4.38, 42.4) * mm, "end": v(3.94, 42.44) * mm});
            skLineSegment(sketch, "E1301", {"start": v(3.94, 42.44) * mm, "end": v(3.5, 42.48) * mm});
            skLineSegment(sketch, "E1302", {"start": v(3.5, 42.48) * mm, "end": v(3.05, 42.52) * mm});
            skLineSegment(sketch, "E1303", {"start": v(3.05, 42.52) * mm, "end": v(2.6, 42.55) * mm});
            skLineSegment(sketch, "E1304", {"start": v(2.6, 42.55) * mm, "end": v(2.16, 42.6) * mm});
            skLineSegment(sketch, "E1305", {"start": v(2.16, 42.6) * mm, "end": v(1.72, 42.63) * mm});
            skLineSegment(sketch, "E1306", {"start": v(1.72, 42.63) * mm, "end": v(1.28, 42.66) * mm});
            skLineSegment(sketch, "E1307", {"start": v(1.28, 42.66) * mm, "end": v(0.83, 42.7) * mm});
            skLineSegment(sketch, "E1308", {"start": v(0.83, 42.7) * mm, "end": v(0.5, 42.73) * mm});
            skLineSegment(sketch, "E1309", {"start": v(0.5, 42.73) * mm, "end": v(0.52, 43.17) * mm});
            skLineSegment(sketch, "E1310", {"start": v(0.52, 43.17) * mm, "end": v(0.54, 43.62) * mm});
            skLineSegment(sketch, "E1311", {"start": v(0.54, 43.62) * mm, "end": v(0.56, 44.06) * mm});
            skLineSegment(sketch, "E1312", {"start": v(0.56, 44.06) * mm, "end": v(0.59, 44.5) * mm});
            skLineSegment(sketch, "E1313", {"start": v(0.59, 44.5) * mm, "end": v(0.6, 44.95) * mm});
            skLineSegment(sketch, "E1314", {"start": v(0.6, 44.95) * mm, "end": v(0.63, 45.4) * mm});
            skLineSegment(sketch, "E1315", {"start": v(0.63, 45.4) * mm, "end": v(0.66, 45.84) * mm});
            skLineSegment(sketch, "E1316", {"start": v(0.66, 45.84) * mm, "end": v(0.68, 46.29) * mm});
            skLineSegment(sketch, "E1317", {"start": v(0.68, 46.29) * mm, "end": v(0.7, 46.73) * mm});
            skLineSegment(sketch, "E1318", {"start": v(0.7, 46.73) * mm, "end": v(0.73, 47.18) * mm});
            skLineSegment(sketch, "E1319", {"start": v(0.73, 47.18) * mm, "end": v(0.75, 47.62) * mm});
            skLineSegment(sketch, "E1320", {"start": v(0.75, 47.62) * mm, "end": v(0.77, 48.07) * mm});
            skLineSegment(sketch, "E1321", {"start": v(0.77, 48.07) * mm, "end": v(0.8, 48.52) * mm});
            skLineSegment(sketch, "E1322", {"start": v(0.8, 48.52) * mm, "end": v(0.82, 48.96) * mm});
            skLineSegment(sketch, "E1323", {"start": v(0.82, 48.96) * mm, "end": v(0.84, 49.4) * mm});
            skLineSegment(sketch, "E1324", {"start": v(0.84, 49.4) * mm, "end": v(0.87, 49.85) * mm});
            skLineSegment(sketch, "E1325", {"start": v(0.87, 49.85) * mm, "end": v(0.87, 50) * mm});
            skLineSegment(sketch, "E1326", {"start": v(0.87, 50) * mm, "end": v(0.43, 50) * mm});
            skLineSegment(sketch, "E1327", {"start": v(0.43, 50) * mm, "end": v(-0.02, 50) * mm});
            skLineSegment(sketch, "E1328", {"start": v(-0.02, 50) * mm, "end": v(-0.44, 50) * mm});
            skLineSegment(sketch, "E1329", {"start": v(-0.44, 50) * mm, "end": v(-0.55, 49.57) * mm});
            skLineSegment(sketch, "E1330", {"start": v(-0.55, 49.57) * mm, "end": v(-0.66, 49.13) * mm});
            skLineSegment(sketch, "E1331", {"start": v(-0.66, 49.13) * mm, "end": v(-0.77, 48.7) * mm});
            skLineSegment(sketch, "E1332", {"start": v(-0.77, 48.7) * mm, "end": v(-0.88, 48.27) * mm});
            skLineSegment(sketch, "E1333", {"start": v(-0.88, 48.27) * mm, "end": v(-1, 47.84) * mm});
            skLineSegment(sketch, "E1334", {"start": v(-1, 47.84) * mm, "end": v(-1.1, 47.4) * mm});
            skLineSegment(sketch, "E1335", {"start": v(-1.1, 47.4) * mm, "end": v(-1.21, 46.98) * mm});
            skLineSegment(sketch, "E1336", {"start": v(-1.21, 46.98) * mm, "end": v(-1.32, 46.55) * mm});
            skLineSegment(sketch, "E1337", {"start": v(-1.32, 46.55) * mm, "end": v(-1.43, 46.11) * mm});
            skLineSegment(sketch, "E1338", {"start": v(-1.43, 46.11) * mm, "end": v(-1.54, 45.68) * mm});
            skLineSegment(sketch, "E1339", {"start": v(-1.54, 45.68) * mm, "end": v(-1.66, 45.25) * mm});
            skLineSegment(sketch, "E1340", {"start": v(-1.66, 45.25) * mm, "end": v(-1.77, 44.82) * mm});
            skLineSegment(sketch, "E1341", {"start": v(-1.77, 44.82) * mm, "end": v(-1.88, 44.39) * mm});
            skLineSegment(sketch, "E1342", {"start": v(-1.88, 44.39) * mm, "end": v(-1.99, 43.96) * mm});
            skLineSegment(sketch, "E1343", {"start": v(-1.99, 43.96) * mm, "end": v(-2.1, 43.52) * mm});
            skLineSegment(sketch, "E1344", {"start": v(-2.1, 43.52) * mm, "end": v(-2.2, 43.1) * mm});
            skLineSegment(sketch, "E1345", {"start": v(-2.2, 43.1) * mm, "end": v(-2.32, 42.67) * mm});
            skLineSegment(sketch, "E1346", {"start": v(-2.32, 42.67) * mm, "end": v(-2.76, 42.61) * mm});
            skLineSegment(sketch, "E1347", {"start": v(-2.76, 42.61) * mm, "end": v(-3.2, 42.56) * mm});
            skLineSegment(sketch, "E1348", {"start": v(-3.2, 42.56) * mm, "end": v(-3.64, 42.5) * mm});
            skLineSegment(sketch, "E1349", {"start": v(-3.64, 42.5) * mm, "end": v(-4.09, 42.45) * mm});
            skLineSegment(sketch, "E1350", {"start": v(-4.09, 42.45) * mm, "end": v(-4.53, 42.39) * mm});
            skLineSegment(sketch, "E1351", {"start": v(-4.53, 42.39) * mm, "end": v(-4.97, 42.33) * mm});
            skLineSegment(sketch, "E1352", {"start": v(-4.97, 42.33) * mm, "end": v(-5.41, 42.28) * mm});
            skLineSegment(sketch, "E1353", {"start": v(-5.41, 42.28) * mm, "end": v(-5.85, 42.22) * mm});
            skLineSegment(sketch, "E1354", {"start": v(-5.85, 42.22) * mm, "end": v(-6.3, 42.17) * mm});
            skLineSegment(sketch, "E1355", {"start": v(-6.3, 42.17) * mm, "end": v(-6.74, 42.1) * mm});
            skLineSegment(sketch, "E1356", {"start": v(-6.74, 42.1) * mm, "end": v(-7.18, 42.05) * mm});
            skLineSegment(sketch, "E1357", {"start": v(-7.18, 42.05) * mm, "end": v(-7.62, 42) * mm});
            skLineSegment(sketch, "E1358", {"start": v(-7.62, 42) * mm, "end": v(-8.06, 41.94) * mm});
            skLineSegment(sketch, "E1359", {"start": v(-8.06, 41.94) * mm, "end": v(-8.4, 41.9) * mm});
            skLineSegment(sketch, "E1360", {"start": v(-8.4, 41.9) * mm, "end": v(-8.47, 42.34) * mm});
            skLineSegment(sketch, "E1361", {"start": v(-8.47, 42.34) * mm, "end": v(-8.54, 42.78) * mm});
            skLineSegment(sketch, "E1362", {"start": v(-8.54, 42.78) * mm, "end": v(-8.61, 43.22) * mm});
            skLineSegment(sketch, "E1363", {"start": v(-8.61, 43.22) * mm, "end": v(-8.68, 43.66) * mm});
            skLineSegment(sketch, "E1364", {"start": v(-8.68, 43.66) * mm, "end": v(-8.75, 44.1) * mm});
            skLineSegment(sketch, "E1365", {"start": v(-8.75, 44.1) * mm, "end": v(-8.82, 44.54) * mm});
            skLineSegment(sketch, "E1366", {"start": v(-8.82, 44.54) * mm, "end": v(-8.9, 44.98) * mm});
            skLineSegment(sketch, "E1367", {"start": v(-8.9, 44.98) * mm, "end": v(-8.96, 45.42) * mm});
            skLineSegment(sketch, "E1368", {"start": v(-8.96, 45.42) * mm, "end": v(-9.03, 45.86) * mm});
            skLineSegment(sketch, "E1369", {"start": v(-9.03, 45.86) * mm, "end": v(-9.1, 46.3) * mm});
            skLineSegment(sketch, "E1370", {"start": v(-9.1, 46.3) * mm, "end": v(-9.17, 46.74) * mm});
            skLineSegment(sketch, "E1371", {"start": v(-9.17, 46.74) * mm, "end": v(-9.24, 47.18) * mm});
            skLineSegment(sketch, "E1372", {"start": v(-9.24, 47.18) * mm, "end": v(-9.3, 47.62) * mm});
            skLineSegment(sketch, "E1373", {"start": v(-9.3, 47.62) * mm, "end": v(-9.38, 48.06) * mm});
            skLineSegment(sketch, "E1374", {"start": v(-9.38, 48.06) * mm, "end": v(-9.45, 48.5) * mm});
            skLineSegment(sketch, "E1375", {"start": v(-9.45, 48.5) * mm, "end": v(-9.52, 48.94) * mm});
            skLineSegment(sketch, "E1376", {"start": v(-9.52, 48.94) * mm, "end": v(-9.54, 49.08) * mm});
            skLineSegment(sketch, "E1377", {"start": v(-9.54, 49.08) * mm, "end": v(-9.98, 49) * mm});
            skLineSegment(sketch, "E1378", {"start": v(-9.98, 49) * mm, "end": v(-10.41, 48.9) * mm});
            skLineSegment(sketch, "E1379", {"start": v(-10.41, 48.9) * mm, "end": v(-10.82, 48.81) * mm});
            skLineSegment(sketch, "E1380", {"start": v(-10.82, 48.81) * mm, "end": v(-10.84, 48.37) * mm});
            skLineSegment(sketch, "E1381", {"start": v(-10.84, 48.37) * mm, "end": v(-10.86, 47.92) * mm});
            skLineSegment(sketch, "E1382", {"start": v(-10.86, 47.92) * mm, "end": v(-10.88, 47.48) * mm});
            skLineSegment(sketch, "E1383", {"start": v(-10.88, 47.48) * mm, "end": v(-10.9, 47.03) * mm});
            skLineSegment(sketch, "E1384", {"start": v(-10.9, 47.03) * mm, "end": v(-10.92, 46.59) * mm});
            skLineSegment(sketch, "E1385", {"start": v(-10.92, 46.59) * mm, "end": v(-10.93, 46.14) * mm});
            skLineSegment(sketch, "E1386", {"start": v(-10.93, 46.14) * mm, "end": v(-10.95, 45.7) * mm});
            skLineSegment(sketch, "E1387", {"start": v(-10.95, 45.7) * mm, "end": v(-10.97, 45.25) * mm});
            skLineSegment(sketch, "E1388", {"start": v(-10.97, 45.25) * mm, "end": v(-10.99, 44.8) * mm});
            skLineSegment(sketch, "E1389", {"start": v(-10.99, 44.8) * mm, "end": v(-11, 44.36) * mm});
            skLineSegment(sketch, "E1390", {"start": v(-11, 44.36) * mm, "end": v(-11.03, 43.92) * mm});
            skLineSegment(sketch, "E1391", {"start": v(-11.03, 43.92) * mm, "end": v(-11.05, 43.47) * mm});
            skLineSegment(sketch, "E1392", {"start": v(-11.05, 43.47) * mm, "end": v(-11.06, 43.03) * mm});
            skLineSegment(sketch, "E1393", {"start": v(-11.06, 43.03) * mm, "end": v(-11.08, 42.58) * mm});
            skLineSegment(sketch, "E1394", {"start": v(-11.08, 42.58) * mm, "end": v(-11.1, 42.14) * mm});
            skLineSegment(sketch, "E1395", {"start": v(-11.1, 42.14) * mm, "end": v(-11.12, 41.7) * mm});
            skLineSegment(sketch, "E1396", {"start": v(-11.12, 41.7) * mm, "end": v(-11.14, 41.26) * mm});
            skLineSegment(sketch, "E1397", {"start": v(-11.14, 41.26) * mm, "end": v(-11.56, 41.1) * mm});
            skLineSegment(sketch, "E1398", {"start": v(-11.56, 41.1) * mm, "end": v(-11.98, 40.96) * mm});
            skLineSegment(sketch, "E1399", {"start": v(-11.98, 40.96) * mm, "end": v(-12.4, 40.82) * mm});
            skLineSegment(sketch, "E1400", {"start": v(-12.4, 40.82) * mm, "end": v(-12.82, 40.67) * mm});
            skLineSegment(sketch, "E1401", {"start": v(-12.82, 40.67) * mm, "end": v(-13.24, 40.52) * mm});
            skLineSegment(sketch, "E1402", {"start": v(-13.24, 40.52) * mm, "end": v(-13.66, 40.38) * mm});
            skLineSegment(sketch, "E1403", {"start": v(-13.66, 40.38) * mm, "end": v(-14.08, 40.23) * mm});
            skLineSegment(sketch, "E1404", {"start": v(-14.08, 40.23) * mm, "end": v(-14.5, 40.08) * mm});
            skLineSegment(sketch, "E1405", {"start": v(-14.5, 40.08) * mm, "end": v(-14.93, 39.93) * mm});
            skLineSegment(sketch, "E1406", {"start": v(-14.93, 39.93) * mm, "end": v(-15.35, 39.79) * mm});
            skLineSegment(sketch, "E1407", {"start": v(-15.35, 39.79) * mm, "end": v(-15.77, 39.64) * mm});
            skLineSegment(sketch, "E1408", {"start": v(-15.77, 39.64) * mm, "end": v(-16.19, 39.5) * mm});
            skLineSegment(sketch, "E1409", {"start": v(-16.19, 39.5) * mm, "end": v(-16.6, 39.35) * mm});
            skLineSegment(sketch, "E1410", {"start": v(-16.6, 39.35) * mm, "end": v(-16.93, 39.24) * mm});
            skLineSegment(sketch, "E1411", {"start": v(-16.93, 39.24) * mm, "end": v(-17.09, 39.65) * mm});
            skLineSegment(sketch, "E1412", {"start": v(-17.09, 39.65) * mm, "end": v(-17.25, 40.07) * mm});
            skLineSegment(sketch, "E1413", {"start": v(-17.25, 40.07) * mm, "end": v(-17.4, 40.48) * mm});
            skLineSegment(sketch, "E1414", {"start": v(-17.4, 40.48) * mm, "end": v(-17.57, 40.9) * mm});
            skLineSegment(sketch, "E1415", {"start": v(-17.57, 40.9) * mm, "end": v(-17.73, 41.32) * mm});
            skLineSegment(sketch, "E1416", {"start": v(-17.73, 41.32) * mm, "end": v(-17.89, 41.73) * mm});
            skLineSegment(sketch, "E1417", {"start": v(-17.89, 41.73) * mm, "end": v(-18.05, 42.15) * mm});
            skLineSegment(sketch, "E1418", {"start": v(-18.05, 42.15) * mm, "end": v(-18.2, 42.56) * mm});
            skLineSegment(sketch, "E1419", {"start": v(-18.2, 42.56) * mm, "end": v(-18.37, 42.98) * mm});
            skLineSegment(sketch, "E1420", {"start": v(-18.37, 42.98) * mm, "end": v(-18.53, 43.4) * mm});
            skLineSegment(sketch, "E1421", {"start": v(-18.53, 43.4) * mm, "end": v(-18.69, 43.81) * mm});
            skLineSegment(sketch, "E1422", {"start": v(-18.69, 43.81) * mm, "end": v(-18.85, 44.23) * mm});
            skLineSegment(sketch, "E1423", {"start": v(-18.85, 44.23) * mm, "end": v(-19, 44.64) * mm});
            skLineSegment(sketch, "E1424", {"start": v(-19, 44.64) * mm, "end": v(-19.17, 45.06) * mm});
            skLineSegment(sketch, "E1425", {"start": v(-19.17, 45.06) * mm, "end": v(-19.33, 45.48) * mm});
            skLineSegment(sketch, "E1426", {"start": v(-19.33, 45.48) * mm, "end": v(-19.49, 45.9) * mm});
            skLineSegment(sketch, "E1427", {"start": v(-19.49, 45.9) * mm, "end": v(-19.54, 46.03) * mm});
            skLineSegment(sketch, "E1428", {"start": v(-19.54, 46.03) * mm, "end": v(-19.94, 45.85) * mm});
            skLineSegment(sketch, "E1429", {"start": v(-19.94, 45.85) * mm, "end": v(-20.35, 45.67) * mm});
            skLineSegment(sketch, "E1430", {"start": v(-20.35, 45.67) * mm, "end": v(-20.73, 45.5) * mm});
            skLineSegment(sketch, "E1431", {"start": v(-20.73, 45.5) * mm, "end": v(-20.66, 45.06) * mm});
            skLineSegment(sketch, "E1432", {"start": v(-20.66, 45.06) * mm, "end": v(-20.59, 44.62) * mm});
            skLineSegment(sketch, "E1433", {"start": v(-20.59, 44.62) * mm, "end": v(-20.51, 44.18) * mm});
            skLineSegment(sketch, "E1434", {"start": v(-20.51, 44.18) * mm, "end": v(-20.44, 43.74) * mm});
            skLineSegment(sketch, "E1435", {"start": v(-20.44, 43.74) * mm, "end": v(-20.36, 43.3) * mm});
            skLineSegment(sketch, "E1436", {"start": v(-20.36, 43.3) * mm, "end": v(-20.29, 42.86) * mm});
            skLineSegment(sketch, "E1437", {"start": v(-20.29, 42.86) * mm, "end": v(-20.21, 42.42) * mm});
            skLineSegment(sketch, "E1438", {"start": v(-20.21, 42.42) * mm, "end": v(-20.14, 41.98) * mm});
            skLineSegment(sketch, "E1439", {"start": v(-20.14, 41.98) * mm, "end": v(-20.07, 41.54) * mm});
            skLineSegment(sketch, "E1440", {"start": v(-20.07, 41.54) * mm, "end": v(-20, 41.1) * mm});
            skLineSegment(sketch, "E1441", {"start": v(-20, 41.1) * mm, "end": v(-19.92, 40.66) * mm});
            skLineSegment(sketch, "E1442", {"start": v(-19.92, 40.66) * mm, "end": v(-19.84, 40.23) * mm});
            skLineSegment(sketch, "E1443", {"start": v(-19.84, 40.23) * mm, "end": v(-19.77, 39.79) * mm});
            skLineSegment(sketch, "E1444", {"start": v(-19.77, 39.79) * mm, "end": v(-19.7, 39.35) * mm});
            skLineSegment(sketch, "E1445", {"start": v(-19.7, 39.35) * mm, "end": v(-19.62, 38.9) * mm});
            skLineSegment(sketch, "E1446", {"start": v(-19.62, 38.9) * mm, "end": v(-19.55, 38.47) * mm});
            skLineSegment(sketch, "E1447", {"start": v(-19.55, 38.47) * mm, "end": v(-19.47, 38.04) * mm});
            skLineSegment(sketch, "E1448", {"start": v(-19.47, 38.04) * mm, "end": v(-19.85, 37.8) * mm});
            skLineSegment(sketch, "E1449", {"start": v(-19.85, 37.8) * mm, "end": v(-20.23, 37.58) * mm});
            skLineSegment(sketch, "E1450", {"start": v(-20.23, 37.58) * mm, "end": v(-20.62, 37.35) * mm});
            skLineSegment(sketch, "E1451", {"start": v(-20.62, 37.35) * mm, "end": v(-21, 37.11) * mm});
            skLineSegment(sketch, "E1452", {"start": v(-21, 37.11) * mm, "end": v(-21.38, 36.88) * mm});
            skLineSegment(sketch, "E1453", {"start": v(-21.38, 36.88) * mm, "end": v(-21.76, 36.65) * mm});
            skLineSegment(sketch, "E1454", {"start": v(-21.76, 36.65) * mm, "end": v(-22.14, 36.42) * mm});
            skLineSegment(sketch, "E1455", {"start": v(-22.14, 36.42) * mm, "end": v(-22.52, 36.2) * mm});
            skLineSegment(sketch, "E1456", {"start": v(-22.52, 36.2) * mm, "end": v(-22.9, 35.96) * mm});
            skLineSegment(sketch, "E1457", {"start": v(-22.9, 35.96) * mm, "end": v(-23.28, 35.73) * mm});
            skLineSegment(sketch, "E1458", {"start": v(-23.28, 35.73) * mm, "end": v(-23.66, 35.5) * mm});
            skLineSegment(sketch, "E1459", {"start": v(-23.66, 35.5) * mm, "end": v(-24.05, 35.27) * mm});
            skLineSegment(sketch, "E1460", {"start": v(-24.05, 35.27) * mm, "end": v(-24.43, 35.03) * mm});
            skLineSegment(sketch, "E1461", {"start": v(-24.43, 35.03) * mm, "end": v(-24.72, 34.86) * mm});
            skLineSegment(sketch, "E1462", {"start": v(-24.72, 34.86) * mm, "end": v(-24.96, 35.23) * mm});
            skLineSegment(sketch, "E1463", {"start": v(-24.96, 35.23) * mm, "end": v(-25.2, 35.6) * mm});
            skLineSegment(sketch, "E1464", {"start": v(-25.2, 35.6) * mm, "end": v(-25.45, 35.98) * mm});
            skLineSegment(sketch, "E1465", {"start": v(-25.45, 35.98) * mm, "end": v(-25.69, 36.35) * mm});
            skLineSegment(sketch, "E1466", {"start": v(-25.69, 36.35) * mm, "end": v(-25.93, 36.73) * mm});
            skLineSegment(sketch, "E1467", {"start": v(-25.93, 36.73) * mm, "end": v(-26.17, 37.1) * mm});
            skLineSegment(sketch, "E1468", {"start": v(-26.17, 37.1) * mm, "end": v(-26.42, 37.47) * mm});
            skLineSegment(sketch, "E1469", {"start": v(-26.42, 37.47) * mm, "end": v(-26.66, 37.85) * mm});
            skLineSegment(sketch, "E1470", {"start": v(-26.66, 37.85) * mm, "end": v(-26.9, 38.22) * mm});
            skLineSegment(sketch, "E1471", {"start": v(-26.9, 38.22) * mm, "end": v(-27.14, 38.6) * mm});
            skLineSegment(sketch, "E1472", {"start": v(-27.14, 38.6) * mm, "end": v(-27.39, 38.97) * mm});
            skLineSegment(sketch, "E1473", {"start": v(-27.39, 38.97) * mm, "end": v(-27.63, 39.34) * mm});
            skLineSegment(sketch, "E1474", {"start": v(-27.63, 39.34) * mm, "end": v(-27.87, 39.72) * mm});
            skLineSegment(sketch, "E1475", {"start": v(-27.87, 39.72) * mm, "end": v(-28.12, 40.1) * mm});
            skLineSegment(sketch, "E1476", {"start": v(-28.12, 40.1) * mm, "end": v(-28.36, 40.46) * mm});
            skLineSegment(sketch, "E1477", {"start": v(-28.36, 40.46) * mm, "end": v(-28.6, 40.84) * mm});
            skLineSegment(sketch, "E1478", {"start": v(-28.6, 40.84) * mm, "end": v(-28.68, 40.96) * mm});
            skLineSegment(sketch, "E1479", {"start": v(-28.68, 40.96) * mm, "end": v(-29.04, 40.7) * mm});
            skLineSegment(sketch, "E1480", {"start": v(-29.04, 40.7) * mm, "end": v(-29.4, 40.44) * mm});
            skLineSegment(sketch, "E1481", {"start": v(-29.4, 40.44) * mm, "end": v(-29.74, 40.2) * mm});
            skLineSegment(sketch, "E1482", {"start": v(-29.74, 40.2) * mm, "end": v(-29.58, 39.78) * mm});
            skLineSegment(sketch, "E1483", {"start": v(-29.58, 39.78) * mm, "end": v(-29.41, 39.36) * mm});
            skLineSegment(sketch, "E1484", {"start": v(-29.41, 39.36) * mm, "end": v(-29.25, 38.95) * mm});
            skLineSegment(sketch, "E1485", {"start": v(-29.25, 38.95) * mm, "end": v(-29.08, 38.54) * mm});
            skLineSegment(sketch, "E1486", {"start": v(-29.08, 38.54) * mm, "end": v(-28.92, 38.12) * mm});
            skLineSegment(sketch, "E1487", {"start": v(-28.92, 38.12) * mm, "end": v(-28.76, 37.7) * mm});
            skLineSegment(sketch, "E1488", {"start": v(-28.76, 37.7) * mm, "end": v(-28.6, 37.3) * mm});
            skLineSegment(sketch, "E1489", {"start": v(-28.6, 37.3) * mm, "end": v(-28.43, 36.88) * mm});
            skLineSegment(sketch, "E1490", {"start": v(-28.43, 36.88) * mm, "end": v(-28.26, 36.46) * mm});
            skLineSegment(sketch, "E1491", {"start": v(-28.26, 36.46) * mm, "end": v(-28.1, 36.05) * mm});
            skLineSegment(sketch, "E1492", {"start": v(-28.1, 36.05) * mm, "end": v(-27.94, 35.64) * mm});
            skLineSegment(sketch, "E1493", {"start": v(-27.94, 35.64) * mm, "end": v(-27.77, 35.22) * mm});
            skLineSegment(sketch, "E1494", {"start": v(-27.77, 35.22) * mm, "end": v(-27.6, 34.8) * mm});
            skLineSegment(sketch, "E1495", {"start": v(-27.6, 34.8) * mm, "end": v(-27.44, 34.4) * mm});
            skLineSegment(sketch, "E1496", {"start": v(-27.44, 34.4) * mm, "end": v(-27.28, 33.98) * mm});
            skLineSegment(sketch, "E1497", {"start": v(-27.28, 33.98) * mm, "end": v(-27.12, 33.56) * mm});
            skLineSegment(sketch, "E1498", {"start": v(-27.12, 33.56) * mm, "end": v(-26.96, 33.16) * mm});
            skLineSegment(sketch, "E1499", {"start": v(-26.96, 33.16) * mm, "end": v(-27.28, 32.85) * mm});
            skLineSegment(sketch, "E1500", {"start": v(-27.28, 32.85) * mm, "end": v(-27.6, 32.55) * mm});
            skLineSegment(sketch, "E1501", {"start": v(-27.6, 32.55) * mm, "end": v(-27.93, 32.24) * mm});
            skLineSegment(sketch, "E1502", {"start": v(-27.93, 32.24) * mm, "end": v(-28.25, 31.94) * mm});
            skLineSegment(sketch, "E1503", {"start": v(-28.25, 31.94) * mm, "end": v(-28.58, 31.63) * mm});
            skLineSegment(sketch, "E1504", {"start": v(-28.58, 31.63) * mm, "end": v(-28.9, 31.33) * mm});
            skLineSegment(sketch, "E1505", {"start": v(-28.9, 31.33) * mm, "end": v(-29.23, 31.02) * mm});
            skLineSegment(sketch, "E1506", {"start": v(-29.23, 31.02) * mm, "end": v(-29.55, 30.72) * mm});
            skLineSegment(sketch, "E1507", {"start": v(-29.55, 30.72) * mm, "end": v(-29.88, 30.41) * mm});
            skLineSegment(sketch, "E1508", {"start": v(-29.88, 30.41) * mm, "end": v(-30.2, 30.1) * mm});
            skLineSegment(sketch, "E1509", {"start": v(-30.2, 30.1) * mm, "end": v(-30.53, 29.8) * mm});
            skLineSegment(sketch, "E1510", {"start": v(-30.53, 29.8) * mm, "end": v(-30.85, 29.5) * mm});
            skLineSegment(sketch, "E1511", {"start": v(-30.85, 29.5) * mm, "end": v(-31.18, 29.2) * mm});
            skLineSegment(sketch, "E1512", {"start": v(-31.18, 29.2) * mm, "end": v(-31.43, 28.96) * mm});
            skLineSegment(sketch, "E1513", {"start": v(-31.43, 28.96) * mm, "end": v(-31.74, 29.27) * mm});
            skLineSegment(sketch, "E1514", {"start": v(-31.74, 29.27) * mm, "end": v(-32.06, 29.59) * mm});
            skLineSegment(sketch, "E1515", {"start": v(-32.06, 29.59) * mm, "end": v(-32.37, 29.9) * mm});
            skLineSegment(sketch, "E1516", {"start": v(-32.37, 29.9) * mm, "end": v(-32.69, 30.22) * mm});
            skLineSegment(sketch, "E1517", {"start": v(-32.69, 30.22) * mm, "end": v(-33, 30.53) * mm});
            skLineSegment(sketch, "E1518", {"start": v(-33, 30.53) * mm, "end": v(-33.32, 30.85) * mm});
            skLineSegment(sketch, "E1519", {"start": v(-33.32, 30.85) * mm, "end": v(-33.63, 31.16) * mm});
            skLineSegment(sketch, "E1520", {"start": v(-33.63, 31.16) * mm, "end": v(-33.95, 31.48) * mm});
            skLineSegment(sketch, "E1521", {"start": v(-33.95, 31.48) * mm, "end": v(-34.26, 31.8) * mm});
            skLineSegment(sketch, "E1522", {"start": v(-34.26, 31.8) * mm, "end": v(-34.58, 32.1) * mm});
            skLineSegment(sketch, "E1523", {"start": v(-34.58, 32.1) * mm, "end": v(-34.9, 32.42) * mm});
            skLineSegment(sketch, "E1524", {"start": v(-34.9, 32.42) * mm, "end": v(-35.2, 32.74) * mm});
            skLineSegment(sketch, "E1525", {"start": v(-35.2, 32.74) * mm, "end": v(-35.52, 33.05) * mm});
            skLineSegment(sketch, "E1526", {"start": v(-35.52, 33.05) * mm, "end": v(-35.84, 33.37) * mm});
            skLineSegment(sketch, "E1527", {"start": v(-35.84, 33.37) * mm, "end": v(-36.15, 33.68) * mm});
            skLineSegment(sketch, "E1528", {"start": v(-36.15, 33.68) * mm, "end": v(-36.47, 34) * mm});
            skLineSegment(sketch, "E1529", {"start": v(-36.47, 34) * mm, "end": v(-36.57, 34.1) * mm});
            skLineSegment(sketch, "E1530", {"start": v(-5.65, 2.24) * mm, "end": v(-5.5, 2.59) * mm});
            skLineSegment(sketch, "E1531", {"start": v(-5.5, 2.59) * mm, "end": v(-5.32, 2.93) * mm});
            skLineSegment(sketch, "E1532", {"start": v(-5.32, 2.93) * mm, "end": v(-5.13, 3.25) * mm});
            skLineSegment(sketch, "E1533", {"start": v(-5.13, 3.25) * mm, "end": v(-4.91, 3.57) * mm});
            skLineSegment(sketch, "E1534", {"start": v(-4.91, 3.57) * mm, "end": v(-4.68, 3.87) * mm});
            skLineSegment(sketch, "E1535", {"start": v(-4.68, 3.87) * mm, "end": v(-4.43, 4.16) * mm});
            skLineSegment(sketch, "E1536", {"start": v(-4.43, 4.16) * mm, "end": v(-4.16, 4.43) * mm});
            skLineSegment(sketch, "E1537", {"start": v(-4.16, 4.43) * mm, "end": v(-3.87, 4.68) * mm});
            skLineSegment(sketch, "E1538", {"start": v(-3.87, 4.68) * mm, "end": v(-3.57, 4.91) * mm});
            skLineSegment(sketch, "E1539", {"start": v(-3.57, 4.91) * mm, "end": v(-3.25, 5.13) * mm});
            skLineSegment(sketch, "E1540", {"start": v(-3.25, 5.13) * mm, "end": v(-2.93, 5.32) * mm});
            skLineSegment(sketch, "E1541", {"start": v(-2.93, 5.32) * mm, "end": v(-2.59, 5.5) * mm});
            skLineSegment(sketch, "E1542", {"start": v(-2.59, 5.5) * mm, "end": v(-2.24, 5.65) * mm});
            skLineSegment(sketch, "E1543", {"start": v(-2.24, 5.65) * mm, "end": v(-2.15, 5.68) * mm});
            skLineSegment(sketch, "E1544", {"start": v(-2.15, 5.68) * mm, "end": v(-2.25, 38.39) * mm});
            skLineSegment(sketch, "E1545", {"start": v(-2.25, 38.39) * mm, "end": v(-2.41, 38.38) * mm});
            skLineSegment(sketch, "E1546", {"start": v(-2.41, 38.38) * mm, "end": v(-4.82, 38.15) * mm});
            skLineSegment(sketch, "E1547", {"start": v(-4.82, 38.15) * mm, "end": v(-7.2, 37.78) * mm});
            skLineSegment(sketch, "E1548", {"start": v(-7.2, 37.78) * mm, "end": v(-9.56, 37.25) * mm});
            skLineSegment(sketch, "E1549", {"start": v(-9.56, 37.25) * mm, "end": v(-11.88, 36.58) * mm});
            skLineSegment(sketch, "E1550", {"start": v(-11.88, 36.58) * mm, "end": v(-14.16, 35.76) * mm});
            skLineSegment(sketch, "E1551", {"start": v(-14.16, 35.76) * mm, "end": v(-16.37, 34.8) * mm});
            skLineSegment(sketch, "E1552", {"start": v(-16.37, 34.8) * mm, "end": v(-18.53, 33.7) * mm});
            skLineSegment(sketch, "E1553", {"start": v(-18.53, 33.7) * mm, "end": v(-20.6, 32.47) * mm});
            skLineSegment(sketch, "E1554", {"start": v(-20.6, 32.47) * mm, "end": v(-22.6, 31.11) * mm});
            skLineSegment(sketch, "E1555", {"start": v(-22.6, 31.11) * mm, "end": v(-24.51, 29.63) * mm});
            skLineSegment(sketch, "E1556", {"start": v(-24.51, 29.63) * mm, "end": v(-26.33, 28.03) * mm});
            skLineSegment(sketch, "E1557", {"start": v(-26.33, 28.03) * mm, "end": v(-28.03, 26.33) * mm});
            skLineSegment(sketch, "E1558", {"start": v(-28.03, 26.33) * mm, "end": v(-29.63, 24.51) * mm});
            skLineSegment(sketch, "E1559", {"start": v(-29.63, 24.51) * mm, "end": v(-31.11, 22.6) * mm});
            skLineSegment(sketch, "E1560", {"start": v(-31.11, 22.6) * mm, "end": v(-32.47, 20.6) * mm});
            skLineSegment(sketch, "E1561", {"start": v(-32.47, 20.6) * mm, "end": v(-33.7, 18.53) * mm});
            skLineSegment(sketch, "E1562", {"start": v(-33.7, 18.53) * mm, "end": v(-34.8, 16.37) * mm});
            skLineSegment(sketch, "E1563", {"start": v(-34.8, 16.37) * mm, "end": v(-35.76, 14.16) * mm});
            skLineSegment(sketch, "E1564", {"start": v(-35.76, 14.16) * mm, "end": v(-36.58, 11.88) * mm});
            skLineSegment(sketch, "E1565", {"start": v(-36.58, 11.88) * mm, "end": v(-37.25, 9.56) * mm});
            skLineSegment(sketch, "E1566", {"start": v(-37.25, 9.56) * mm, "end": v(-37.78, 7.2) * mm});
            skLineSegment(sketch, "E1567", {"start": v(-37.78, 7.2) * mm, "end": v(-38.15, 4.82) * mm});
            skLineSegment(sketch, "E1568", {"start": v(-38.15, 4.82) * mm, "end": v(-38.38, 2.41) * mm});
            skLineSegment(sketch, "E1569", {"start": v(-38.38, 2.41) * mm, "end": v(-38.39, 2.25) * mm});
            skLineSegment(sketch, "E1570", {"start": v(-38.39, 2.25) * mm, "end": v(-5.68, 2.15) * mm});
            skLineSegment(sketch, "E1571", {"start": v(-5.68, 2.15) * mm, "end": v(-5.65, 2.24) * mm});
            skLineSegment(sketch, "E1572", {"start": v(38.39, 2.25) * mm, "end": v(38.38, 2.41) * mm});
            skLineSegment(sketch, "E1573", {"start": v(38.38, 2.41) * mm, "end": v(38.15, 4.82) * mm});
            skLineSegment(sketch, "E1574", {"start": v(38.15, 4.82) * mm, "end": v(37.78, 7.2) * mm});
            skLineSegment(sketch, "E1575", {"start": v(37.78, 7.2) * mm, "end": v(37.25, 9.56) * mm});
            skLineSegment(sketch, "E1576", {"start": v(37.25, 9.56) * mm, "end": v(36.58, 11.88) * mm});
            skLineSegment(sketch, "E1577", {"start": v(36.58, 11.88) * mm, "end": v(35.76, 14.16) * mm});
            skLineSegment(sketch, "E1578", {"start": v(35.76, 14.16) * mm, "end": v(34.8, 16.37) * mm});
            skLineSegment(sketch, "E1579", {"start": v(34.8, 16.37) * mm, "end": v(33.7, 18.53) * mm});
            skLineSegment(sketch, "E1580", {"start": v(33.7, 18.53) * mm, "end": v(32.47, 20.6) * mm});
            skLineSegment(sketch, "E1581", {"start": v(32.47, 20.6) * mm, "end": v(31.11, 22.6) * mm});
            skLineSegment(sketch, "E1582", {"start": v(31.11, 22.6) * mm, "end": v(29.63, 24.51) * mm});
            skLineSegment(sketch, "E1583", {"start": v(29.63, 24.51) * mm, "end": v(28.03, 26.33) * mm});
            skLineSegment(sketch, "E1584", {"start": v(28.03, 26.33) * mm, "end": v(26.33, 28.03) * mm});
            skLineSegment(sketch, "E1585", {"start": v(26.33, 28.03) * mm, "end": v(24.51, 29.63) * mm});
            skLineSegment(sketch, "E1586", {"start": v(24.51, 29.63) * mm, "end": v(22.6, 31.11) * mm});
            skLineSegment(sketch, "E1587", {"start": v(22.6, 31.11) * mm, "end": v(20.6, 32.47) * mm});
            skLineSegment(sketch, "E1588", {"start": v(20.6, 32.47) * mm, "end": v(18.53, 33.7) * mm});
            skLineSegment(sketch, "E1589", {"start": v(18.53, 33.7) * mm, "end": v(16.37, 34.8) * mm});
            skLineSegment(sketch, "E1590", {"start": v(16.37, 34.8) * mm, "end": v(14.16, 35.76) * mm});
            skLineSegment(sketch, "E1591", {"start": v(14.16, 35.76) * mm, "end": v(11.88, 36.58) * mm});
            skLineSegment(sketch, "E1592", {"start": v(11.88, 36.58) * mm, "end": v(9.56, 37.25) * mm});
            skLineSegment(sketch, "E1593", {"start": v(9.56, 37.25) * mm, "end": v(7.2, 37.78) * mm});
            skLineSegment(sketch, "E1594", {"start": v(7.2, 37.78) * mm, "end": v(4.82, 38.15) * mm});
            skLineSegment(sketch, "E1595", {"start": v(4.82, 38.15) * mm, "end": v(2.41, 38.38) * mm});
            skLineSegment(sketch, "E1596", {"start": v(2.41, 38.38) * mm, "end": v(2.25, 38.39) * mm});
            skLineSegment(sketch, "E1597", {"start": v(2.25, 38.39) * mm, "end": v(2.15, 5.68) * mm});
            skLineSegment(sketch, "E1598", {"start": v(2.15, 5.68) * mm, "end": v(2.24, 5.65) * mm});
            skLineSegment(sketch, "E1599", {"start": v(2.24, 5.65) * mm, "end": v(2.59, 5.5) * mm});
            skLineSegment(sketch, "E1600", {"start": v(2.59, 5.5) * mm, "end": v(2.93, 5.32) * mm});
            skLineSegment(sketch, "E1601", {"start": v(2.93, 5.32) * mm, "end": v(3.25, 5.13) * mm});
            skLineSegment(sketch, "E1602", {"start": v(3.25, 5.13) * mm, "end": v(3.57, 4.91) * mm});
            skLineSegment(sketch, "E1603", {"start": v(3.57, 4.91) * mm, "end": v(3.87, 4.68) * mm});
            skLineSegment(sketch, "E1604", {"start": v(3.87, 4.68) * mm, "end": v(4.16, 4.43) * mm});
            skLineSegment(sketch, "E1605", {"start": v(4.16, 4.43) * mm, "end": v(4.43, 4.16) * mm});
            skLineSegment(sketch, "E1606", {"start": v(4.43, 4.16) * mm, "end": v(4.68, 3.87) * mm});
            skLineSegment(sketch, "E1607", {"start": v(4.68, 3.87) * mm, "end": v(4.91, 3.57) * mm});
            skLineSegment(sketch, "E1608", {"start": v(4.91, 3.57) * mm, "end": v(5.13, 3.25) * mm});
            skLineSegment(sketch, "E1609", {"start": v(5.13, 3.25) * mm, "end": v(5.32, 2.93) * mm});
            skLineSegment(sketch, "E1610", {"start": v(5.32, 2.93) * mm, "end": v(5.5, 2.59) * mm});
            skLineSegment(sketch, "E1611", {"start": v(5.5, 2.59) * mm, "end": v(5.65, 2.24) * mm});
            skLineSegment(sketch, "E1612", {"start": v(5.65, 2.24) * mm, "end": v(5.68, 2.15) * mm});
            skLineSegment(sketch, "E1613", {"start": v(5.68, 2.15) * mm, "end": v(38.39, 2.25) * mm});
            skLineSegment(sketch, "E1614", {"start": v(2.41, -38.38) * mm, "end": v(4.82, -38.15) * mm});
            skLineSegment(sketch, "E1615", {"start": v(4.82, -38.15) * mm, "end": v(7.2, -37.78) * mm});
            skLineSegment(sketch, "E1616", {"start": v(7.2, -37.78) * mm, "end": v(9.56, -37.25) * mm});
            skLineSegment(sketch, "E1617", {"start": v(9.56, -37.25) * mm, "end": v(11.88, -36.58) * mm});
            skLineSegment(sketch, "E1618", {"start": v(11.88, -36.58) * mm, "end": v(14.16, -35.76) * mm});
            skLineSegment(sketch, "E1619", {"start": v(14.16, -35.76) * mm, "end": v(16.37, -34.8) * mm});
            skLineSegment(sketch, "E1620", {"start": v(16.37, -34.8) * mm, "end": v(18.53, -33.7) * mm});
            skLineSegment(sketch, "E1621", {"start": v(18.53, -33.7) * mm, "end": v(20.6, -32.47) * mm});
            skLineSegment(sketch, "E1622", {"start": v(20.6, -32.47) * mm, "end": v(22.6, -31.11) * mm});
            skLineSegment(sketch, "E1623", {"start": v(22.6, -31.11) * mm, "end": v(24.51, -29.63) * mm});
            skLineSegment(sketch, "E1624", {"start": v(24.51, -29.63) * mm, "end": v(26.33, -28.03) * mm});
            skLineSegment(sketch, "E1625", {"start": v(26.33, -28.03) * mm, "end": v(28.03, -26.33) * mm});
            skLineSegment(sketch, "E1626", {"start": v(28.03, -26.33) * mm, "end": v(29.63, -24.51) * mm});
            skLineSegment(sketch, "E1627", {"start": v(29.63, -24.51) * mm, "end": v(31.11, -22.6) * mm});
            skLineSegment(sketch, "E1628", {"start": v(31.11, -22.6) * mm, "end": v(32.47, -20.6) * mm});
            skLineSegment(sketch, "E1629", {"start": v(32.47, -20.6) * mm, "end": v(33.7, -18.53) * mm});
            skLineSegment(sketch, "E1630", {"start": v(33.7, -18.53) * mm, "end": v(34.8, -16.37) * mm});
            skLineSegment(sketch, "E1631", {"start": v(34.8, -16.37) * mm, "end": v(35.76, -14.16) * mm});
            skLineSegment(sketch, "E1632", {"start": v(35.76, -14.16) * mm, "end": v(36.58, -11.88) * mm});
            skLineSegment(sketch, "E1633", {"start": v(36.58, -11.88) * mm, "end": v(37.25, -9.56) * mm});
            skLineSegment(sketch, "E1634", {"start": v(37.25, -9.56) * mm, "end": v(37.78, -7.2) * mm});
            skLineSegment(sketch, "E1635", {"start": v(37.78, -7.2) * mm, "end": v(38.15, -4.82) * mm});
            skLineSegment(sketch, "E1636", {"start": v(38.15, -4.82) * mm, "end": v(38.38, -2.41) * mm});
            skLineSegment(sketch, "E1637", {"start": v(38.38, -2.41) * mm, "end": v(38.39, -2.25) * mm});
            skLineSegment(sketch, "E1638", {"start": v(38.39, -2.25) * mm, "end": v(5.68, -2.15) * mm});
            skLineSegment(sketch, "E1639", {"start": v(5.68, -2.15) * mm, "end": v(5.65, -2.24) * mm});
            skLineSegment(sketch, "E1640", {"start": v(5.65, -2.24) * mm, "end": v(5.5, -2.59) * mm});
            skLineSegment(sketch, "E1641", {"start": v(5.5, -2.59) * mm, "end": v(5.32, -2.93) * mm});
            skLineSegment(sketch, "E1642", {"start": v(5.32, -2.93) * mm, "end": v(5.13, -3.25) * mm});
            skLineSegment(sketch, "E1643", {"start": v(5.13, -3.25) * mm, "end": v(4.91, -3.57) * mm});
            skLineSegment(sketch, "E1644", {"start": v(4.91, -3.57) * mm, "end": v(4.68, -3.87) * mm});
            skLineSegment(sketch, "E1645", {"start": v(4.68, -3.87) * mm, "end": v(4.43, -4.16) * mm});
            skLineSegment(sketch, "E1646", {"start": v(4.43, -4.16) * mm, "end": v(4.16, -4.43) * mm});
            skLineSegment(sketch, "E1647", {"start": v(4.16, -4.43) * mm, "end": v(3.87, -4.68) * mm});
            skLineSegment(sketch, "E1648", {"start": v(3.87, -4.68) * mm, "end": v(3.57, -4.91) * mm});
            skLineSegment(sketch, "E1649", {"start": v(3.57, -4.91) * mm, "end": v(3.25, -5.13) * mm});
            skLineSegment(sketch, "E1650", {"start": v(3.25, -5.13) * mm, "end": v(2.93, -5.32) * mm});
            skLineSegment(sketch, "E1651", {"start": v(2.93, -5.32) * mm, "end": v(2.59, -5.5) * mm});
            skLineSegment(sketch, "E1652", {"start": v(2.59, -5.5) * mm, "end": v(2.24, -5.65) * mm});
            skLineSegment(sketch, "E1653", {"start": v(2.24, -5.65) * mm, "end": v(2.15, -5.68) * mm});
            skLineSegment(sketch, "E1654", {"start": v(2.15, -5.68) * mm, "end": v(2.25, -38.39) * mm});
            skLineSegment(sketch, "E1655", {"start": v(2.25, -38.39) * mm, "end": v(2.41, -38.38) * mm});
            skLineSegment(sketch, "E1656", {"start": v(-2.15, -5.68) * mm, "end": v(-2.24, -5.65) * mm});
            skLineSegment(sketch, "E1657", {"start": v(-2.24, -5.65) * mm, "end": v(-2.59, -5.5) * mm});
            skLineSegment(sketch, "E1658", {"start": v(-2.59, -5.5) * mm, "end": v(-2.93, -5.32) * mm});
            skLineSegment(sketch, "E1659", {"start": v(-2.93, -5.32) * mm, "end": v(-3.25, -5.13) * mm});
            skLineSegment(sketch, "E1660", {"start": v(-3.25, -5.13) * mm, "end": v(-3.57, -4.91) * mm});
            skLineSegment(sketch, "E1661", {"start": v(-3.57, -4.91) * mm, "end": v(-3.87, -4.68) * mm});
            skLineSegment(sketch, "E1662", {"start": v(-3.87, -4.68) * mm, "end": v(-4.16, -4.43) * mm});
            skLineSegment(sketch, "E1663", {"start": v(-4.16, -4.43) * mm, "end": v(-4.43, -4.16) * mm});
            skLineSegment(sketch, "E1664", {"start": v(-4.43, -4.16) * mm, "end": v(-4.68, -3.87) * mm});
            skLineSegment(sketch, "E1665", {"start": v(-4.68, -3.87) * mm, "end": v(-4.91, -3.57) * mm});
            skLineSegment(sketch, "E1666", {"start": v(-4.91, -3.57) * mm, "end": v(-5.13, -3.25) * mm});
            skLineSegment(sketch, "E1667", {"start": v(-5.13, -3.25) * mm, "end": v(-5.32, -2.93) * mm});
            skLineSegment(sketch, "E1668", {"start": v(-5.32, -2.93) * mm, "end": v(-5.5, -2.59) * mm});
            skLineSegment(sketch, "E1669", {"start": v(-5.5, -2.59) * mm, "end": v(-5.65, -2.24) * mm});
            skLineSegment(sketch, "E1670", {"start": v(-5.65, -2.24) * mm, "end": v(-5.68, -2.15) * mm});
            skLineSegment(sketch, "E1671", {"start": v(-5.68, -2.15) * mm, "end": v(-38.39, -2.25) * mm});
            skLineSegment(sketch, "E1672", {"start": v(-38.39, -2.25) * mm, "end": v(-38.38, -2.41) * mm});
            skLineSegment(sketch, "E1673", {"start": v(-38.38, -2.41) * mm, "end": v(-38.15, -4.82) * mm});
            skLineSegment(sketch, "E1674", {"start": v(-38.15, -4.82) * mm, "end": v(-37.78, -7.2) * mm});
            skLineSegment(sketch, "E1675", {"start": v(-37.78, -7.2) * mm, "end": v(-37.25, -9.56) * mm});
            skLineSegment(sketch, "E1676", {"start": v(-37.25, -9.56) * mm, "end": v(-36.58, -11.88) * mm});
            skLineSegment(sketch, "E1677", {"start": v(-36.58, -11.88) * mm, "end": v(-35.76, -14.16) * mm});
            skLineSegment(sketch, "E1678", {"start": v(-35.76, -14.16) * mm, "end": v(-34.8, -16.37) * mm});
            skLineSegment(sketch, "E1679", {"start": v(-34.8, -16.37) * mm, "end": v(-33.7, -18.53) * mm});
            skLineSegment(sketch, "E1680", {"start": v(-33.7, -18.53) * mm, "end": v(-32.47, -20.6) * mm});
            skLineSegment(sketch, "E1681", {"start": v(-32.47, -20.6) * mm, "end": v(-31.11, -22.6) * mm});
            skLineSegment(sketch, "E1682", {"start": v(-31.11, -22.6) * mm, "end": v(-29.63, -24.51) * mm});
            skLineSegment(sketch, "E1683", {"start": v(-29.63, -24.51) * mm, "end": v(-28.03, -26.33) * mm});
            skLineSegment(sketch, "E1684", {"start": v(-28.03, -26.33) * mm, "end": v(-26.33, -28.03) * mm});
            skLineSegment(sketch, "E1685", {"start": v(-26.33, -28.03) * mm, "end": v(-24.51, -29.63) * mm});
            skLineSegment(sketch, "E1686", {"start": v(-24.51, -29.63) * mm, "end": v(-22.6, -31.11) * mm});
            skLineSegment(sketch, "E1687", {"start": v(-22.6, -31.11) * mm, "end": v(-20.6, -32.47) * mm});
            skLineSegment(sketch, "E1688", {"start": v(-20.6, -32.47) * mm, "end": v(-18.53, -33.7) * mm});
            skLineSegment(sketch, "E1689", {"start": v(-18.53, -33.7) * mm, "end": v(-16.37, -34.8) * mm});
            skLineSegment(sketch, "E1690", {"start": v(-16.37, -34.8) * mm, "end": v(-14.16, -35.76) * mm});
            skLineSegment(sketch, "E1691", {"start": v(-14.16, -35.76) * mm, "end": v(-11.88, -36.58) * mm});
            skLineSegment(sketch, "E1692", {"start": v(-11.88, -36.58) * mm, "end": v(-9.56, -37.25) * mm});
            skLineSegment(sketch, "E1693", {"start": v(-9.56, -37.25) * mm, "end": v(-7.2, -37.78) * mm});
            skLineSegment(sketch, "E1694", {"start": v(-7.2, -37.78) * mm, "end": v(-4.82, -38.15) * mm});
            skLineSegment(sketch, "E1695", {"start": v(-4.82, -38.15) * mm, "end": v(-2.41, -38.38) * mm});
            skLineSegment(sketch, "E1696", {"start": v(-2.41, -38.38) * mm, "end": v(-2.25, -38.39) * mm});
            skLineSegment(sketch, "E1697", {"start": v(-2.25, -38.39) * mm, "end": v(-2.15, -5.68) * mm});
            skCircle(sketch, "E1698", {"center": v(0, 0) * mm, "radius": 2.65 * mm});
            skCircle(sketch, "E1699", {"center": v(0, 0) * mm, "radius": 26.5 * mm});
            skCircle(sketch, "E1700", {"center": v(0, 0) * mm, "radius": 19.46 * mm});
            skSolve(sketch);
        }
        {
            var Q0;
            Q0 = qSketchRegion(id + "F0", true);
            var Q1;
            Q1=makeQuery(id+"F0.imprint","IMPRINT",FACE,{"disambiguationData":[TD([[makeQuery(id+"F0.imprint","IMPRINT",EDGE,{"derivedFrom":sQuery(id+"F0.wireOp",EDGE,"E0")}),1.0]])]});
            var Q2;
            {var subQ0=sQuery(id+"F0.wireOp",EDGE,"E1700");var subQ1=sQuery(id+"F0.wireOp",EDGE,"E1544");var subQ2=makeQuery(id+"F0.imprint","INTERSECT",VERTEX,{"derivedFrom":[subQ1,subQ0]});Q2=makeQuery(id+"F0.imprint","IMPRINT",FACE,{"disambiguationData":[TD([[makeQuery(id+"F0.imprint","IMPRINT",EDGE,{"disambiguationData":[TD([[subQ2,-1.0]])],"derivedFrom":subQ1}),1.0]])]});}
            var Q3;
            {var subQ0=sQuery(id+"F0.wireOp",EDGE,"E1699");var subQ1=sQuery(id+"F0.wireOp",EDGE,"E1570");var subQ2=makeQuery(id+"F0.imprint","INTERSECT",VERTEX,{"derivedFrom":[subQ1,subQ0]});Q3=makeQuery(id+"F0.imprint","IMPRINT",FACE,{"disambiguationData":[TD([[makeQuery(id+"F0.imprint","IMPRINT",EDGE,{"disambiguationData":[TD([[subQ2,-1.0]])],"derivedFrom":subQ1}),-1.0]])]});}
            var Q4;
            {var subQ0=sQuery(id+"F0.wireOp",EDGE,"E1700");var subQ1=sQuery(id+"F0.wireOp",EDGE,"E1654");var subQ2=makeQuery(id+"F0.imprint","INTERSECT",VERTEX,{"derivedFrom":[subQ1,subQ0]});Q4=makeQuery(id+"F0.imprint","IMPRINT",FACE,{"disambiguationData":[TD([[makeQuery(id+"F0.imprint","IMPRINT",EDGE,{"disambiguationData":[TD([[subQ2,-1.0]])],"derivedFrom":subQ1}),-1.0]])]});}
            var Q5;
            {var subQ0=sQuery(id+"F0.wireOp",EDGE,"E1699");var subQ1=sQuery(id+"F0.wireOp",EDGE,"E1638");var subQ2=makeQuery(id+"F0.imprint","INTERSECT",VERTEX,{"derivedFrom":[subQ1,subQ0]});Q5=makeQuery(id+"F0.imprint","IMPRINT",FACE,{"disambiguationData":[TD([[makeQuery(id+"F0.imprint","IMPRINT",EDGE,{"disambiguationData":[TD([[subQ2,-1.0]])],"derivedFrom":subQ1}),1.0]])]});}
            var Q6;
            {var subQ0=sQuery(id+"F0.wireOp",EDGE,"E1700");var subQ1=sQuery(id+"F0.wireOp",EDGE,"E1613");var subQ2=makeQuery(id+"F0.imprint","INTERSECT",VERTEX,{"derivedFrom":[subQ1,subQ0]});Q6=makeQuery(id+"F0.imprint","IMPRINT",FACE,{"disambiguationData":[TD([[makeQuery(id+"F0.imprint","IMPRINT",EDGE,{"disambiguationData":[TD([[subQ2,-1.0]])],"derivedFrom":subQ1}),-1.0]])]});}
            var Q7;
            {var subQ0=sQuery(id+"F0.wireOp",EDGE,"E1699");var subQ1=sQuery(id+"F0.wireOp",EDGE,"E1597");var subQ2=makeQuery(id+"F0.imprint","INTERSECT",VERTEX,{"derivedFrom":[subQ1,subQ0]});Q7=makeQuery(id+"F0.imprint","IMPRINT",FACE,{"disambiguationData":[TD([[makeQuery(id+"F0.imprint","IMPRINT",EDGE,{"disambiguationData":[TD([[subQ2,-1.0]])],"derivedFrom":subQ1}),1.0]])]});}
            var Q8;
            Q8=makeQuery(id+"F0.imprint","IMPRINT",FACE,{"disambiguationData":[TD([[makeQuery(id+"F0.imprint","IMPRINT",EDGE,{"derivedFrom":sQuery(id+"F0.wireOp",EDGE,"E1530")}),-1.0]])]});
            var Q9;
            {var subQ0=sQuery(id+"F0.wireOp",EDGE,"E1700");var subQ1=sQuery(id+"F0.wireOp",EDGE,"E1544");var subQ2=makeQuery(id+"F0.imprint","INTERSECT",VERTEX,{"derivedFrom":[subQ1,subQ0]});Q9=makeQuery(id+"F0.imprint","IMPRINT",FACE,{"disambiguationData":[TD([[makeQuery(id+"F0.imprint","IMPRINT",EDGE,{"disambiguationData":[TD([[subQ2,-1.0]])],"derivedFrom":subQ1}),-1.0]])]});}
            var Q10;
            {var subQ0=sQuery(id+"F0.wireOp",EDGE,"E1700");var subQ1=sQuery(id+"F0.wireOp",EDGE,"E1671");var subQ2=makeQuery(id+"F0.imprint","INTERSECT",VERTEX,{"derivedFrom":[subQ1,subQ0]});Q10=makeQuery(id+"F0.imprint","IMPRINT",FACE,{"disambiguationData":[TD([[makeQuery(id+"F0.imprint","IMPRINT",EDGE,{"disambiguationData":[TD([[subQ2,-1.0]])],"derivedFrom":subQ1}),1.0]])]});}
            extrude(context, id + "F1", {"entities" : qUnion([Q0, Q1, Q2, Q3, Q4, Q5, Q6, Q7, Q8, Q9, Q10]), "depth" : 5 * mm});
        }
    });
